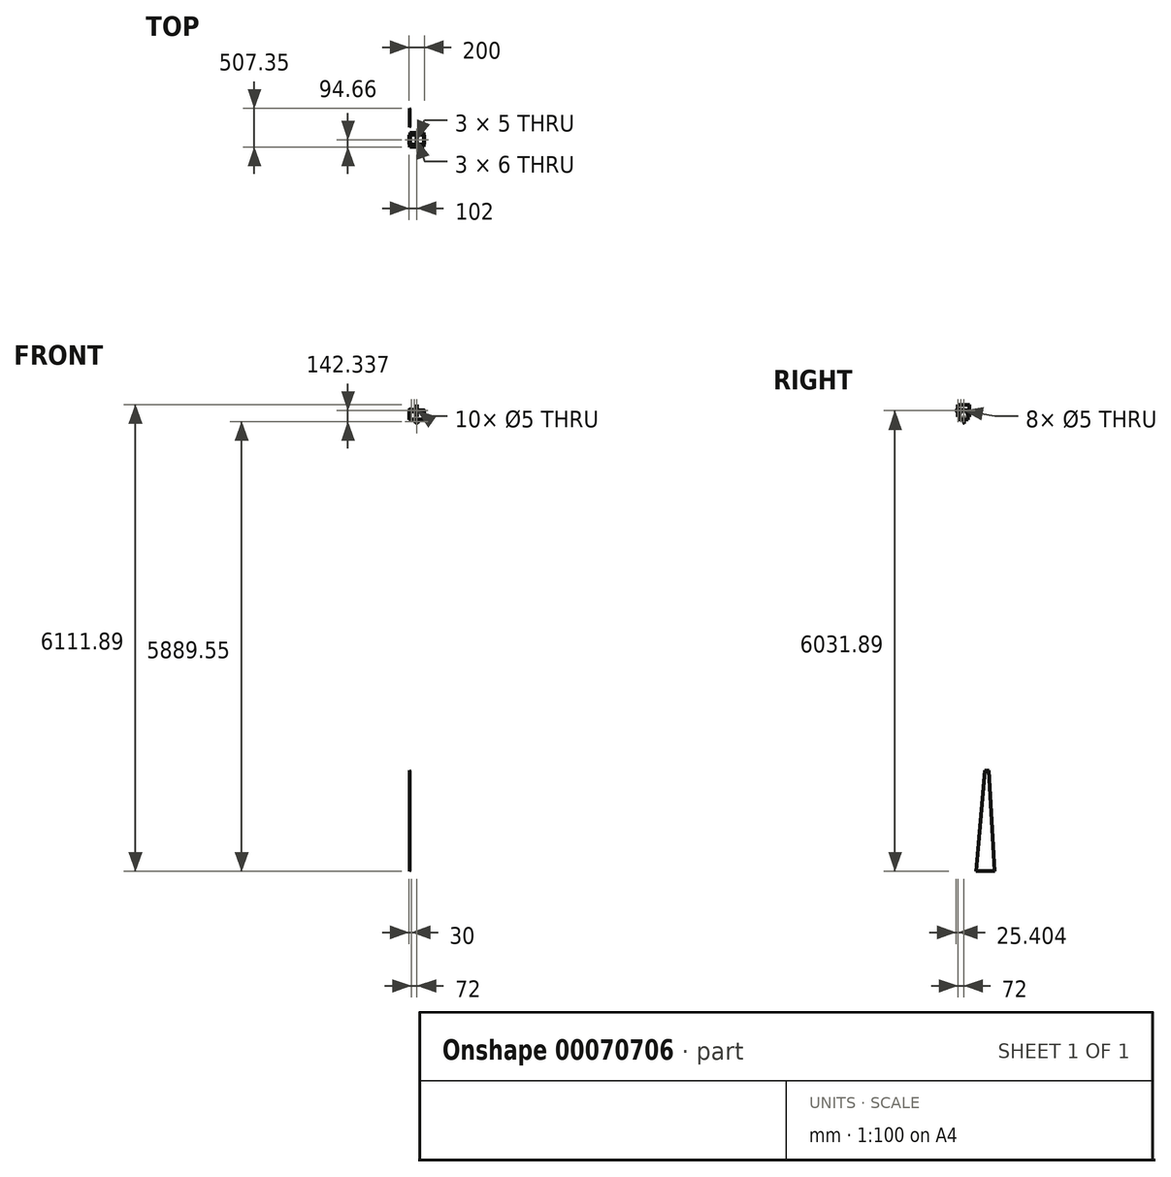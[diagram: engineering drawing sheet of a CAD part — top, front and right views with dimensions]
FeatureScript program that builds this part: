
annotation { "Feature Type Name" : "Feature", "Feature Type Description" : "" }
export const myFeature = defineFeature(function(context is Context, id is Id, definition is map)
    precondition{}
    {
        {
            var Q0;
            Q0=qCreatedBy(makeId("Top.planeOp"),FACE);
            var sketch = newSketch(context, id + "F0", { "sketchPlane" : qUnion([Q0])});
            skLineSegment(sketch, "E0.rect.bottom", {"start": v(100, 60) * mm, "end": v(-94, 60) * mm});
            skLineSegment(sketch, "E0.rect.top", {"start": v(94, -60) * mm, "end": v(-100, -60) * mm});
            skLineSegment(sketch, "E0.rect.left", {"start": v(100, 60) * mm, "end": v(100, 55) * mm});
            skLineSegment(sketch, "E0.rect.right", {"start": v(-100, 55) * mm, "end": v(-100, 50) * mm});
            skPoint(sketch, "E0.rect.middle", {"position": v(0, 0) * mm});
            skLineSegment(sketch, "E1.bottom", {"start": v(100, 55) * mm, "end": v(94, 55) * mm});
            skLineSegment(sketch, "E1.top", {"start": v(100, 50) * mm, "end": v(94, 50) * mm});
            skLineSegment(sketch, "E1.right", {"start": v(94, 55) * mm, "end": v(94, 50) * mm});
            skLineSegment(sketch, "E2.0.1.0", {"start": v(100, 45) * mm, "end": v(94, 45) * mm});
            skLineSegment(sketch, "E2.0.1.1", {"start": v(94, 45) * mm, "end": v(94, 40) * mm});
            skLineSegment(sketch, "E2.0.1.2", {"start": v(100, 40) * mm, "end": v(94, 40) * mm});
            skLineSegment(sketch, "E2.0.2.0", {"start": v(100, 35) * mm, "end": v(94, 35) * mm});
            skLineSegment(sketch, "E2.0.2.1", {"start": v(94, 35) * mm, "end": v(94, 30) * mm});
            skLineSegment(sketch, "E2.0.2.2", {"start": v(100, 30) * mm, "end": v(94, 30) * mm});
            skLineSegment(sketch, "E2.0.3.0", {"start": v(100, 25) * mm, "end": v(94, 25) * mm});
            skLineSegment(sketch, "E2.0.3.1", {"start": v(94, 25) * mm, "end": v(94, 20) * mm});
            skLineSegment(sketch, "E2.0.3.2", {"start": v(100, 20) * mm, "end": v(94, 20) * mm});
            skLineSegment(sketch, "E2.0.4.0", {"start": v(100, 15) * mm, "end": v(94, 15) * mm});
            skLineSegment(sketch, "E2.0.4.1", {"start": v(94, 15) * mm, "end": v(94, 10) * mm});
            skLineSegment(sketch, "E2.0.4.2", {"start": v(100, 10) * mm, "end": v(94, 10) * mm});
            skLineSegment(sketch, "E2.0.5.0", {"start": v(100, 5) * mm, "end": v(94, 5) * mm});
            skLineSegment(sketch, "E2.0.5.1", {"start": v(94, 5) * mm, "end": v(94, 0) * mm});
            skLineSegment(sketch, "E2.0.5.2", {"start": v(100, 0) * mm, "end": v(94, 0) * mm});
            skLineSegment(sketch, "E2.0.6.0", {"start": v(100, -5) * mm, "end": v(94, -5) * mm});
            skLineSegment(sketch, "E2.0.6.1", {"start": v(94, -5) * mm, "end": v(94, -10) * mm});
            skLineSegment(sketch, "E2.0.6.2", {"start": v(100, -10) * mm, "end": v(94, -10) * mm});
            skLineSegment(sketch, "E2.0.7.0", {"start": v(100, -15) * mm, "end": v(94, -15) * mm});
            skLineSegment(sketch, "E2.0.7.1", {"start": v(94, -15) * mm, "end": v(94, -20) * mm});
            skLineSegment(sketch, "E2.0.7.2", {"start": v(100, -20) * mm, "end": v(94, -20) * mm});
            skLineSegment(sketch, "E2.0.8.0", {"start": v(100, -25) * mm, "end": v(94, -25) * mm});
            skLineSegment(sketch, "E2.0.8.1", {"start": v(94, -25) * mm, "end": v(94, -30) * mm});
            skLineSegment(sketch, "E2.0.8.2", {"start": v(100, -30) * mm, "end": v(94, -30) * mm});
            skLineSegment(sketch, "E2.0.9.0", {"start": v(100, -35) * mm, "end": v(94, -35) * mm});
            skLineSegment(sketch, "E2.0.9.1", {"start": v(94, -35) * mm, "end": v(94, -40) * mm});
            skLineSegment(sketch, "E2.0.9.2", {"start": v(100, -40) * mm, "end": v(94, -40) * mm});
            skLineSegment(sketch, "E2.0.10.0", {"start": v(100, -45) * mm, "end": v(94, -45) * mm});
            skLineSegment(sketch, "E2.0.10.1", {"start": v(94, -45) * mm, "end": v(94, -50) * mm});
            skLineSegment(sketch, "E2.0.10.2", {"start": v(100, -50) * mm, "end": v(94, -50) * mm});
            skLineSegment(sketch, "E2.0.11.0", {"start": v(100, -55) * mm, "end": v(94, -55) * mm});
            skLineSegment(sketch, "E2.0.11.1", {"start": v(94, -55) * mm, "end": v(94, -60) * mm});
            skLineSegment(sketch, "E2.direction1", {"start": v(94, 55) * mm, "end": v(119, 55) * mm, "construction": true});
            skLineSegment(sketch, "E2.direction2", {"start": v(94, 55) * mm, "end": v(94, 45) * mm, "construction": true});
            skLineSegment(sketch, "E3", {"start": v(0, -60) * mm, "end": v(0, 60) * mm, "construction": true});
            skLineSegment(sketch, "E4.1.0", {"start": v(-100, -30) * mm, "end": v(-94.03, -29.38) * mm});
            skLineSegment(sketch, "E4.1.1", {"start": v(-100, 15) * mm, "end": v(-94, 15) * mm});
            skLineSegment(sketch, "E4.1.2", {"start": v(-94.03, -34.38) * mm, "end": v(-94.03, -29.38) * mm});
            skLineSegment(sketch, "E4.1.3", {"start": v(-100, 30) * mm, "end": v(-94, 30) * mm});
            skLineSegment(sketch, "E4.1.4", {"start": v(-100, 0) * mm, "end": v(-94, 0) * mm});
            skLineSegment(sketch, "E4.1.5", {"start": v(-100, 55) * mm, "end": v(-94, 55) * mm});
            skLineSegment(sketch, "E4.1.6", {"start": v(-94, 55) * mm, "end": v(-94, 60) * mm});
            skLineSegment(sketch, "E4.1.7", {"start": v(-100, -25) * mm, "end": v(-94, -25) * mm});
            skLineSegment(sketch, "E4.1.8", {"start": v(-100, 5) * mm, "end": v(-94, 5) * mm});
            skLineSegment(sketch, "E4.1.9", {"start": v(-94, -25) * mm, "end": v(-94, -20) * mm});
            skLineSegment(sketch, "E4.1.10", {"start": v(-100, 35) * mm, "end": v(-94, 35) * mm});
            skLineSegment(sketch, "E4.1.11", {"start": v(-100, -20) * mm, "end": v(-94, -20) * mm});
            skLineSegment(sketch, "E4.1.12", {"start": v(-100, -35) * mm, "end": v(-94.03, -34.38) * mm});
            skLineSegment(sketch, "E4.1.13", {"start": v(-100, -40) * mm, "end": v(-94, -40) * mm});
            skLineSegment(sketch, "E4.1.14", {"start": v(-94, -45) * mm, "end": v(-94, -40) * mm});
            skLineSegment(sketch, "E4.1.15", {"start": v(-94, -55) * mm, "end": v(-94, -50) * mm});
            skLineSegment(sketch, "E4.1.16", {"start": v(-94, 25) * mm, "end": v(-94, 30) * mm});
            skLineSegment(sketch, "E4.1.17", {"start": v(-100, 50) * mm, "end": v(-94, 50) * mm});
            skLineSegment(sketch, "E4.1.18", {"start": v(-94, -5) * mm, "end": v(-94, 0) * mm});
            skLineSegment(sketch, "E4.1.19", {"start": v(-100, 20) * mm, "end": v(-94, 20) * mm});
            skLineSegment(sketch, "E4.1.20", {"start": v(-94, 45) * mm, "end": v(-94, 50) * mm});
            skLineSegment(sketch, "E4.1.21", {"start": v(-100, 25) * mm, "end": v(-94, 25) * mm});
            skLineSegment(sketch, "E4.1.22", {"start": v(-100, 40) * mm, "end": v(-94, 40) * mm});
            skLineSegment(sketch, "E4.1.23", {"start": v(-100, -5) * mm, "end": v(-94, -5) * mm});
            skLineSegment(sketch, "E4.1.24", {"start": v(-94, 15) * mm, "end": v(-94, 20) * mm});
            skLineSegment(sketch, "E4.1.25", {"start": v(-94, -15) * mm, "end": v(-94, -10) * mm});
            skLineSegment(sketch, "E4.1.26", {"start": v(-100, 10) * mm, "end": v(-94, 10) * mm});
            skLineSegment(sketch, "E4.1.27", {"start": v(-94, 35) * mm, "end": v(-94, 40) * mm});
            skLineSegment(sketch, "E4.1.28", {"start": v(-100, 45) * mm, "end": v(-94, 45) * mm});
            skLineSegment(sketch, "E4.1.29", {"start": v(-100, -10) * mm, "end": v(-94, -10) * mm});
            skLineSegment(sketch, "E4.1.30", {"start": v(-100, -15) * mm, "end": v(-94, -15) * mm});
            skLineSegment(sketch, "E4.1.31", {"start": v(-94, 5) * mm, "end": v(-94, 10) * mm});
            skLineSegment(sketch, "E4.1.32", {"start": v(-100, -45) * mm, "end": v(-94, -45) * mm});
            skLineSegment(sketch, "E4.1.33", {"start": v(-100, -50) * mm, "end": v(-94, -50) * mm});
            skLineSegment(sketch, "E4.1.35", {"start": v(-100, -55) * mm, "end": v(-94, -55) * mm});
            skPoint(sketch, "E4.center", {"position": v(-1, 0) * mm});
            skLineSegment(sketch, "E4.anchor1", {"start": v(-1, 0) * mm, "end": v(94, 30) * mm, "construction": true});
            skLineSegment(sketch, "E4.anchor2", {"start": v(-1, 0) * mm, "end": v(-94.03, -29.38) * mm, "construction": true});
            skLineSegment(sketch, "E5.trimOffspring", {"start": v(100, 50) * mm, "end": v(100, 45) * mm});
            skLineSegment(sketch, "E6.trimOffspring", {"start": v(100, 40) * mm, "end": v(100, 35) * mm});
            skLineSegment(sketch, "E7.trimOffspring", {"start": v(100, 30) * mm, "end": v(100, 25) * mm});
            skLineSegment(sketch, "E8.trimOffspring", {"start": v(100, 20) * mm, "end": v(100, 15) * mm});
            skLineSegment(sketch, "E9.trimOffspring", {"start": v(100, 10) * mm, "end": v(100, 5) * mm});
            skLineSegment(sketch, "E10.trimOffspring", {"start": v(100, 0) * mm, "end": v(100, -5) * mm});
            skLineSegment(sketch, "E11.trimOffspring", {"start": v(100, -10) * mm, "end": v(100, -15) * mm});
            skLineSegment(sketch, "E12.trimOffspring", {"start": v(100, -20) * mm, "end": v(100, -25) * mm});
            skLineSegment(sketch, "E13.trimOffspring", {"start": v(100, -30) * mm, "end": v(100, -35) * mm});
            skLineSegment(sketch, "E14.trimOffspring", {"start": v(100, -40) * mm, "end": v(100, -45) * mm});
            skLineSegment(sketch, "E15.trimOffspring", {"start": v(100, -50) * mm, "end": v(100, -55) * mm});
            skPoint(sketch, "E16.orphan", {"position": v(100, -60) * mm});
            skPoint(sketch, "E17.orphan", {"position": v(-100, 60) * mm});
            skLineSegment(sketch, "E18.trimOffspring", {"start": v(-100, 45) * mm, "end": v(-100, 40) * mm});
            skLineSegment(sketch, "E19.trimOffspring", {"start": v(-100, 35) * mm, "end": v(-100, 30) * mm});
            skLineSegment(sketch, "E20.trimOffspring", {"start": v(-100, 25) * mm, "end": v(-100, 20) * mm});
            skLineSegment(sketch, "E21.trimOffspring", {"start": v(-100, 15) * mm, "end": v(-100, 10) * mm});
            skLineSegment(sketch, "E22.trimOffspring", {"start": v(-100, 5) * mm, "end": v(-100, 0) * mm});
            skLineSegment(sketch, "E23.trimOffspring", {"start": v(-100, -5) * mm, "end": v(-100, -10) * mm});
            skLineSegment(sketch, "E24.trimOffspring", {"start": v(-100, -15) * mm, "end": v(-100, -20) * mm});
            skLineSegment(sketch, "E25.trimOffspring", {"start": v(-100, -55) * mm, "end": v(-100, -60) * mm});
            skLineSegment(sketch, "E26.trimOffspring", {"start": v(-100, -45) * mm, "end": v(-100, -50) * mm});
            skLineSegment(sketch, "E27.trimOffspring", {"start": v(-100, -35) * mm, "end": v(-100, -40) * mm});
            skLineSegment(sketch, "E28.trimOffspring", {"start": v(-100, -25) * mm, "end": v(-100, -30) * mm});
            skSolve(sketch);
        }
        {
            var Q0;
            Q0=makeQuery(id+"F0.imprint","IMPRINT",FACE,{"disambiguationData":[TD([[makeQuery(id+"F0.imprint","IMPRINT",EDGE,{"derivedFrom":sQuery(id+"F0.wireOp",EDGE,"E0.rect.bottom")}),1.0]])]});
            extrude(context, id + "F1", {"entities" : qUnion([Q0]), "depth" : 6 * mm});
        }
        {
            var Q0;
            Q0=makeQuery(id+"F1.opExtrude","SWEPT_FACE",FACE,{"disambiguationData":[OSD([sQuery(id+"F0.wireOp",EDGE,"E5.trimOffspring")])]});
            var sketch = newSketch(context, id + "F2", { "sketchPlane" : qUnion([Q0])});
            skLineSegment(sketch, "E29.bottom", {"start": v(55, 0) * mm, "end": v(50, 0) * mm});
            skLineSegment(sketch, "E29.top", {"start": v(60, 130) * mm, "end": v(-60, 130) * mm, "construction": true});
            skLineSegment(sketch, "E29.left", {"start": v(60, 6) * mm, "end": v(60, 130) * mm, "construction": true});
            skLineSegment(sketch, "E29.right", {"start": v(-60, 0) * mm, "end": v(-60, 130) * mm, "construction": true});
            skLineSegment(sketch, "E30", {"start": v(-57.9, 54.8) * mm, "end": v(-31.55, 115.02) * mm});
            skLineSegment(sketch, "E31", {"start": v(-8.65, 130) * mm, "end": v(8.65, 130) * mm});
            skLineSegment(sketch, "E32", {"start": v(31.55, 115.02) * mm, "end": v(57.9, 54.8) * mm});
            skLineSegment(sketch, "E33", {"start": v(60, 44.77) * mm, "end": v(60, 6) * mm});
            skLineSegment(sketch, "E34", {"start": v(-60, 44.77) * mm, "end": v(-60, 0) * mm});
            skPoint(sketch, "E35", {"position": v(0, 130) * mm});
            skPoint(sketch, "E36.visualSharp", {"position": v(-25, 130) * mm});
            skArc(sketch, "E36.filletArc", {"start": v(-8.65, 130) * mm, "mid": v(-22.33, 125.92) * mm, "end": v(-31.55, 115.02) * mm});
            skPoint(sketch, "E37.visualSharp", {"position": v(-60, 50) * mm});
            skArc(sketch, "E37.filletArc", {"start": v(-57.9, 54.8) * mm, "mid": v(-59.47, 49.89) * mm, "end": v(-60, 44.77) * mm});
            skPoint(sketch, "E38.visualSharp", {"position": v(25, 130) * mm});
            skArc(sketch, "E38.filletArc", {"start": v(31.55, 115.02) * mm, "mid": v(22.33, 125.92) * mm, "end": v(8.65, 130) * mm});
            skPoint(sketch, "E39.visualSharp", {"position": v(60, 50) * mm});
            skArc(sketch, "E39.filletArc", {"start": v(60, 44.77) * mm, "mid": v(59.47, 49.89) * mm, "end": v(57.9, 54.8) * mm});
            skLineSegment(sketch, "E40", {"start": v(0, 130) * mm, "end": v(0, 120) * mm, "construction": true});
            skCircle(sketch, "E41", {"center": v(0, 120) * mm, "radius": 2.5 * mm});
            skLineSegment(sketch, "E42.top", {"start": v(60, 6) * mm, "end": v(55, 6) * mm});
            skLineSegment(sketch, "E42.right", {"start": v(55, 0) * mm, "end": v(55, 6) * mm});
            skLineSegment(sketch, "E43.1.0.0", {"start": v(45, 0) * mm, "end": v(45, 6) * mm});
            skLineSegment(sketch, "E43.1.0.1", {"start": v(50, 6) * mm, "end": v(45, 6) * mm});
            skLineSegment(sketch, "E43.1.0.2", {"start": v(50, 0) * mm, "end": v(50, 6) * mm});
            skLineSegment(sketch, "E43.2.0.0", {"start": v(35, 0) * mm, "end": v(35, 6) * mm});
            skLineSegment(sketch, "E43.2.0.1", {"start": v(40, 6) * mm, "end": v(35, 6) * mm});
            skLineSegment(sketch, "E43.2.0.2", {"start": v(40, 0) * mm, "end": v(40, 6) * mm});
            skLineSegment(sketch, "E43.3.0.0", {"start": v(25, 0) * mm, "end": v(25, 6) * mm});
            skLineSegment(sketch, "E43.3.0.1", {"start": v(30, 6) * mm, "end": v(25, 6) * mm});
            skLineSegment(sketch, "E43.3.0.2", {"start": v(30, 0) * mm, "end": v(30, 6) * mm});
            skLineSegment(sketch, "E43.4.0.0", {"start": v(15, 0) * mm, "end": v(15, 6) * mm});
            skLineSegment(sketch, "E43.4.0.1", {"start": v(20, 6) * mm, "end": v(15, 6) * mm});
            skLineSegment(sketch, "E43.4.0.2", {"start": v(20, 0) * mm, "end": v(20, 6) * mm});
            skLineSegment(sketch, "E43.5.0.0", {"start": v(5, 0) * mm, "end": v(5, 6) * mm});
            skLineSegment(sketch, "E43.5.0.1", {"start": v(10, 6) * mm, "end": v(5, 6) * mm});
            skLineSegment(sketch, "E43.5.0.2", {"start": v(10, 0) * mm, "end": v(10, 6) * mm});
            skLineSegment(sketch, "E43.6.0.0", {"start": v(-5, 0) * mm, "end": v(-5, 6) * mm});
            skLineSegment(sketch, "E43.6.0.1", {"start": v(0, 6) * mm, "end": v(-5, 6) * mm});
            skLineSegment(sketch, "E43.6.0.2", {"start": v(0, 0) * mm, "end": v(0, 6) * mm});
            skLineSegment(sketch, "E43.7.0.0", {"start": v(-15, 0) * mm, "end": v(-15, 6) * mm});
            skLineSegment(sketch, "E43.7.0.1", {"start": v(-10, 6) * mm, "end": v(-15, 6) * mm});
            skLineSegment(sketch, "E43.7.0.2", {"start": v(-10, 0) * mm, "end": v(-10, 6) * mm});
            skLineSegment(sketch, "E43.8.0.0", {"start": v(-25, 0) * mm, "end": v(-25, 6) * mm});
            skLineSegment(sketch, "E43.8.0.1", {"start": v(-20, 6) * mm, "end": v(-25, 6) * mm});
            skLineSegment(sketch, "E43.8.0.2", {"start": v(-20, 0) * mm, "end": v(-20, 6) * mm});
            skLineSegment(sketch, "E43.9.0.0", {"start": v(-35, 0) * mm, "end": v(-35, 6) * mm});
            skLineSegment(sketch, "E43.9.0.1", {"start": v(-30, 6) * mm, "end": v(-35, 6) * mm});
            skLineSegment(sketch, "E43.9.0.2", {"start": v(-30, 0) * mm, "end": v(-30, 6) * mm});
            skLineSegment(sketch, "E43.10.0.0", {"start": v(-45, 0) * mm, "end": v(-45, 6) * mm});
            skLineSegment(sketch, "E43.10.0.1", {"start": v(-40, 6) * mm, "end": v(-45, 6) * mm});
            skLineSegment(sketch, "E43.10.0.2", {"start": v(-40, 0) * mm, "end": v(-40, 6) * mm});
            skLineSegment(sketch, "E43.11.0.0", {"start": v(-55, 0) * mm, "end": v(-55, 6) * mm});
            skLineSegment(sketch, "E43.11.0.1", {"start": v(-50, 6) * mm, "end": v(-55, 6) * mm});
            skLineSegment(sketch, "E43.11.0.2", {"start": v(-50, 0) * mm, "end": v(-50, 6) * mm});
            skLineSegment(sketch, "E43.direction1", {"start": v(55, 0) * mm, "end": v(45, 0) * mm, "construction": true});
            skLineSegment(sketch, "E44.trimOffspring", {"start": v(45, 0) * mm, "end": v(40, 0) * mm});
            skLineSegment(sketch, "E45.trimOffspring", {"start": v(35, 0) * mm, "end": v(30, 0) * mm});
            skLineSegment(sketch, "E46.trimOffspring", {"start": v(25, 0) * mm, "end": v(20, 0) * mm});
            skLineSegment(sketch, "E47.trimOffspring", {"start": v(15, 0) * mm, "end": v(10, 0) * mm});
            skLineSegment(sketch, "E48.trimOffspring", {"start": v(5, 0) * mm, "end": v(0, 0) * mm});
            skLineSegment(sketch, "E49.trimOffspring", {"start": v(-5, 0) * mm, "end": v(-10, 0) * mm});
            skLineSegment(sketch, "E50.trimOffspring", {"start": v(-15, 0) * mm, "end": v(-20, 0) * mm});
            skLineSegment(sketch, "E51.trimOffspring", {"start": v(-25, 0) * mm, "end": v(-30, 0) * mm});
            skLineSegment(sketch, "E52.trimOffspring", {"start": v(-35, 0) * mm, "end": v(-40, 0) * mm});
            skLineSegment(sketch, "E53.trimOffspring", {"start": v(-45, 0) * mm, "end": v(-50, 0) * mm});
            skLineSegment(sketch, "E54.trimOffspring", {"start": v(-55, 0) * mm, "end": v(-60, 0) * mm});
            skSolve(sketch);
        }
        {
            var Q0;
            Q0 = qSketchRegion(id + "F2", true);
            extrude(context, id + "F3", {"entities" : qUnion([Q0]), "oppositeDirection" : true, "depth" : 6 * mm});
        }
        {
            var Q0;
            Q0=makeQuery(id+"F1.opExtrude","SWEPT_FACE",FACE,{"disambiguationData":[OSD([sQuery(id+"F0.wireOp",EDGE,"E0.rect.right")])]});
            var sketch = newSketch(context, id + "F4", { "sketchPlane" : qUnion([Q0])});
            skLineSegment(sketch, "E55.bottom", {"start": v(55, 0) * mm, "end": v(50, 0) * mm});
            skLineSegment(sketch, "E55.top", {"start": v(60, 130) * mm, "end": v(-60, 130) * mm, "construction": true});
            skLineSegment(sketch, "E55.left", {"start": v(60, 6) * mm, "end": v(60, 130) * mm, "construction": true});
            skLineSegment(sketch, "E55.right", {"start": v(-60, 0) * mm, "end": v(-60, 130) * mm, "construction": true});
            skLineSegment(sketch, "E56", {"start": v(-60, 0) * mm, "end": v(-60, 44.81) * mm});
            skLineSegment(sketch, "E57", {"start": v(-57.94, 54.76) * mm, "end": v(-31.84, 114.94) * mm});
            skLineSegment(sketch, "E58", {"start": v(-8.9, 130) * mm, "end": v(8.42, 130) * mm});
            skLineSegment(sketch, "E59", {"start": v(31.27, 115.13) * mm, "end": v(57.86, 55.16) * mm});
            skLineSegment(sketch, "E60", {"start": v(60, 45.03) * mm, "end": v(60, 6) * mm});
            skPoint(sketch, "E61.visualSharp", {"position": v(-60, 50) * mm});
            skArc(sketch, "E61.filletArc", {"start": v(-57.94, 54.76) * mm, "mid": v(-59.48, 49.9) * mm, "end": v(-60, 44.81) * mm});
            skPoint(sketch, "E62.visualSharp", {"position": v(-25.32, 130) * mm});
            skArc(sketch, "E62.filletArc", {"start": v(-8.9, 130) * mm, "mid": v(-22.63, 125.9) * mm, "end": v(-31.84, 114.94) * mm});
            skPoint(sketch, "E63.visualSharp", {"position": v(24.68, 130) * mm});
            skArc(sketch, "E63.filletArc", {"start": v(31.27, 115.13) * mm, "mid": v(22.05, 125.96) * mm, "end": v(8.42, 130) * mm});
            skPoint(sketch, "E64.visualSharp", {"position": v(60, 50.32) * mm});
            skArc(sketch, "E64.filletArc", {"start": v(60, 45.03) * mm, "mid": v(59.46, 50.2) * mm, "end": v(57.86, 55.16) * mm});
            skLineSegment(sketch, "E65", {"start": v(-0.24, 130) * mm, "end": v(-0.24, 120) * mm, "construction": true});
            skPoint(sketch, "E65.endSnap0", {"position": v(-0.24, 130) * mm});
            skCircle(sketch, "E66", {"center": v(-0.24, 120) * mm, "radius": 2.5 * mm});
            skLineSegment(sketch, "E67.top", {"start": v(60, 6) * mm, "end": v(55, 6) * mm});
            skLineSegment(sketch, "E67.right", {"start": v(55, 0) * mm, "end": v(55, 6) * mm});
            skLineSegment(sketch, "E68.1.0.0", {"start": v(45, 0) * mm, "end": v(45, 6) * mm});
            skLineSegment(sketch, "E68.1.0.1", {"start": v(50, 6) * mm, "end": v(45, 6) * mm});
            skLineSegment(sketch, "E68.1.0.2", {"start": v(50, 0) * mm, "end": v(50, 6) * mm});
            skLineSegment(sketch, "E68.2.0.0", {"start": v(35, 0) * mm, "end": v(35, 6) * mm});
            skLineSegment(sketch, "E68.2.0.1", {"start": v(40, 6) * mm, "end": v(35, 6) * mm});
            skLineSegment(sketch, "E68.2.0.2", {"start": v(40, 0) * mm, "end": v(40, 6) * mm});
            skLineSegment(sketch, "E68.3.0.0", {"start": v(25, 0) * mm, "end": v(25, 6) * mm});
            skLineSegment(sketch, "E68.3.0.1", {"start": v(30, 6) * mm, "end": v(25, 6) * mm});
            skLineSegment(sketch, "E68.3.0.2", {"start": v(30, 0) * mm, "end": v(30, 6) * mm});
            skLineSegment(sketch, "E68.4.0.0", {"start": v(15, 0) * mm, "end": v(15, 6) * mm});
            skLineSegment(sketch, "E68.4.0.1", {"start": v(20, 6) * mm, "end": v(15, 6) * mm});
            skLineSegment(sketch, "E68.4.0.2", {"start": v(20, 0) * mm, "end": v(20, 6) * mm});
            skLineSegment(sketch, "E68.5.0.0", {"start": v(5, 0) * mm, "end": v(5, 6) * mm});
            skLineSegment(sketch, "E68.5.0.1", {"start": v(10, 6) * mm, "end": v(5, 6) * mm});
            skLineSegment(sketch, "E68.5.0.2", {"start": v(10, 0) * mm, "end": v(10, 6) * mm});
            skLineSegment(sketch, "E68.6.0.0", {"start": v(-5, 0) * mm, "end": v(-5, 6) * mm});
            skLineSegment(sketch, "E68.6.0.1", {"start": v(0, 6) * mm, "end": v(-5, 6) * mm});
            skLineSegment(sketch, "E68.6.0.2", {"start": v(0, 0) * mm, "end": v(0, 6) * mm});
            skLineSegment(sketch, "E68.7.0.0", {"start": v(-15, 0) * mm, "end": v(-15, 6) * mm});
            skLineSegment(sketch, "E68.7.0.1", {"start": v(-10, 6) * mm, "end": v(-15, 6) * mm});
            skLineSegment(sketch, "E68.7.0.2", {"start": v(-10, 0) * mm, "end": v(-10, 6) * mm});
            skLineSegment(sketch, "E68.8.0.0", {"start": v(-25, 0) * mm, "end": v(-25, 6) * mm});
            skLineSegment(sketch, "E68.8.0.1", {"start": v(-20, 6) * mm, "end": v(-25, 6) * mm});
            skLineSegment(sketch, "E68.8.0.2", {"start": v(-20, 0) * mm, "end": v(-20, 6) * mm});
            skLineSegment(sketch, "E68.9.0.0", {"start": v(-35, 0) * mm, "end": v(-35, 6) * mm});
            skLineSegment(sketch, "E68.9.0.1", {"start": v(-30, 6) * mm, "end": v(-35, 6) * mm});
            skLineSegment(sketch, "E68.9.0.2", {"start": v(-30, 0) * mm, "end": v(-30, 6) * mm});
            skLineSegment(sketch, "E68.10.0.0", {"start": v(-45, 0) * mm, "end": v(-45, 6) * mm});
            skLineSegment(sketch, "E68.10.0.1", {"start": v(-40, 6) * mm, "end": v(-45, 6) * mm});
            skLineSegment(sketch, "E68.10.0.2", {"start": v(-40, 0) * mm, "end": v(-40, 6) * mm});
            skLineSegment(sketch, "E68.11.0.0", {"start": v(-55, 0) * mm, "end": v(-55, 6) * mm});
            skLineSegment(sketch, "E68.11.0.1", {"start": v(-50, 6) * mm, "end": v(-55, 6) * mm});
            skLineSegment(sketch, "E68.11.0.2", {"start": v(-50, 0) * mm, "end": v(-50, 6) * mm});
            skLineSegment(sketch, "E68.direction1", {"start": v(55, 0) * mm, "end": v(45, 0) * mm, "construction": true});
            skLineSegment(sketch, "E69.trimOffspring", {"start": v(45, 0) * mm, "end": v(40, 0) * mm});
            skLineSegment(sketch, "E70.trimOffspring", {"start": v(35, 0) * mm, "end": v(30, 0) * mm});
            skLineSegment(sketch, "E71.trimOffspring", {"start": v(25, 0) * mm, "end": v(20, 0) * mm});
            skLineSegment(sketch, "E72.trimOffspring", {"start": v(15, 0) * mm, "end": v(10, 0) * mm});
            skLineSegment(sketch, "E73.trimOffspring", {"start": v(5, 0) * mm, "end": v(0, 0) * mm});
            skLineSegment(sketch, "E74.trimOffspring", {"start": v(-5, 0) * mm, "end": v(-10, 0) * mm});
            skLineSegment(sketch, "E75.trimOffspring", {"start": v(-15, 0) * mm, "end": v(-20, 0) * mm});
            skLineSegment(sketch, "E76.trimOffspring", {"start": v(-25, 0) * mm, "end": v(-30, 0) * mm});
            skLineSegment(sketch, "E77.trimOffspring", {"start": v(-35, 0) * mm, "end": v(-40, 0) * mm});
            skLineSegment(sketch, "E78.trimOffspring", {"start": v(-45, 0) * mm, "end": v(-50, 0) * mm});
            skLineSegment(sketch, "E79.trimOffspring", {"start": v(-55, 0) * mm, "end": v(-60, 0) * mm});
            skSolve(sketch);
        }
        {
            var Q0;
            Q0 = qSketchRegion(id + "F4", true);
            extrude(context, id + "F5", {"entities" : qUnion([Q0]), "oppositeDirection" : true, "depth" : 6 * mm});
        }
        {
            var Q0;
            Q0=makeQuery(id+"F5.opExtrude","CAP_FACE",FACE,{"disambiguationData":[OSD([sQuery(id+"F4.wireOp",EDGE,"E55.bottom"),sQuery(id+"F4.wireOp",EDGE,"E56"),sQuery(id+"F4.wireOp",EDGE,"E57"),sQuery(id+"F4.wireOp",EDGE,"E58"),sQuery(id+"F4.wireOp",EDGE,"E59"),sQuery(id+"F4.wireOp",EDGE,"E60"),sQuery(id+"F4.wireOp",EDGE,"E61.filletArc"),sQuery(id+"F4.wireOp",EDGE,"E62.filletArc"),sQuery(id+"F4.wireOp",EDGE,"E63.filletArc"),sQuery(id+"F4.wireOp",EDGE,"E64.filletArc"),sQuery(id+"F4.wireOp",EDGE,"E66"),sQuery(id+"F4.wireOp",EDGE,"E67.top"),sQuery(id+"F4.wireOp",EDGE,"E67.right"),sQuery(id+"F4.wireOp",EDGE,"E68.1.0.0"),sQuery(id+"F4.wireOp",EDGE,"E68.1.0.1"),sQuery(id+"F4.wireOp",EDGE,"E68.1.0.2"),sQuery(id+"F4.wireOp",EDGE,"E68.2.0.0"),sQuery(id+"F4.wireOp",EDGE,"E68.2.0.1"),sQuery(id+"F4.wireOp",EDGE,"E68.2.0.2"),sQuery(id+"F4.wireOp",EDGE,"E68.3.0.0"),sQuery(id+"F4.wireOp",EDGE,"E68.3.0.1"),sQuery(id+"F4.wireOp",EDGE,"E68.3.0.2"),sQuery(id+"F4.wireOp",EDGE,"E68.4.0.0"),sQuery(id+"F4.wireOp",EDGE,"E68.4.0.1"),sQuery(id+"F4.wireOp",EDGE,"E68.4.0.2"),sQuery(id+"F4.wireOp",EDGE,"E68.5.0.0"),sQuery(id+"F4.wireOp",EDGE,"E68.5.0.1"),sQuery(id+"F4.wireOp",EDGE,"E68.5.0.2"),sQuery(id+"F4.wireOp",EDGE,"E68.6.0.0"),sQuery(id+"F4.wireOp",EDGE,"E68.6.0.1"),sQuery(id+"F4.wireOp",EDGE,"E68.6.0.2"),sQuery(id+"F4.wireOp",EDGE,"E68.7.0.0"),sQuery(id+"F4.wireOp",EDGE,"E68.7.0.1"),sQuery(id+"F4.wireOp",EDGE,"E68.7.0.2"),sQuery(id+"F4.wireOp",EDGE,"E68.8.0.0"),sQuery(id+"F4.wireOp",EDGE,"E68.8.0.1"),sQuery(id+"F4.wireOp",EDGE,"E68.8.0.2"),sQuery(id+"F4.wireOp",EDGE,"E68.9.0.0"),sQuery(id+"F4.wireOp",EDGE,"E68.9.0.1"),sQuery(id+"F4.wireOp",EDGE,"E68.9.0.2"),sQuery(id+"F4.wireOp",EDGE,"E68.10.0.0"),sQuery(id+"F4.wireOp",EDGE,"E68.10.0.1"),sQuery(id+"F4.wireOp",EDGE,"E68.10.0.2"),sQuery(id+"F4.wireOp",EDGE,"E68.11.0.0"),sQuery(id+"F4.wireOp",EDGE,"E68.11.0.1"),sQuery(id+"F4.wireOp",EDGE,"E68.11.0.2"),sQuery(id+"F4.wireOp",EDGE,"E69.trimOffspring"),sQuery(id+"F4.wireOp",EDGE,"E70.trimOffspring"),sQuery(id+"F4.wireOp",EDGE,"E71.trimOffspring"),sQuery(id+"F4.wireOp",EDGE,"E72.trimOffspring"),sQuery(id+"F4.wireOp",EDGE,"E73.trimOffspring"),sQuery(id+"F4.wireOp",EDGE,"E74.trimOffspring"),sQuery(id+"F4.wireOp",EDGE,"E75.trimOffspring"),sQuery(id+"F4.wireOp",EDGE,"E76.trimOffspring"),sQuery(id+"F4.wireOp",EDGE,"E77.trimOffspring"),sQuery(id+"F4.wireOp",EDGE,"E78.trimOffspring"),sQuery(id+"F4.wireOp",EDGE,"E79.trimOffspring")])],"isStart":false});
            var sketch = newSketch(context, id + "F6", { "sketchPlane" : qUnion([Q0])});
            skCircle(sketch, "E80", {"center": v(0.24, 120) * mm, "radius": 16.4 * mm, "construction": true});
            skCircle(sketch, "E81", {"center": v(0.24, 120) * mm, "radius": 19.4 * mm, "construction": true});
            skCircle(sketch, "E82", {"center": v(0.24, 120) * mm, "radius": 2.5 * mm});
            skLineSegment(sketch, "E83", {"start": v(0.24, 120) * mm, "end": v(0.24, 139.4) * mm, "construction": true});
            skLineSegment(sketch, "E84", {"start": v(0.24, 120) * mm, "end": v(-3.12, 139.1) * mm, "construction": true});
            skLineSegment(sketch, "E85", {"start": v(0.24, 120) * mm, "end": v(-1.45, 139.33) * mm, "construction": true});
            skLineSegment(sketch, "E86", {"start": v(0.24, 120) * mm, "end": v(-0.6, 139.38) * mm, "construction": true});
            skLineSegment(sketch, "E87", {"start": v(0.24, 120) * mm, "end": v(-2.29, 139.23) * mm, "construction": true});
            skLineSegment(sketch, "E88", {"start": v(-0.18, 139.4) * mm, "end": v(0.24, 120) * mm, "construction": true});
            skLineSegment(sketch, "E89", {"start": v(-2.7, 139.17) * mm, "end": v(0.24, 120) * mm, "construction": true});
            skLineSegment(sketch, "E90", {"start": v(-1.02, 139.36) * mm, "end": v(0.24, 120) * mm, "construction": true});
            skLineSegment(sketch, "E91", {"start": v(-1.87, 139.28) * mm, "end": v(0.24, 120) * mm, "construction": true});
            skArc(sketch, "E92", {"start": v(-1.43, 139.33) * mm, "mid": v(-1.45, 139.33) * mm, "end": v(-1.47, 139.32) * mm});
            skLineSegment(sketch, "E93", {"start": v(-0.9, 138.98) * mm, "end": v(-0.22, 136.76) * mm});
            skLineSegment(sketch, "E94", {"start": v(-1.92, 138.89) * mm, "end": v(-2.2, 136.58) * mm});
            skLineSegment(sketch, "E95", {"start": v(0.24, 136.4) * mm, "end": v(0.26, 136.4) * mm});
            skLineSegment(sketch, "E96", {"start": v(-2.6, 136.15) * mm, "end": v(-2.62, 136.15) * mm});
            skPoint(sketch, "E97.visualSharp", {"position": v(-0.11, 136.4) * mm});
            skArc(sketch, "E97.filletArc", {"start": v(-0.22, 136.76) * mm, "mid": v(-0.04, 136.5) * mm, "end": v(0.26, 136.4) * mm});
            skPoint(sketch, "E98.visualSharp", {"position": v(-2.25, 136.2) * mm});
            skArc(sketch, "E98.filletArc", {"start": v(-2.62, 136.15) * mm, "mid": v(-2.34, 136.3) * mm, "end": v(-2.2, 136.58) * mm});
            skPoint(sketch, "E99.visualSharp", {"position": v(-1.02, 139.36) * mm});
            skArc(sketch, "E99.filletArc", {"start": v(-0.9, 138.98) * mm, "mid": v(-1.1, 139.24) * mm, "end": v(-1.43, 139.33) * mm});
            skPoint(sketch, "E100.visualSharp", {"position": v(-1.87, 139.28) * mm});
            skArc(sketch, "E100.filletArc", {"start": v(-1.47, 139.32) * mm, "mid": v(-1.77, 139.19) * mm, "end": v(-1.92, 138.89) * mm});
            skLineSegment(sketch, "E101.1.0", {"start": v(-2.6, 136.15) * mm, "end": v(-2.58, 136.16) * mm});
            skArc(sketch, "E101.1.1", {"start": v(-3.13, 136.42) * mm, "mid": v(-2.9, 136.2) * mm, "end": v(-2.58, 136.16) * mm});
            skLineSegment(sketch, "E101.1.2", {"start": v(-4.19, 138.49) * mm, "end": v(-3.13, 136.42) * mm});
            skArc(sketch, "E101.1.3", {"start": v(-4.19, 138.49) * mm, "mid": v(-4.43, 138.72) * mm, "end": v(-4.76, 138.74) * mm});
            skArc(sketch, "E101.1.4", {"start": v(-4.76, 138.74) * mm, "mid": v(-4.78, 138.74) * mm, "end": v(-4.8, 138.73) * mm});
            skArc(sketch, "E101.1.5", {"start": v(-4.8, 138.73) * mm, "mid": v(-5.07, 138.55) * mm, "end": v(-5.16, 138.23) * mm});
            skLineSegment(sketch, "E101.1.6", {"start": v(-5.16, 138.23) * mm, "end": v(-5.05, 135.9) * mm});
            skArc(sketch, "E101.1.7", {"start": v(-5.39, 135.4) * mm, "mid": v(-5.13, 135.6) * mm, "end": v(-5.05, 135.9) * mm});
            skLineSegment(sketch, "E101.1.8", {"start": v(-5.37, 135.41) * mm, "end": v(-5.39, 135.4) * mm});
            skLineSegment(sketch, "E101.2.0", {"start": v(-5.37, 135.41) * mm, "end": v(-5.35, 135.42) * mm});
            skArc(sketch, "E101.2.1", {"start": v(-5.93, 135.59) * mm, "mid": v(-5.67, 135.4) * mm, "end": v(-5.35, 135.42) * mm});
            skLineSegment(sketch, "E101.2.2", {"start": v(-7.33, 137.44) * mm, "end": v(-5.93, 135.59) * mm});
            skArc(sketch, "E101.2.3", {"start": v(-7.33, 137.44) * mm, "mid": v(-7.6, 137.62) * mm, "end": v(-7.94, 137.6) * mm});
            skArc(sketch, "E101.2.4", {"start": v(-7.94, 137.6) * mm, "mid": v(-7.95, 137.58) * mm, "end": v(-7.97, 137.57) * mm});
            skArc(sketch, "E101.2.5", {"start": v(-7.97, 137.57) * mm, "mid": v(-8.2, 137.34) * mm, "end": v(-8.25, 137) * mm});
            skLineSegment(sketch, "E101.2.6", {"start": v(-8.25, 137) * mm, "end": v(-7.73, 134.75) * mm});
            skArc(sketch, "E101.2.7", {"start": v(-7.98, 134.2) * mm, "mid": v(-7.76, 134.43) * mm, "end": v(-7.73, 134.75) * mm});
            skLineSegment(sketch, "E101.2.8", {"start": v(-7.96, 134.2) * mm, "end": v(-7.98, 134.2) * mm});
            skLineSegment(sketch, "E101.3.0", {"start": v(-7.96, 134.2) * mm, "end": v(-7.94, 134.22) * mm});
            skArc(sketch, "E101.3.1", {"start": v(-8.54, 134.28) * mm, "mid": v(-8.25, 134.15) * mm, "end": v(-7.94, 134.22) * mm});
            skLineSegment(sketch, "E101.3.2", {"start": v(-10.24, 135.86) * mm, "end": v(-8.54, 134.28) * mm});
            skArc(sketch, "E101.3.3", {"start": v(-10.24, 135.86) * mm, "mid": v(-10.55, 136) * mm, "end": v(-10.87, 135.9) * mm});
            skArc(sketch, "E101.3.4", {"start": v(-10.87, 135.9) * mm, "mid": v(-10.88, 135.9) * mm, "end": v(-10.9, 135.88) * mm});
            skArc(sketch, "E101.3.5", {"start": v(-10.9, 135.88) * mm, "mid": v(-11.1, 135.6) * mm, "end": v(-11.07, 135.28) * mm});
            skLineSegment(sketch, "E101.3.6", {"start": v(-11.07, 135.28) * mm, "end": v(-10.17, 133.14) * mm});
            skArc(sketch, "E101.3.7", {"start": v(-10.32, 132.55) * mm, "mid": v(-10.14, 132.82) * mm, "end": v(-10.17, 133.14) * mm});
            skLineSegment(sketch, "E101.3.8", {"start": v(-10.3, 132.57) * mm, "end": v(-10.32, 132.55) * mm});
            skLineSegment(sketch, "E101.4.0", {"start": v(-10.3, 132.57) * mm, "end": v(-10.29, 132.58) * mm});
            skArc(sketch, "E101.4.1", {"start": v(-10.89, 132.54) * mm, "mid": v(-10.58, 132.46) * mm, "end": v(-10.29, 132.58) * mm});
            skLineSegment(sketch, "E101.4.2", {"start": v(-12.84, 133.8) * mm, "end": v(-10.89, 132.54) * mm});
            skArc(sketch, "E101.4.3", {"start": v(-12.84, 133.8) * mm, "mid": v(-13.16, 133.87) * mm, "end": v(-13.46, 133.73) * mm});
            skArc(sketch, "E101.4.4", {"start": v(-13.46, 133.73) * mm, "mid": v(-13.47, 133.72) * mm, "end": v(-13.49, 133.7) * mm});
            skArc(sketch, "E101.4.5", {"start": v(-13.49, 133.7) * mm, "mid": v(-13.63, 133.4) * mm, "end": v(-13.55, 133.08) * mm});
            skLineSegment(sketch, "E101.4.6", {"start": v(-13.55, 133.08) * mm, "end": v(-12.3, 131.13) * mm});
            skArc(sketch, "E101.4.7", {"start": v(-12.34, 130.53) * mm, "mid": v(-12.21, 130.82) * mm, "end": v(-12.3, 131.13) * mm});
            skLineSegment(sketch, "E101.4.8", {"start": v(-12.32, 130.54) * mm, "end": v(-12.34, 130.53) * mm});
            skLineSegment(sketch, "E101.5.0", {"start": v(-12.32, 130.54) * mm, "end": v(-12.3, 130.56) * mm});
            skArc(sketch, "E101.5.1", {"start": v(-12.9, 130.41) * mm, "mid": v(-12.58, 130.39) * mm, "end": v(-12.3, 130.56) * mm});
            skLineSegment(sketch, "E101.5.2", {"start": v(-15.03, 131.32) * mm, "end": v(-12.9, 130.41) * mm});
            skArc(sketch, "E101.5.3", {"start": v(-15.03, 131.32) * mm, "mid": v(-15.37, 131.34) * mm, "end": v(-15.64, 131.14) * mm});
            skArc(sketch, "E101.5.4", {"start": v(-15.64, 131.14) * mm, "mid": v(-15.65, 131.13) * mm, "end": v(-15.66, 131.11) * mm});
            skArc(sketch, "E101.5.5", {"start": v(-15.66, 131.11) * mm, "mid": v(-15.75, 130.8) * mm, "end": v(-15.61, 130.49) * mm});
            skLineSegment(sketch, "E101.5.6", {"start": v(-15.61, 130.49) * mm, "end": v(-14.03, 128.78) * mm});
            skArc(sketch, "E101.5.7", {"start": v(-13.97, 128.18) * mm, "mid": v(-13.9, 128.5) * mm, "end": v(-14.03, 128.78) * mm});
            skLineSegment(sketch, "E101.5.8", {"start": v(-13.96, 128.2) * mm, "end": v(-13.97, 128.18) * mm});
            skLineSegment(sketch, "E101.6.0", {"start": v(-13.96, 128.2) * mm, "end": v(-13.95, 128.22) * mm});
            skArc(sketch, "E101.6.1", {"start": v(-14.5, 127.97) * mm, "mid": v(-14.19, 128) * mm, "end": v(-13.95, 128.22) * mm});
            skLineSegment(sketch, "E101.6.2", {"start": v(-16.77, 128.5) * mm, "end": v(-14.5, 127.97) * mm});
            skArc(sketch, "E101.6.3", {"start": v(-16.77, 128.5) * mm, "mid": v(-17.1, 128.45) * mm, "end": v(-17.33, 128.22) * mm});
            skArc(sketch, "E101.6.4", {"start": v(-17.33, 128.22) * mm, "mid": v(-17.34, 128.2) * mm, "end": v(-17.35, 128.18) * mm});
            skArc(sketch, "E101.6.5", {"start": v(-17.35, 128.18) * mm, "mid": v(-17.38, 127.85) * mm, "end": v(-17.2, 127.57) * mm});
            skLineSegment(sketch, "E101.6.6", {"start": v(-17.2, 127.57) * mm, "end": v(-15.34, 126.17) * mm});
            skArc(sketch, "E101.6.7", {"start": v(-15.18, 125.6) * mm, "mid": v(-15.16, 125.9) * mm, "end": v(-15.34, 126.17) * mm});
            skLineSegment(sketch, "E101.6.8", {"start": v(-15.17, 125.61) * mm, "end": v(-15.18, 125.6) * mm});
            skLineSegment(sketch, "E101.7.0", {"start": v(-15.17, 125.61) * mm, "end": v(-15.16, 125.63) * mm});
            skArc(sketch, "E101.7.1", {"start": v(-15.66, 125.3) * mm, "mid": v(-15.36, 125.38) * mm, "end": v(-15.16, 125.63) * mm});
            skLineSegment(sketch, "E101.7.2", {"start": v(-17.98, 125.4) * mm, "end": v(-15.66, 125.3) * mm});
            skArc(sketch, "E101.7.3", {"start": v(-17.98, 125.4) * mm, "mid": v(-18.3, 125.31) * mm, "end": v(-18.5, 125.04) * mm});
            skArc(sketch, "E101.7.4", {"start": v(-18.5, 125.04) * mm, "mid": v(-18.5, 125.02) * mm, "end": v(-18.5, 125) * mm});
            skArc(sketch, "E101.7.5", {"start": v(-18.5, 125) * mm, "mid": v(-18.47, 124.67) * mm, "end": v(-18.24, 124.43) * mm});
            skLineSegment(sketch, "E101.7.6", {"start": v(-18.24, 124.43) * mm, "end": v(-16.18, 123.37) * mm});
            skArc(sketch, "E101.7.7", {"start": v(-15.91, 122.83) * mm, "mid": v(-15.95, 123.14) * mm, "end": v(-16.18, 123.37) * mm});
            skLineSegment(sketch, "E101.7.8", {"start": v(-15.91, 122.85) * mm, "end": v(-15.91, 122.83) * mm});
            skLineSegment(sketch, "E101.8.0", {"start": v(-15.91, 122.85) * mm, "end": v(-15.9, 122.87) * mm});
            skArc(sketch, "E101.8.1", {"start": v(-16.34, 122.45) * mm, "mid": v(-16.05, 122.59) * mm, "end": v(-15.9, 122.87) * mm});
            skLineSegment(sketch, "E101.8.2", {"start": v(-18.64, 122.16) * mm, "end": v(-16.34, 122.45) * mm});
            skArc(sketch, "E101.8.3", {"start": v(-18.64, 122.16) * mm, "mid": v(-18.94, 122.01) * mm, "end": v(-19.08, 121.7) * mm});
            skArc(sketch, "E101.8.4", {"start": v(-19.08, 121.7) * mm, "mid": v(-19.08, 121.7) * mm, "end": v(-19.08, 121.67) * mm});
            skArc(sketch, "E101.8.5", {"start": v(-19.08, 121.67) * mm, "mid": v(-19, 121.35) * mm, "end": v(-18.73, 121.15) * mm});
            skLineSegment(sketch, "E101.8.6", {"start": v(-18.73, 121.15) * mm, "end": v(-16.51, 120.47) * mm});
            skArc(sketch, "E101.8.7", {"start": v(-16.16, 119.98) * mm, "mid": v(-16.25, 120.28) * mm, "end": v(-16.51, 120.47) * mm});
            skLineSegment(sketch, "E101.8.8", {"start": v(-16.16, 120) * mm, "end": v(-16.16, 119.98) * mm});
            skLineSegment(sketch, "E101.9.0", {"start": v(-16.16, 120) * mm, "end": v(-16.16, 120.02) * mm});
            skArc(sketch, "E101.9.1", {"start": v(-16.51, 119.53) * mm, "mid": v(-16.25, 119.72) * mm, "end": v(-16.16, 120.02) * mm});
            skLineSegment(sketch, "E101.9.2", {"start": v(-18.73, 118.85) * mm, "end": v(-16.51, 119.53) * mm});
            skArc(sketch, "E101.9.3", {"start": v(-18.73, 118.85) * mm, "mid": v(-19, 118.65) * mm, "end": v(-19.08, 118.33) * mm});
            skArc(sketch, "E101.9.4", {"start": v(-19.08, 118.33) * mm, "mid": v(-19.08, 118.3) * mm, "end": v(-19.08, 118.3) * mm});
            skArc(sketch, "E101.9.5", {"start": v(-19.08, 118.3) * mm, "mid": v(-18.94, 117.99) * mm, "end": v(-18.64, 117.84) * mm});
            skLineSegment(sketch, "E101.9.6", {"start": v(-18.64, 117.84) * mm, "end": v(-16.34, 117.55) * mm});
            skArc(sketch, "E101.9.7", {"start": v(-15.9, 117.13) * mm, "mid": v(-16.05, 117.41) * mm, "end": v(-16.34, 117.55) * mm});
            skLineSegment(sketch, "E101.9.8", {"start": v(-15.91, 117.15) * mm, "end": v(-15.9, 117.13) * mm});
            skLineSegment(sketch, "E101.10.0", {"start": v(-15.91, 117.15) * mm, "end": v(-15.91, 117.17) * mm});
            skArc(sketch, "E101.10.1", {"start": v(-16.18, 116.63) * mm, "mid": v(-15.95, 116.86) * mm, "end": v(-15.91, 117.17) * mm});
            skLineSegment(sketch, "E101.10.2", {"start": v(-18.24, 115.57) * mm, "end": v(-16.18, 116.63) * mm});
            skArc(sketch, "E101.10.3", {"start": v(-18.24, 115.57) * mm, "mid": v(-18.47, 115.33) * mm, "end": v(-18.5, 115) * mm});
            skArc(sketch, "E101.10.4", {"start": v(-18.5, 115) * mm, "mid": v(-18.5, 114.98) * mm, "end": v(-18.5, 114.96) * mm});
            skArc(sketch, "E101.10.5", {"start": v(-18.5, 114.96) * mm, "mid": v(-18.3, 114.69) * mm, "end": v(-17.98, 114.6) * mm});
            skLineSegment(sketch, "E101.10.6", {"start": v(-17.98, 114.6) * mm, "end": v(-15.66, 114.7) * mm});
            skArc(sketch, "E101.10.7", {"start": v(-15.16, 114.37) * mm, "mid": v(-15.36, 114.62) * mm, "end": v(-15.66, 114.7) * mm});
            skLineSegment(sketch, "E101.10.8", {"start": v(-15.17, 114.39) * mm, "end": v(-15.16, 114.37) * mm});
            skLineSegment(sketch, "E101.11.0", {"start": v(-15.17, 114.39) * mm, "end": v(-15.18, 114.4) * mm});
            skArc(sketch, "E101.11.1", {"start": v(-15.34, 113.83) * mm, "mid": v(-15.16, 114.1) * mm, "end": v(-15.18, 114.4) * mm});
            skLineSegment(sketch, "E101.11.2", {"start": v(-17.2, 112.43) * mm, "end": v(-15.34, 113.83) * mm});
            skArc(sketch, "E101.11.3", {"start": v(-17.2, 112.43) * mm, "mid": v(-17.38, 112.15) * mm, "end": v(-17.35, 111.82) * mm});
            skArc(sketch, "E101.11.4", {"start": v(-17.35, 111.82) * mm, "mid": v(-17.34, 111.8) * mm, "end": v(-17.33, 111.78) * mm});
            skArc(sketch, "E101.11.5", {"start": v(-17.33, 111.78) * mm, "mid": v(-17.1, 111.55) * mm, "end": v(-16.77, 111.5) * mm});
            skLineSegment(sketch, "E101.11.6", {"start": v(-16.77, 111.5) * mm, "end": v(-14.5, 112.03) * mm});
            skArc(sketch, "E101.11.7", {"start": v(-13.95, 111.78) * mm, "mid": v(-14.19, 112) * mm, "end": v(-14.5, 112.03) * mm});
            skLineSegment(sketch, "E101.11.8", {"start": v(-13.96, 111.8) * mm, "end": v(-13.95, 111.78) * mm});
            skLineSegment(sketch, "E101.12.0", {"start": v(-13.96, 111.8) * mm, "end": v(-13.97, 111.82) * mm});
            skArc(sketch, "E101.12.1", {"start": v(-14.03, 111.22) * mm, "mid": v(-13.9, 111.5) * mm, "end": v(-13.97, 111.82) * mm});
            skLineSegment(sketch, "E101.12.2", {"start": v(-15.61, 109.51) * mm, "end": v(-14.03, 111.22) * mm});
            skArc(sketch, "E101.12.3", {"start": v(-15.61, 109.51) * mm, "mid": v(-15.75, 109.2) * mm, "end": v(-15.66, 108.89) * mm});
            skArc(sketch, "E101.12.4", {"start": v(-15.66, 108.89) * mm, "mid": v(-15.65, 108.87) * mm, "end": v(-15.64, 108.86) * mm});
            skArc(sketch, "E101.12.5", {"start": v(-15.64, 108.86) * mm, "mid": v(-15.37, 108.66) * mm, "end": v(-15.03, 108.68) * mm});
            skLineSegment(sketch, "E101.12.6", {"start": v(-15.03, 108.68) * mm, "end": v(-12.9, 109.59) * mm});
            skArc(sketch, "E101.12.7", {"start": v(-12.3, 109.44) * mm, "mid": v(-12.58, 109.61) * mm, "end": v(-12.9, 109.59) * mm});
            skLineSegment(sketch, "E101.12.8", {"start": v(-12.32, 109.46) * mm, "end": v(-12.3, 109.44) * mm});
            skLineSegment(sketch, "E101.13.0", {"start": v(-12.32, 109.46) * mm, "end": v(-12.34, 109.47) * mm});
            skArc(sketch, "E101.13.1", {"start": v(-12.3, 108.87) * mm, "mid": v(-12.21, 109.18) * mm, "end": v(-12.34, 109.47) * mm});
            skLineSegment(sketch, "E101.13.2", {"start": v(-13.55, 106.92) * mm, "end": v(-12.3, 108.87) * mm});
            skArc(sketch, "E101.13.3", {"start": v(-13.55, 106.92) * mm, "mid": v(-13.63, 106.6) * mm, "end": v(-13.49, 106.3) * mm});
            skArc(sketch, "E101.13.4", {"start": v(-13.49, 106.3) * mm, "mid": v(-13.47, 106.28) * mm, "end": v(-13.46, 106.27) * mm});
            skArc(sketch, "E101.13.5", {"start": v(-13.46, 106.27) * mm, "mid": v(-13.16, 106.13) * mm, "end": v(-12.84, 106.2) * mm});
            skLineSegment(sketch, "E101.13.6", {"start": v(-12.84, 106.2) * mm, "end": v(-10.89, 107.46) * mm});
            skArc(sketch, "E101.13.7", {"start": v(-10.29, 107.42) * mm, "mid": v(-10.58, 107.54) * mm, "end": v(-10.89, 107.46) * mm});
            skLineSegment(sketch, "E101.13.8", {"start": v(-10.3, 107.43) * mm, "end": v(-10.29, 107.42) * mm});
            skLineSegment(sketch, "E101.14.0", {"start": v(-10.3, 107.43) * mm, "end": v(-10.32, 107.45) * mm});
            skArc(sketch, "E101.14.1", {"start": v(-10.17, 106.86) * mm, "mid": v(-10.14, 107.18) * mm, "end": v(-10.32, 107.45) * mm});
            skLineSegment(sketch, "E101.14.2", {"start": v(-11.07, 104.72) * mm, "end": v(-10.17, 106.86) * mm});
            skArc(sketch, "E101.14.3", {"start": v(-11.07, 104.72) * mm, "mid": v(-11.1, 104.4) * mm, "end": v(-10.9, 104.12) * mm});
            skArc(sketch, "E101.14.4", {"start": v(-10.9, 104.12) * mm, "mid": v(-10.88, 104.1) * mm, "end": v(-10.87, 104.1) * mm});
            skArc(sketch, "E101.14.5", {"start": v(-10.87, 104.1) * mm, "mid": v(-10.55, 104) * mm, "end": v(-10.24, 104.14) * mm});
            skLineSegment(sketch, "E101.14.6", {"start": v(-10.24, 104.14) * mm, "end": v(-8.54, 105.72) * mm});
            skArc(sketch, "E101.14.7", {"start": v(-7.94, 105.78) * mm, "mid": v(-8.25, 105.85) * mm, "end": v(-8.54, 105.72) * mm});
            skLineSegment(sketch, "E101.14.8", {"start": v(-7.96, 105.8) * mm, "end": v(-7.94, 105.78) * mm});
            skLineSegment(sketch, "E101.15.0", {"start": v(-7.96, 105.8) * mm, "end": v(-7.98, 105.8) * mm});
            skArc(sketch, "E101.15.1", {"start": v(-7.73, 105.25) * mm, "mid": v(-7.76, 105.57) * mm, "end": v(-7.98, 105.8) * mm});
            skLineSegment(sketch, "E101.15.2", {"start": v(-8.25, 103) * mm, "end": v(-7.73, 105.25) * mm});
            skArc(sketch, "E101.15.3", {"start": v(-8.25, 103) * mm, "mid": v(-8.2, 102.66) * mm, "end": v(-7.97, 102.43) * mm});
            skArc(sketch, "E101.15.4", {"start": v(-7.97, 102.43) * mm, "mid": v(-7.95, 102.42) * mm, "end": v(-7.94, 102.4) * mm});
            skArc(sketch, "E101.15.5", {"start": v(-7.94, 102.4) * mm, "mid": v(-7.6, 102.38) * mm, "end": v(-7.33, 102.56) * mm});
            skLineSegment(sketch, "E101.15.6", {"start": v(-7.33, 102.56) * mm, "end": v(-5.93, 104.41) * mm});
            skArc(sketch, "E101.15.7", {"start": v(-5.35, 104.58) * mm, "mid": v(-5.67, 104.6) * mm, "end": v(-5.93, 104.41) * mm});
            skLineSegment(sketch, "E101.15.8", {"start": v(-5.37, 104.59) * mm, "end": v(-5.35, 104.58) * mm});
            skLineSegment(sketch, "E101.16.0", {"start": v(-5.37, 104.59) * mm, "end": v(-5.39, 104.6) * mm});
            skArc(sketch, "E101.16.1", {"start": v(-5.05, 104.1) * mm, "mid": v(-5.13, 104.4) * mm, "end": v(-5.39, 104.6) * mm});
            skLineSegment(sketch, "E101.16.2", {"start": v(-5.16, 101.77) * mm, "end": v(-5.05, 104.1) * mm});
            skArc(sketch, "E101.16.3", {"start": v(-5.16, 101.77) * mm, "mid": v(-5.07, 101.45) * mm, "end": v(-4.8, 101.27) * mm});
            skArc(sketch, "E101.16.4", {"start": v(-4.8, 101.27) * mm, "mid": v(-4.78, 101.26) * mm, "end": v(-4.76, 101.26) * mm});
            skArc(sketch, "E101.16.5", {"start": v(-4.76, 101.26) * mm, "mid": v(-4.43, 101.28) * mm, "end": v(-4.19, 101.51) * mm});
            skLineSegment(sketch, "E101.16.6", {"start": v(-4.19, 101.51) * mm, "end": v(-3.13, 103.58) * mm});
            skArc(sketch, "E101.16.7", {"start": v(-2.58, 103.84) * mm, "mid": v(-2.9, 103.8) * mm, "end": v(-3.13, 103.58) * mm});
            skLineSegment(sketch, "E101.16.8", {"start": v(-2.6, 103.85) * mm, "end": v(-2.58, 103.84) * mm});
            skLineSegment(sketch, "E101.17.0", {"start": v(-2.6, 103.85) * mm, "end": v(-2.62, 103.85) * mm});
            skArc(sketch, "E101.17.1", {"start": v(-2.2, 103.42) * mm, "mid": v(-2.34, 103.7) * mm, "end": v(-2.62, 103.85) * mm});
            skLineSegment(sketch, "E101.17.2", {"start": v(-1.92, 101.11) * mm, "end": v(-2.2, 103.42) * mm});
            skArc(sketch, "E101.17.3", {"start": v(-1.92, 101.11) * mm, "mid": v(-1.77, 100.81) * mm, "end": v(-1.47, 100.68) * mm});
            skArc(sketch, "E101.17.4", {"start": v(-1.47, 100.68) * mm, "mid": v(-1.45, 100.67) * mm, "end": v(-1.43, 100.67) * mm});
            skArc(sketch, "E101.17.5", {"start": v(-1.43, 100.67) * mm, "mid": v(-1.1, 100.76) * mm, "end": v(-0.9, 101.02) * mm});
            skLineSegment(sketch, "E101.17.6", {"start": v(-0.9, 101.02) * mm, "end": v(-0.22, 103.24) * mm});
            skArc(sketch, "E101.17.7", {"start": v(0.26, 103.6) * mm, "mid": v(-0.04, 103.5) * mm, "end": v(-0.22, 103.24) * mm});
            skLineSegment(sketch, "E101.17.8", {"start": v(0.24, 103.6) * mm, "end": v(0.26, 103.6) * mm});
            skLineSegment(sketch, "E101.18.0", {"start": v(0.24, 103.6) * mm, "end": v(0.22, 103.6) * mm});
            skArc(sketch, "E101.18.1", {"start": v(0.71, 103.24) * mm, "mid": v(0.53, 103.5) * mm, "end": v(0.22, 103.6) * mm});
            skLineSegment(sketch, "E101.18.2", {"start": v(1.4, 101.02) * mm, "end": v(0.71, 103.24) * mm});
            skArc(sketch, "E101.18.3", {"start": v(1.4, 101.02) * mm, "mid": v(1.6, 100.76) * mm, "end": v(1.92, 100.67) * mm});
            skArc(sketch, "E101.18.4", {"start": v(1.92, 100.67) * mm, "mid": v(1.93, 100.67) * mm, "end": v(1.95, 100.68) * mm});
            skArc(sketch, "E101.18.5", {"start": v(1.95, 100.68) * mm, "mid": v(2.26, 100.81) * mm, "end": v(2.4, 101.11) * mm});
            skLineSegment(sketch, "E101.18.6", {"start": v(2.4, 101.11) * mm, "end": v(2.7, 103.42) * mm});
            skArc(sketch, "E101.18.7", {"start": v(3.11, 103.85) * mm, "mid": v(2.83, 103.7) * mm, "end": v(2.7, 103.42) * mm});
            skLineSegment(sketch, "E101.18.8", {"start": v(3.1, 103.85) * mm, "end": v(3.11, 103.85) * mm});
            skLineSegment(sketch, "E101.19.0", {"start": v(3.1, 103.85) * mm, "end": v(3.07, 103.84) * mm});
            skArc(sketch, "E101.19.1", {"start": v(3.62, 103.58) * mm, "mid": v(3.39, 103.8) * mm, "end": v(3.07, 103.84) * mm});
            skLineSegment(sketch, "E101.19.2", {"start": v(4.67, 101.51) * mm, "end": v(3.62, 103.58) * mm});
            skArc(sketch, "E101.19.3", {"start": v(4.67, 101.51) * mm, "mid": v(4.92, 101.28) * mm, "end": v(5.25, 101.26) * mm});
            skArc(sketch, "E101.19.4", {"start": v(5.25, 101.26) * mm, "mid": v(5.27, 101.26) * mm, "end": v(5.28, 101.27) * mm});
            skArc(sketch, "E101.19.5", {"start": v(5.28, 101.27) * mm, "mid": v(5.56, 101.45) * mm, "end": v(5.65, 101.77) * mm});
            skLineSegment(sketch, "E101.19.6", {"start": v(5.65, 101.77) * mm, "end": v(5.53, 104.1) * mm});
            skArc(sketch, "E101.19.7", {"start": v(5.87, 104.6) * mm, "mid": v(5.62, 104.4) * mm, "end": v(5.53, 104.1) * mm});
            skLineSegment(sketch, "E101.19.8", {"start": v(5.85, 104.59) * mm, "end": v(5.87, 104.6) * mm});
            skLineSegment(sketch, "E101.20.0", {"start": v(5.85, 104.59) * mm, "end": v(5.84, 104.58) * mm});
            skArc(sketch, "E101.20.1", {"start": v(6.42, 104.41) * mm, "mid": v(6.15, 104.6) * mm, "end": v(5.84, 104.58) * mm});
            skLineSegment(sketch, "E101.20.2", {"start": v(7.82, 102.56) * mm, "end": v(6.42, 104.41) * mm});
            skArc(sketch, "E101.20.3", {"start": v(7.82, 102.56) * mm, "mid": v(8.1, 102.38) * mm, "end": v(8.43, 102.4) * mm});
            skArc(sketch, "E101.20.4", {"start": v(8.43, 102.4) * mm, "mid": v(8.44, 102.42) * mm, "end": v(8.46, 102.43) * mm});
            skArc(sketch, "E101.20.5", {"start": v(8.46, 102.43) * mm, "mid": v(8.7, 102.66) * mm, "end": v(8.74, 103) * mm});
            skLineSegment(sketch, "E101.20.6", {"start": v(8.74, 103) * mm, "end": v(8.22, 105.25) * mm});
            skArc(sketch, "E101.20.7", {"start": v(8.46, 105.8) * mm, "mid": v(8.25, 105.57) * mm, "end": v(8.22, 105.25) * mm});
            skLineSegment(sketch, "E101.20.8", {"start": v(8.45, 105.8) * mm, "end": v(8.46, 105.8) * mm});
            skLineSegment(sketch, "E101.21.0", {"start": v(8.45, 105.8) * mm, "end": v(8.43, 105.78) * mm});
            skArc(sketch, "E101.21.1", {"start": v(9.03, 105.72) * mm, "mid": v(8.74, 105.85) * mm, "end": v(8.43, 105.78) * mm});
            skLineSegment(sketch, "E101.21.2", {"start": v(10.73, 104.14) * mm, "end": v(9.03, 105.72) * mm});
            skArc(sketch, "E101.21.3", {"start": v(10.73, 104.14) * mm, "mid": v(11.04, 104) * mm, "end": v(11.36, 104.1) * mm});
            skArc(sketch, "E101.21.4", {"start": v(11.36, 104.1) * mm, "mid": v(11.37, 104.1) * mm, "end": v(11.39, 104.12) * mm});
            skArc(sketch, "E101.21.5", {"start": v(11.39, 104.12) * mm, "mid": v(11.58, 104.4) * mm, "end": v(11.56, 104.72) * mm});
            skLineSegment(sketch, "E101.21.6", {"start": v(11.56, 104.72) * mm, "end": v(10.66, 106.86) * mm});
            skArc(sketch, "E101.21.7", {"start": v(10.8, 107.45) * mm, "mid": v(10.63, 107.18) * mm, "end": v(10.66, 106.86) * mm});
            skLineSegment(sketch, "E101.21.8", {"start": v(10.79, 107.43) * mm, "end": v(10.8, 107.45) * mm});
            skLineSegment(sketch, "E101.22.0", {"start": v(10.79, 107.43) * mm, "end": v(10.77, 107.42) * mm});
            skArc(sketch, "E101.22.1", {"start": v(11.37, 107.46) * mm, "mid": v(11.07, 107.54) * mm, "end": v(10.77, 107.42) * mm});
            skLineSegment(sketch, "E101.22.2", {"start": v(13.32, 106.2) * mm, "end": v(11.37, 107.46) * mm});
            skArc(sketch, "E101.22.3", {"start": v(13.32, 106.2) * mm, "mid": v(13.65, 106.13) * mm, "end": v(13.95, 106.27) * mm});
            skArc(sketch, "E101.22.4", {"start": v(13.95, 106.27) * mm, "mid": v(13.96, 106.28) * mm, "end": v(13.97, 106.3) * mm});
            skArc(sketch, "E101.22.5", {"start": v(13.97, 106.3) * mm, "mid": v(14.12, 106.6) * mm, "end": v(14.04, 106.92) * mm});
            skLineSegment(sketch, "E101.22.6", {"start": v(14.04, 106.92) * mm, "end": v(12.78, 108.87) * mm});
            skArc(sketch, "E101.22.7", {"start": v(12.82, 109.47) * mm, "mid": v(12.7, 109.18) * mm, "end": v(12.78, 108.87) * mm});
            skLineSegment(sketch, "E101.22.8", {"start": v(12.81, 109.46) * mm, "end": v(12.82, 109.47) * mm});
            skLineSegment(sketch, "E101.23.0", {"start": v(12.81, 109.46) * mm, "end": v(12.8, 109.44) * mm});
            skArc(sketch, "E101.23.1", {"start": v(13.38, 109.59) * mm, "mid": v(13.07, 109.61) * mm, "end": v(12.8, 109.44) * mm});
            skLineSegment(sketch, "E101.23.2", {"start": v(15.52, 108.68) * mm, "end": v(13.38, 109.59) * mm});
            skArc(sketch, "E101.23.3", {"start": v(15.52, 108.68) * mm, "mid": v(15.85, 108.66) * mm, "end": v(16.12, 108.86) * mm});
            skArc(sketch, "E101.23.4", {"start": v(16.12, 108.86) * mm, "mid": v(16.14, 108.87) * mm, "end": v(16.15, 108.89) * mm});
            skArc(sketch, "E101.23.5", {"start": v(16.15, 108.89) * mm, "mid": v(16.24, 109.2) * mm, "end": v(16.1, 109.51) * mm});
            skLineSegment(sketch, "E101.23.6", {"start": v(16.1, 109.51) * mm, "end": v(14.52, 111.22) * mm});
            skArc(sketch, "E101.23.7", {"start": v(14.46, 111.82) * mm, "mid": v(14.4, 111.5) * mm, "end": v(14.52, 111.22) * mm});
            skLineSegment(sketch, "E101.23.8", {"start": v(14.45, 111.8) * mm, "end": v(14.46, 111.82) * mm});
            skLineSegment(sketch, "E101.24.0", {"start": v(14.45, 111.8) * mm, "end": v(14.44, 111.78) * mm});
            skArc(sketch, "E101.24.1", {"start": v(15, 112.03) * mm, "mid": v(14.67, 112) * mm, "end": v(14.44, 111.78) * mm});
            skLineSegment(sketch, "E101.24.2", {"start": v(17.25, 111.5) * mm, "end": v(15, 112.03) * mm});
            skArc(sketch, "E101.24.3", {"start": v(17.25, 111.5) * mm, "mid": v(17.58, 111.55) * mm, "end": v(17.82, 111.78) * mm});
            skArc(sketch, "E101.24.4", {"start": v(17.82, 111.78) * mm, "mid": v(17.83, 111.8) * mm, "end": v(17.83, 111.82) * mm});
            skArc(sketch, "E101.24.5", {"start": v(17.83, 111.82) * mm, "mid": v(17.87, 112.15) * mm, "end": v(17.68, 112.43) * mm});
            skLineSegment(sketch, "E101.24.6", {"start": v(17.68, 112.43) * mm, "end": v(15.83, 113.83) * mm});
            skArc(sketch, "E101.24.7", {"start": v(15.67, 114.4) * mm, "mid": v(15.65, 114.1) * mm, "end": v(15.83, 113.83) * mm});
            skLineSegment(sketch, "E101.24.8", {"start": v(15.66, 114.39) * mm, "end": v(15.67, 114.4) * mm});
            skLineSegment(sketch, "E101.25.0", {"start": v(15.66, 114.39) * mm, "end": v(15.65, 114.37) * mm});
            skArc(sketch, "E101.25.1", {"start": v(16.15, 114.7) * mm, "mid": v(15.84, 114.62) * mm, "end": v(15.65, 114.37) * mm});
            skLineSegment(sketch, "E101.25.2", {"start": v(18.47, 114.6) * mm, "end": v(16.15, 114.7) * mm});
            skArc(sketch, "E101.25.3", {"start": v(18.47, 114.6) * mm, "mid": v(18.79, 114.69) * mm, "end": v(18.98, 114.96) * mm});
            skArc(sketch, "E101.25.4", {"start": v(18.98, 114.96) * mm, "mid": v(18.98, 114.98) * mm, "end": v(18.99, 115) * mm});
            skArc(sketch, "E101.25.5", {"start": v(18.99, 115) * mm, "mid": v(18.96, 115.33) * mm, "end": v(18.73, 115.57) * mm});
            skLineSegment(sketch, "E101.25.6", {"start": v(18.73, 115.57) * mm, "end": v(16.67, 116.63) * mm});
            skArc(sketch, "E101.25.7", {"start": v(16.4, 117.17) * mm, "mid": v(16.44, 116.86) * mm, "end": v(16.67, 116.63) * mm});
            skLineSegment(sketch, "E101.25.8", {"start": v(16.4, 117.15) * mm, "end": v(16.4, 117.17) * mm});
            skLineSegment(sketch, "E101.26.0", {"start": v(16.4, 117.15) * mm, "end": v(16.4, 117.13) * mm});
            skArc(sketch, "E101.26.1", {"start": v(16.83, 117.55) * mm, "mid": v(16.54, 117.41) * mm, "end": v(16.4, 117.13) * mm});
            skLineSegment(sketch, "E101.26.2", {"start": v(19.13, 117.84) * mm, "end": v(16.83, 117.55) * mm});
            skArc(sketch, "E101.26.3", {"start": v(19.13, 117.84) * mm, "mid": v(19.43, 117.99) * mm, "end": v(19.57, 118.3) * mm});
            skArc(sketch, "E101.26.4", {"start": v(19.57, 118.3) * mm, "mid": v(19.57, 118.3) * mm, "end": v(19.57, 118.33) * mm});
            skArc(sketch, "E101.26.5", {"start": v(19.57, 118.33) * mm, "mid": v(19.49, 118.65) * mm, "end": v(19.22, 118.85) * mm});
            skLineSegment(sketch, "E101.26.6", {"start": v(19.22, 118.85) * mm, "end": v(17, 119.53) * mm});
            skArc(sketch, "E101.26.7", {"start": v(16.65, 120.02) * mm, "mid": v(16.74, 119.72) * mm, "end": v(17, 119.53) * mm});
            skLineSegment(sketch, "E101.26.8", {"start": v(16.65, 120) * mm, "end": v(16.65, 120.02) * mm});
            skLineSegment(sketch, "E101.27.0", {"start": v(16.65, 120) * mm, "end": v(16.65, 119.98) * mm});
            skArc(sketch, "E101.27.1", {"start": v(17, 120.47) * mm, "mid": v(16.74, 120.28) * mm, "end": v(16.65, 119.98) * mm});
            skLineSegment(sketch, "E101.27.2", {"start": v(19.22, 121.15) * mm, "end": v(17, 120.47) * mm});
            skArc(sketch, "E101.27.3", {"start": v(19.22, 121.15) * mm, "mid": v(19.49, 121.35) * mm, "end": v(19.57, 121.67) * mm});
            skArc(sketch, "E101.27.4", {"start": v(19.57, 121.67) * mm, "mid": v(19.57, 121.7) * mm, "end": v(19.57, 121.7) * mm});
            skArc(sketch, "E101.27.5", {"start": v(19.57, 121.7) * mm, "mid": v(19.43, 122.01) * mm, "end": v(19.13, 122.16) * mm});
            skLineSegment(sketch, "E101.27.6", {"start": v(19.13, 122.16) * mm, "end": v(16.83, 122.45) * mm});
            skArc(sketch, "E101.27.7", {"start": v(16.4, 122.87) * mm, "mid": v(16.54, 122.59) * mm, "end": v(16.83, 122.45) * mm});
            skLineSegment(sketch, "E101.27.8", {"start": v(16.4, 122.85) * mm, "end": v(16.4, 122.87) * mm});
            skLineSegment(sketch, "E101.28.0", {"start": v(16.4, 122.85) * mm, "end": v(16.4, 122.83) * mm});
            skArc(sketch, "E101.28.1", {"start": v(16.67, 123.37) * mm, "mid": v(16.44, 123.14) * mm, "end": v(16.4, 122.83) * mm});
            skLineSegment(sketch, "E101.28.2", {"start": v(18.73, 124.43) * mm, "end": v(16.67, 123.37) * mm});
            skArc(sketch, "E101.28.3", {"start": v(18.73, 124.43) * mm, "mid": v(18.96, 124.67) * mm, "end": v(18.99, 125) * mm});
            skArc(sketch, "E101.28.4", {"start": v(18.99, 125) * mm, "mid": v(18.98, 125.02) * mm, "end": v(18.98, 125.04) * mm});
            skArc(sketch, "E101.28.5", {"start": v(18.98, 125.04) * mm, "mid": v(18.79, 125.31) * mm, "end": v(18.47, 125.4) * mm});
            skLineSegment(sketch, "E101.28.6", {"start": v(18.47, 125.4) * mm, "end": v(16.15, 125.3) * mm});
            skArc(sketch, "E101.28.7", {"start": v(15.65, 125.63) * mm, "mid": v(15.84, 125.38) * mm, "end": v(16.15, 125.3) * mm});
            skLineSegment(sketch, "E101.28.8", {"start": v(15.66, 125.61) * mm, "end": v(15.65, 125.63) * mm});
            skLineSegment(sketch, "E101.29.0", {"start": v(15.66, 125.61) * mm, "end": v(15.67, 125.6) * mm});
            skArc(sketch, "E101.29.1", {"start": v(15.83, 126.17) * mm, "mid": v(15.65, 125.9) * mm, "end": v(15.67, 125.6) * mm});
            skLineSegment(sketch, "E101.29.2", {"start": v(17.68, 127.57) * mm, "end": v(15.83, 126.17) * mm});
            skArc(sketch, "E101.29.3", {"start": v(17.68, 127.57) * mm, "mid": v(17.87, 127.85) * mm, "end": v(17.83, 128.18) * mm});
            skArc(sketch, "E101.29.4", {"start": v(17.83, 128.18) * mm, "mid": v(17.83, 128.2) * mm, "end": v(17.82, 128.22) * mm});
            skArc(sketch, "E101.29.5", {"start": v(17.82, 128.22) * mm, "mid": v(17.58, 128.45) * mm, "end": v(17.25, 128.5) * mm});
            skLineSegment(sketch, "E101.29.6", {"start": v(17.25, 128.5) * mm, "end": v(15, 127.97) * mm});
            skArc(sketch, "E101.29.7", {"start": v(14.44, 128.22) * mm, "mid": v(14.67, 128) * mm, "end": v(15, 127.97) * mm});
            skLineSegment(sketch, "E101.29.8", {"start": v(14.45, 128.2) * mm, "end": v(14.44, 128.22) * mm});
            skLineSegment(sketch, "E101.30.0", {"start": v(14.45, 128.2) * mm, "end": v(14.46, 128.18) * mm});
            skArc(sketch, "E101.30.1", {"start": v(14.52, 128.78) * mm, "mid": v(14.4, 128.5) * mm, "end": v(14.46, 128.18) * mm});
            skLineSegment(sketch, "E101.30.2", {"start": v(16.1, 130.49) * mm, "end": v(14.52, 128.78) * mm});
            skArc(sketch, "E101.30.3", {"start": v(16.1, 130.49) * mm, "mid": v(16.24, 130.8) * mm, "end": v(16.15, 131.11) * mm});
            skArc(sketch, "E101.30.4", {"start": v(16.15, 131.11) * mm, "mid": v(16.14, 131.13) * mm, "end": v(16.12, 131.14) * mm});
            skArc(sketch, "E101.30.5", {"start": v(16.12, 131.14) * mm, "mid": v(15.85, 131.34) * mm, "end": v(15.52, 131.32) * mm});
            skLineSegment(sketch, "E101.30.6", {"start": v(15.52, 131.32) * mm, "end": v(13.38, 130.41) * mm});
            skArc(sketch, "E101.30.7", {"start": v(12.8, 130.56) * mm, "mid": v(13.07, 130.39) * mm, "end": v(13.38, 130.41) * mm});
            skLineSegment(sketch, "E101.30.8", {"start": v(12.81, 130.54) * mm, "end": v(12.8, 130.56) * mm});
            skLineSegment(sketch, "E101.31.0", {"start": v(12.81, 130.54) * mm, "end": v(12.82, 130.53) * mm});
            skArc(sketch, "E101.31.1", {"start": v(12.78, 131.13) * mm, "mid": v(12.7, 130.82) * mm, "end": v(12.82, 130.53) * mm});
            skLineSegment(sketch, "E101.31.2", {"start": v(14.04, 133.08) * mm, "end": v(12.78, 131.13) * mm});
            skArc(sketch, "E101.31.3", {"start": v(14.04, 133.08) * mm, "mid": v(14.12, 133.4) * mm, "end": v(13.97, 133.7) * mm});
            skArc(sketch, "E101.31.4", {"start": v(13.97, 133.7) * mm, "mid": v(13.96, 133.72) * mm, "end": v(13.95, 133.73) * mm});
            skArc(sketch, "E101.31.5", {"start": v(13.95, 133.73) * mm, "mid": v(13.65, 133.87) * mm, "end": v(13.32, 133.8) * mm});
            skLineSegment(sketch, "E101.31.6", {"start": v(13.32, 133.8) * mm, "end": v(11.37, 132.54) * mm});
            skArc(sketch, "E101.31.7", {"start": v(10.77, 132.58) * mm, "mid": v(11.07, 132.46) * mm, "end": v(11.37, 132.54) * mm});
            skLineSegment(sketch, "E101.31.8", {"start": v(10.79, 132.57) * mm, "end": v(10.77, 132.58) * mm});
            skLineSegment(sketch, "E101.32.0", {"start": v(10.79, 132.57) * mm, "end": v(10.8, 132.55) * mm});
            skArc(sketch, "E101.32.1", {"start": v(10.66, 133.14) * mm, "mid": v(10.63, 132.82) * mm, "end": v(10.8, 132.55) * mm});
            skLineSegment(sketch, "E101.32.2", {"start": v(11.56, 135.28) * mm, "end": v(10.66, 133.14) * mm});
            skArc(sketch, "E101.32.3", {"start": v(11.56, 135.28) * mm, "mid": v(11.58, 135.6) * mm, "end": v(11.39, 135.88) * mm});
            skArc(sketch, "E101.32.4", {"start": v(11.39, 135.88) * mm, "mid": v(11.37, 135.9) * mm, "end": v(11.36, 135.9) * mm});
            skArc(sketch, "E101.32.5", {"start": v(11.36, 135.9) * mm, "mid": v(11.04, 136) * mm, "end": v(10.73, 135.86) * mm});
            skLineSegment(sketch, "E101.32.6", {"start": v(10.73, 135.86) * mm, "end": v(9.03, 134.28) * mm});
            skArc(sketch, "E101.32.7", {"start": v(8.43, 134.22) * mm, "mid": v(8.74, 134.15) * mm, "end": v(9.03, 134.28) * mm});
            skLineSegment(sketch, "E101.32.8", {"start": v(8.45, 134.2) * mm, "end": v(8.43, 134.22) * mm});
            skLineSegment(sketch, "E101.33.0", {"start": v(8.45, 134.2) * mm, "end": v(8.46, 134.2) * mm});
            skArc(sketch, "E101.33.1", {"start": v(8.22, 134.75) * mm, "mid": v(8.25, 134.43) * mm, "end": v(8.46, 134.2) * mm});
            skLineSegment(sketch, "E101.33.2", {"start": v(8.74, 137) * mm, "end": v(8.22, 134.75) * mm});
            skArc(sketch, "E101.33.3", {"start": v(8.74, 137) * mm, "mid": v(8.7, 137.34) * mm, "end": v(8.46, 137.57) * mm});
            skArc(sketch, "E101.33.4", {"start": v(8.46, 137.57) * mm, "mid": v(8.44, 137.58) * mm, "end": v(8.43, 137.6) * mm});
            skArc(sketch, "E101.33.5", {"start": v(8.43, 137.6) * mm, "mid": v(8.1, 137.62) * mm, "end": v(7.82, 137.44) * mm});
            skLineSegment(sketch, "E101.33.6", {"start": v(7.82, 137.44) * mm, "end": v(6.42, 135.59) * mm});
            skArc(sketch, "E101.33.7", {"start": v(5.84, 135.42) * mm, "mid": v(6.15, 135.4) * mm, "end": v(6.42, 135.59) * mm});
            skLineSegment(sketch, "E101.33.8", {"start": v(5.85, 135.41) * mm, "end": v(5.84, 135.42) * mm});
            skLineSegment(sketch, "E101.34.0", {"start": v(5.85, 135.41) * mm, "end": v(5.87, 135.4) * mm});
            skArc(sketch, "E101.34.1", {"start": v(5.53, 135.9) * mm, "mid": v(5.62, 135.6) * mm, "end": v(5.87, 135.4) * mm});
            skLineSegment(sketch, "E101.34.2", {"start": v(5.65, 138.23) * mm, "end": v(5.53, 135.9) * mm});
            skArc(sketch, "E101.34.3", {"start": v(5.65, 138.23) * mm, "mid": v(5.56, 138.55) * mm, "end": v(5.28, 138.73) * mm});
            skArc(sketch, "E101.34.4", {"start": v(5.28, 138.73) * mm, "mid": v(5.27, 138.74) * mm, "end": v(5.25, 138.74) * mm});
            skArc(sketch, "E101.34.5", {"start": v(5.25, 138.74) * mm, "mid": v(4.92, 138.72) * mm, "end": v(4.67, 138.49) * mm});
            skLineSegment(sketch, "E101.34.6", {"start": v(4.67, 138.49) * mm, "end": v(3.62, 136.42) * mm});
            skArc(sketch, "E101.34.7", {"start": v(3.07, 136.16) * mm, "mid": v(3.39, 136.2) * mm, "end": v(3.62, 136.42) * mm});
            skLineSegment(sketch, "E101.34.8", {"start": v(3.1, 136.15) * mm, "end": v(3.07, 136.16) * mm});
            skLineSegment(sketch, "E101.35.0", {"start": v(3.1, 136.15) * mm, "end": v(3.11, 136.15) * mm});
            skArc(sketch, "E101.35.1", {"start": v(2.7, 136.58) * mm, "mid": v(2.83, 136.3) * mm, "end": v(3.11, 136.15) * mm});
            skLineSegment(sketch, "E101.35.2", {"start": v(2.4, 138.89) * mm, "end": v(2.7, 136.58) * mm});
            skArc(sketch, "E101.35.3", {"start": v(2.4, 138.89) * mm, "mid": v(2.26, 139.19) * mm, "end": v(1.95, 139.32) * mm});
            skArc(sketch, "E101.35.4", {"start": v(1.95, 139.32) * mm, "mid": v(1.93, 139.33) * mm, "end": v(1.92, 139.33) * mm});
            skArc(sketch, "E101.35.5", {"start": v(1.92, 139.33) * mm, "mid": v(1.6, 139.24) * mm, "end": v(1.4, 138.98) * mm});
            skLineSegment(sketch, "E101.35.6", {"start": v(1.4, 138.98) * mm, "end": v(0.71, 136.76) * mm});
            skArc(sketch, "E101.35.7", {"start": v(0.22, 136.4) * mm, "mid": v(0.53, 136.5) * mm, "end": v(0.71, 136.76) * mm});
            skLineSegment(sketch, "E101.35.8", {"start": v(0.24, 136.4) * mm, "end": v(0.22, 136.4) * mm});
            skSolve(sketch);
        }
        {
            var Q0;
            Q0 = qSketchRegion(id + "F6", true);
            extrude(context, id + "F7", {"entities" : qUnion([Q0]), "depth" : 6 * mm});
        }
        {
            var Q0;
            Q0=makeQuery(id+"F7.opExtrude","CAP_FACE",FACE,{"disambiguationData":[OSD([sQuery(id+"F6.wireOp",EDGE,"E80"),sQuery(id+"F6.wireOp",EDGE,"E82")])],"isStart":false});
            var sketch = newSketch(context, id + "F8", { "sketchPlane" : qUnion([Q0])});
            skLineSegment(sketch, "E102.rect.bottom", {"start": v(84.24, 114) * mm, "end": v(-89.76, 114) * mm});
            skLineSegment(sketch, "E102.rect.top", {"start": v(90.24, 126) * mm, "end": v(-83.76, 126) * mm});
            skLineSegment(sketch, "E102.rect.left", {"start": v(90.24, 120) * mm, "end": v(90.24, 126) * mm});
            skLineSegment(sketch, "E102.rect.right", {"start": v(-89.76, 114) * mm, "end": v(-89.76, 120) * mm});
            skPoint(sketch, "E102.rect.middle", {"position": v(0.24, 120) * mm});
            skCircle(sketch, "E103", {"center": v(0.24, 120) * mm, "radius": 2.5 * mm});
            skLineSegment(sketch, "E104", {"start": v(-89.76, 120) * mm, "end": v(-83.76, 120) * mm});
            skLineSegment(sketch, "E105", {"start": v(-83.76, 120) * mm, "end": v(-83.76, 126) * mm});
            skLineSegment(sketch, "E106", {"start": v(90.24, 120) * mm, "end": v(84.24, 120) * mm});
            skPoint(sketch, "E106.endSnap0", {"position": v(90.24, 120) * mm});
            skLineSegment(sketch, "E107", {"start": v(84.24, 120) * mm, "end": v(84.24, 114) * mm});
            skPoint(sketch, "E108.orphan", {"position": v(-89.76, 126) * mm});
            skPoint(sketch, "E109.orphan", {"position": v(90.24, 114) * mm});
            skLineSegment(sketch, "E110", {"start": v(-89.76, 126) * mm, "end": v(90.24, 114) * mm, "construction": true});
            skLineSegment(sketch, "E111", {"start": v(0.24, 120) * mm, "end": v(-89.76, 120) * mm, "construction": true});
            skCircle(sketch, "E112", {"center": v(-71.76, 120) * mm, "radius": 2.5 * mm});
            skCircle(sketch, "E113", {"center": v(-35.76, 120) * mm, "radius": 2.5 * mm});
            skSolve(sketch);
        }
        {
            var Q0;
            Q0 = qSketchRegion(id + "F8", true);
            extrude(context, id + "F9", {"entities" : qUnion([Q0]), "depth" : 6 * mm});
        }
        {
            var Q0;
            Q0=makeQuery(id+"F9.opExtrude","SWEPT_FACE",FACE,{"disambiguationData":[OSD([sQuery(id+"F8.wireOp",EDGE,"E102.rect.right")])]});
            var sketch = newSketch(context, id + "F10", { "sketchPlane" : qUnion([Q0])});
            skLineSegment(sketch, "E114.bottom", {"start": v(-82, 114) * mm, "end": v(92, 114) * mm});
            skLineSegment(sketch, "E114.top", {"start": v(-88, 126) * mm, "end": v(86, 126) * mm});
            skLineSegment(sketch, "E114.left", {"start": v(-88, 120) * mm, "end": v(-88, 126) * mm});
            skLineSegment(sketch, "E114.right", {"start": v(92, 114) * mm, "end": v(92, 120) * mm});
            skLineSegment(sketch, "E115.top", {"start": v(-88, 120) * mm, "end": v(-82, 120) * mm});
            skLineSegment(sketch, "E115.right", {"start": v(-82, 114) * mm, "end": v(-82, 120) * mm});
            skLineSegment(sketch, "E116.top", {"start": v(92, 120) * mm, "end": v(86, 120) * mm});
            skLineSegment(sketch, "E116.right", {"start": v(86, 126) * mm, "end": v(86, 120) * mm});
            skLineSegment(sketch, "E117", {"start": v(-88, 126) * mm, "end": v(92, 114) * mm, "construction": true});
            skCircle(sketch, "E118", {"center": v(2, 120) * mm, "radius": 2.5 * mm});
            skLineSegment(sketch, "E119", {"start": v(-88, 120) * mm, "end": v(2, 120) * mm, "construction": true});
            skCircle(sketch, "E120", {"center": v(-70, 120) * mm, "radius": 2.5 * mm});
            skCircle(sketch, "E121", {"center": v(-34, 120) * mm, "radius": 2.5 * mm});
            skSolve(sketch);
        }
        {
            var Q0;
            Q0=makeQuery(id+"F10.imprint","IMPRINT",FACE,{"disambiguationData":[TD([[makeQuery(id+"F10.imprint","IMPRINT",EDGE,{"derivedFrom":sQuery(id+"F10.wireOp",EDGE,"E114.bottom")}),1.0]])]});
            extrude(context, id + "F11", {"entities" : qUnion([Q0]), "oppositeDirection" : true, "depth" : 6 * mm});
        }
        {
            var Q0;
            Q0=makeQuery(id+"F11.opExtrude","SWEPT_FACE",FACE,{"disambiguationData":[OSD([sQuery(id+"F10.wireOp",EDGE,"E114.right")])]});
            var sketch = newSketch(context, id + "F12", { "sketchPlane" : qUnion([Q0])});
            skLineSegment(sketch, "E122.bottom", {"start": v(-83.76, 114) * mm, "end": v(80.24, 114) * mm});
            skLineSegment(sketch, "E122.top", {"start": v(-82, 126) * mm, "end": v(84.24, 126) * mm});
            skLineSegment(sketch, "E123.bottom", {"start": v(-89.76, 120) * mm, "end": v(-83.76, 120) * mm});
            skLineSegment(sketch, "E124.top", {"start": v(90.24, 120) * mm, "end": v(84.24, 120) * mm});
            skLineSegment(sketch, "E125", {"start": v(-82, 126) * mm, "end": v(-89.76, 126) * mm});
            skLineSegment(sketch, "E126", {"start": v(-89.76, 126) * mm, "end": v(-89.76, 120) * mm});
            skLineSegment(sketch, "E127", {"start": v(-83.76, 120) * mm, "end": v(-83.76, 114) * mm, "construction": true});
            skLineSegment(sketch, "E128", {"start": v(80.24, 114) * mm, "end": v(90.24, 114) * mm});
            skLineSegment(sketch, "E129", {"start": v(90.24, 114) * mm, "end": v(90.24, 120) * mm});
            skLineSegment(sketch, "E130", {"start": v(84.24, 120) * mm, "end": v(84.24, 126) * mm});
            skLineSegment(sketch, "E131", {"start": v(-89.76, 126) * mm, "end": v(90.24, 114) * mm, "construction": true});
            skCircle(sketch, "E132", {"center": v(0.24, 120) * mm, "radius": 2.5 * mm});
            skSolve(sketch);
        }
        {
            var Q0;
            Q0=makeQuery(id+"F12.imprint","IMPRINT",FACE,{"disambiguationData":[TD([[makeQuery(id+"F12.imprint","IMPRINT",EDGE,{"derivedFrom":sQuery(id+"F12.wireOp",EDGE,"E122.bottom")}),1.0]])]});
            extrude(context, id + "F13", {"entities" : qUnion([Q0]), "oppositeDirection" : true, "depth" : 6 * mm});
        }
        {
            var Q0;
            Q0=makeQuery(id+"F13.opExtrude","SWEPT_FACE",FACE,{"disambiguationData":[OSD([sQuery(id+"F12.wireOp",EDGE,"E129")])]});
            var sketch = newSketch(context, id + "F14", { "sketchPlane" : qUnion([Q0])});
            skLineSegment(sketch, "E133.bottom", {"start": v(-86, 114) * mm, "end": v(88, 114) * mm});
            skLineSegment(sketch, "E133.top", {"start": v(-92, 126) * mm, "end": v(82, 126) * mm});
            skLineSegment(sketch, "E133.left", {"start": v(-92, 120) * mm, "end": v(-92, 126) * mm});
            skLineSegment(sketch, "E133.right", {"start": v(88, 114) * mm, "end": v(88, 120) * mm});
            skLineSegment(sketch, "E134.bottom", {"start": v(-92, 120) * mm, "end": v(-86, 120) * mm});
            skLineSegment(sketch, "E134.right", {"start": v(-86, 120) * mm, "end": v(-86, 114) * mm});
            skLineSegment(sketch, "E135.top", {"start": v(88, 120) * mm, "end": v(82, 120) * mm});
            skLineSegment(sketch, "E135.right", {"start": v(82, 126) * mm, "end": v(82, 120) * mm});
            skLineSegment(sketch, "E136", {"start": v(-92, 126) * mm, "end": v(88, 114) * mm, "construction": true});
            skCircle(sketch, "E137", {"center": v(-2, 120) * mm, "radius": 2.5 * mm});
            skSolve(sketch);
        }
        {
            var Q0;
            Q0=makeQuery(id+"F14.imprint","IMPRINT",FACE,{"disambiguationData":[TD([[makeQuery(id+"F14.imprint","IMPRINT",EDGE,{"derivedFrom":sQuery(id+"F14.wireOp",EDGE,"E133.bottom")}),1.0]])]});
            extrude(context, id + "F15", {"entities" : qUnion([Q0]), "oppositeDirection" : true, "depth" : 6 * mm});
        }
        {
            var Q0;
            Q0=makeQuery(id+"F11.opExtrude","CAP_FACE",FACE,{"disambiguationData":[OSD([sQuery(id+"F10.wireOp",EDGE,"E114.bottom"),sQuery(id+"F10.wireOp",EDGE,"E114.top"),sQuery(id+"F10.wireOp",EDGE,"E114.left"),sQuery(id+"F10.wireOp",EDGE,"E114.right"),sQuery(id+"F10.wireOp",EDGE,"E115.top"),sQuery(id+"F10.wireOp",EDGE,"E115.right"),sQuery(id+"F10.wireOp",EDGE,"E116.top"),sQuery(id+"F10.wireOp",EDGE,"E116.right"),sQuery(id+"F10.wireOp",EDGE,"E118")])],"isStart":false});
            var sketch = newSketch(context, id + "F16", { "sketchPlane" : qUnion([Q0])});
            skLineSegment(sketch, "E138.rect.bottom", {"start": v(-8, 200) * mm, "end": v(-2, 200) * mm});
            skLineSegment(sketch, "E138.rect.top", {"start": v(-2, 40) * mm, "end": v(4, 40) * mm});
            skLineSegment(sketch, "E138.rect.left", {"start": v(-8, 200) * mm, "end": v(-8, 46) * mm});
            skLineSegment(sketch, "E138.rect.right", {"start": v(4, 194) * mm, "end": v(4, 40) * mm});
            skPoint(sketch, "E138.rect.middle", {"position": v(-2, 120) * mm});
            skPoint(sketch, "E139.oppositeSnap0", {"position": v(-2, 200) * mm});
            skLineSegment(sketch, "E139.top", {"start": v(4, 194) * mm, "end": v(-2, 194) * mm});
            skLineSegment(sketch, "E139.right", {"start": v(-2, 200) * mm, "end": v(-2, 194) * mm});
            skPoint(sketch, "E140.oppositeSnap0", {"position": v(-2, 40) * mm});
            skLineSegment(sketch, "E140.top", {"start": v(-8, 46) * mm, "end": v(-2, 46) * mm});
            skLineSegment(sketch, "E140.right", {"start": v(-2, 40) * mm, "end": v(-2, 46) * mm});
            skPoint(sketch, "E141.orphan", {"position": v(4, 200) * mm});
            skPoint(sketch, "E142.orphan", {"position": v(-8, 40) * mm});
            skCircle(sketch, "E143", {"center": v(-2, 120) * mm, "radius": 2.5 * mm});
            skSolve(sketch);
        }
        {
            var Q0;
            Q0 = qSketchRegion(id + "F16", true);
            extrude(context, id + "F17", {"entities" : qUnion([Q0]), "depth" : 6 * mm});
        }
        {
            var Q0;
            Q0=makeQuery(id+"F17.opExtrude","SWEPT_FACE",FACE,{"disambiguationData":[OSD([sQuery(id+"F16.wireOp",EDGE,"E138.rect.bottom")])]});
            var sketch = newSketch(context, id + "F18", { "sketchPlane" : qUnion([Q0])});
            skLineSegment(sketch, "E144.bottom", {"start": v(2, -83.76) * mm, "end": v(-4, -83.76) * mm});
            skLineSegment(sketch, "E144.top", {"start": v(8, 78.76) * mm, "end": v(2, 78.76) * mm});
            skLineSegment(sketch, "E144.left", {"start": v(8, -77.76) * mm, "end": v(8, 78.76) * mm});
            skLineSegment(sketch, "E144.right", {"start": v(-4, -83.76) * mm, "end": v(-4, 73.76) * mm});
            skLineSegment(sketch, "E145.top", {"start": v(8, -77.76) * mm, "end": v(2, -77.76) * mm});
            skLineSegment(sketch, "E145.right", {"start": v(2, -83.76) * mm, "end": v(2, -77.76) * mm});
            skPoint(sketch, "E146.oppositeSnap0", {"position": v(2, 78.76) * mm});
            skLineSegment(sketch, "E146.top", {"start": v(-4, 73.76) * mm, "end": v(2, 73.76) * mm});
            skLineSegment(sketch, "E146.right", {"start": v(2, 78.76) * mm, "end": v(2, 73.76) * mm});
            skPoint(sketch, "E147.orphan", {"position": v(-4, 78.76) * mm});
            skLineSegment(sketch, "E148", {"start": v(-4, -83.76) * mm, "end": v(8, 78.76) * mm, "construction": true});
            skCircle(sketch, "E149", {"center": v(2, -2.5) * mm, "radius": 2.5 * mm, "construction": true});
            skLineSegment(sketch, "E150.rect.bottom", {"start": v(0.5, 0) * mm, "end": v(3.5, 0) * mm});
            skLineSegment(sketch, "E150.rect.top", {"start": v(0.5, -5) * mm, "end": v(3.5, -5) * mm});
            skLineSegment(sketch, "E150.rect.left", {"start": v(0.5, 0) * mm, "end": v(0.5, -5) * mm});
            skLineSegment(sketch, "E150.rect.right", {"start": v(3.5, 0) * mm, "end": v(3.5, -5) * mm});
            skSolve(sketch);
        }
        {
            var Q0;
            Q0=makeQuery(id+"F18.imprint","IMPRINT",FACE,{"disambiguationData":[TD([[makeQuery(id+"F18.imprint","IMPRINT",EDGE,{"derivedFrom":sQuery(id+"F18.wireOp",EDGE,"E144.bottom")}),-1.0]])]});
            extrude(context, id + "F19", {"entities" : qUnion([Q0]), "oppositeDirection" : true, "depth" : 6 * mm});
        }
        {
            var Q0;
            Q0=makeQuery(id+"F19.opExtrude","SWEPT_FACE",FACE,{"disambiguationData":[OSD([sQuery(id+"F18.wireOp",EDGE,"E144.top")])]});
            var sketch = newSketch(context, id + "F20", { "sketchPlane" : qUnion([Q0])});
            skLineSegment(sketch, "E151.bottom", {"start": v(-2, 200) * mm, "end": v(4, 200) * mm});
            skLineSegment(sketch, "E151.top", {"start": v(-8, 40) * mm, "end": v(-2, 40) * mm});
            skLineSegment(sketch, "E151.left", {"start": v(-8, 194) * mm, "end": v(-8, 40) * mm});
            skLineSegment(sketch, "E151.right", {"start": v(4, 200) * mm, "end": v(4, 46) * mm});
            skLineSegment(sketch, "E152.top", {"start": v(-8, 194) * mm, "end": v(-2, 194) * mm});
            skLineSegment(sketch, "E152.right", {"start": v(-2, 200) * mm, "end": v(-2, 194) * mm});
            skPoint(sketch, "E153.oppositeSnap0", {"position": v(-2, 40) * mm});
            skLineSegment(sketch, "E153.top", {"start": v(4, 46) * mm, "end": v(-2, 46) * mm});
            skLineSegment(sketch, "E153.right", {"start": v(-2, 40) * mm, "end": v(-2, 46) * mm});
            skPoint(sketch, "E154.orphan", {"position": v(4, 40) * mm});
            skLineSegment(sketch, "E155", {"start": v(4, 200) * mm, "end": v(-8, 40) * mm, "construction": true});
            skCircle(sketch, "E156", {"center": v(-2, 120) * mm, "radius": 2.5 * mm});
            skSolve(sketch);
        }
        {
            var Q0;
            Q0=makeQuery(id+"F20.imprint","IMPRINT",FACE,{"disambiguationData":[TD([[makeQuery(id+"F20.imprint","IMPRINT",EDGE,{"derivedFrom":sQuery(id+"F20.wireOp",EDGE,"E151.bottom")}),-1.0]])]});
            extrude(context, id + "F21", {"entities" : qUnion([Q0]), "oppositeDirection" : true, "depth" : 6 * mm});
        }
        {
            var Q0;
            Q0=makeQuery(id+"F17.opExtrude","SWEPT_FACE",FACE,{"disambiguationData":[OSD([sQuery(id+"F16.wireOp",EDGE,"E138.rect.top")])]});
            var sketch = newSketch(context, id + "F22", { "sketchPlane" : qUnion([Q0])});
            skLineSegment(sketch, "E157.bottom", {"start": v(2, 84) * mm, "end": v(8, 84) * mm});
            skLineSegment(sketch, "E157.top", {"start": v(-4, -78.76) * mm, "end": v(2, -78.76) * mm});
            skLineSegment(sketch, "E157.left", {"start": v(-4, 77.76) * mm, "end": v(-4, -78.76) * mm});
            skLineSegment(sketch, "E157.right", {"start": v(8, 84) * mm, "end": v(8, -72.76) * mm});
            skLineSegment(sketch, "E158.top", {"start": v(-4, 77.76) * mm, "end": v(2, 77.76) * mm});
            skLineSegment(sketch, "E158.right", {"start": v(2, 84) * mm, "end": v(2, 77.76) * mm});
            skPoint(sketch, "E159.oppositeSnap0", {"position": v(2, -78.76) * mm});
            skLineSegment(sketch, "E159.top", {"start": v(8, -72.76) * mm, "end": v(2, -72.76) * mm});
            skLineSegment(sketch, "E159.right", {"start": v(2, -78.76) * mm, "end": v(2, -72.76) * mm});
            skPoint(sketch, "E160.orphan", {"position": v(8, -78.76) * mm});
            skLineSegment(sketch, "E161", {"start": v(-4, 83.76) * mm, "end": v(8, -78.76) * mm, "construction": true});
            skLineSegment(sketch, "E162.rect.bottom", {"start": v(0.5, 5.5) * mm, "end": v(3.5, 5.5) * mm});
            skLineSegment(sketch, "E162.rect.top", {"start": v(0.5, -0.5) * mm, "end": v(3.5, -0.5) * mm});
            skLineSegment(sketch, "E162.rect.left", {"start": v(0.5, 5.5) * mm, "end": v(0.5, -0.5) * mm});
            skLineSegment(sketch, "E162.rect.right", {"start": v(3.5, 5.5) * mm, "end": v(3.5, -0.5) * mm});
            skPoint(sketch, "E162.rect.middle", {"position": v(2, 2.5) * mm});
            skSolve(sketch);
        }
        {
            var Q0;
            Q0 = qSketchRegion(id + "F22", true);
            extrude(context, id + "F23", {"entities" : qUnion([Q0]), "operationType" : NewBodyOperationType.ADD, "oppositeDirection" : true, "depth" : 6 * mm});
        }
        {
            var Q0;
            Q0=makeQuery(id+"F9.opExtrude","CAP_FACE",FACE,{"disambiguationData":[OSD([sQuery(id+"F8.wireOp",EDGE,"E102.rect.bottom"),sQuery(id+"F8.wireOp",EDGE,"E102.rect.top"),sQuery(id+"F8.wireOp",EDGE,"E102.rect.left"),sQuery(id+"F8.wireOp",EDGE,"E102.rect.right"),sQuery(id+"F8.wireOp",EDGE,"E103"),sQuery(id+"F8.wireOp",EDGE,"E104"),sQuery(id+"F8.wireOp",EDGE,"E105"),sQuery(id+"F8.wireOp",EDGE,"E106"),sQuery(id+"F8.wireOp",EDGE,"E107"),sQuery(id+"F8.wireOp",EDGE,"E112")])],"isStart":true});
            var sketch = newSketch(context, id + "F24", { "sketchPlane" : qUnion([Q0])});
            skCircle(sketch, "E163", {"center": v(71.76, 120) * mm, "radius": 16.4 * mm, "construction": true});
            skCircle(sketch, "E164", {"center": v(71.76, 120) * mm, "radius": 19.4 * mm, "construction": true});
            skCircle(sketch, "E165", {"center": v(71.76, 120) * mm, "radius": 2.5 * mm});
            skLineSegment(sketch, "E166", {"start": v(71.76, 120) * mm, "end": v(71.76, 139.4) * mm, "construction": true});
            skLineSegment(sketch, "E167", {"start": v(71.76, 120) * mm, "end": v(70.07, 139.33) * mm, "construction": true});
            skLineSegment(sketch, "E168", {"start": v(71.76, 120) * mm, "end": v(70.49, 139.36) * mm, "construction": true});
            skLineSegment(sketch, "E169", {"start": v(71.76, 120) * mm, "end": v(70.9, 139.38) * mm, "construction": true});
            skLineSegment(sketch, "E170", {"start": v(71.76, 120) * mm, "end": v(71.33, 139.4) * mm, "construction": true});
            skLineSegment(sketch, "E171.MirrorCS", {"start": v(71.76, 120) * mm, "end": v(72.6, 139.38) * mm, "construction": true});
            skLineSegment(sketch, "E172.MirrorCS", {"start": v(71.76, 120) * mm, "end": v(73.02, 139.36) * mm, "construction": true});
            skLineSegment(sketch, "E173.MirrorCS", {"start": v(71.76, 120) * mm, "end": v(73.45, 139.33) * mm, "construction": true});
            skLineSegment(sketch, "E174.MirrorCS", {"start": v(71.76, 120) * mm, "end": v(72.18, 139.4) * mm, "construction": true});
            skArc(sketch, "E175", {"start": v(72.18, 139.4) * mm, "mid": v(71.76, 139.4) * mm, "end": v(71.33, 139.4) * mm});
            skLineSegment(sketch, "E176", {"start": v(72.18, 139.4) * mm, "end": v(72.83, 136.36) * mm});
            skLineSegment(sketch, "E177", {"start": v(71.33, 139.4) * mm, "end": v(70.68, 136.36) * mm});
            skLineSegment(sketch, "E178", {"start": v(72.83, 136.36) * mm, "end": v(73.19, 136.34) * mm});
            skPoint(sketch, "E179", {"position": v(70.33, 136.34) * mm});
            skLineSegment(sketch, "E180", {"start": v(70.68, 136.36) * mm, "end": v(70.33, 136.34) * mm});
            skLineSegment(sketch, "E181.1.0", {"start": v(67.97, 139.03) * mm, "end": v(67.86, 135.93) * mm});
            skLineSegment(sketch, "E181.1.1", {"start": v(67.86, 135.93) * mm, "end": v(67.51, 135.84) * mm});
            skLineSegment(sketch, "E181.1.2", {"start": v(68.8, 139.17) * mm, "end": v(69.97, 136.3) * mm});
            skLineSegment(sketch, "E181.1.3", {"start": v(69.97, 136.3) * mm, "end": v(70.33, 136.34) * mm});
            skArc(sketch, "E181.1.4", {"start": v(68.8, 139.17) * mm, "mid": v(68.39, 139.1) * mm, "end": v(67.97, 139.03) * mm});
            skLineSegment(sketch, "E181.2.0", {"start": v(64.72, 138.08) * mm, "end": v(65.15, 135.01) * mm});
            skLineSegment(sketch, "E181.2.1", {"start": v(65.15, 135.01) * mm, "end": v(64.83, 134.86) * mm});
            skLineSegment(sketch, "E181.2.2", {"start": v(65.52, 138.37) * mm, "end": v(67.17, 135.74) * mm});
            skLineSegment(sketch, "E181.2.3", {"start": v(67.17, 135.74) * mm, "end": v(67.51, 135.84) * mm});
            skArc(sketch, "E181.2.4", {"start": v(65.52, 138.37) * mm, "mid": v(65.12, 138.23) * mm, "end": v(64.72, 138.08) * mm});
            skLineSegment(sketch, "E181.3.0", {"start": v(61.7, 136.59) * mm, "end": v(62.64, 133.64) * mm});
            skLineSegment(sketch, "E181.3.1", {"start": v(62.64, 133.64) * mm, "end": v(62.35, 133.43) * mm});
            skLineSegment(sketch, "E181.3.2", {"start": v(62.42, 137) * mm, "end": v(64.5, 134.7) * mm});
            skLineSegment(sketch, "E181.3.3", {"start": v(64.5, 134.7) * mm, "end": v(64.83, 134.86) * mm});
            skArc(sketch, "E181.3.4", {"start": v(62.42, 137) * mm, "mid": v(62.06, 136.8) * mm, "end": v(61.7, 136.59) * mm});
            skLineSegment(sketch, "E181.4.0", {"start": v(58.96, 134.59) * mm, "end": v(60.42, 131.85) * mm});
            skLineSegment(sketch, "E181.4.1", {"start": v(60.42, 131.85) * mm, "end": v(60.16, 131.6) * mm});
            skLineSegment(sketch, "E181.4.2", {"start": v(59.61, 135.13) * mm, "end": v(62.06, 133.23) * mm});
            skLineSegment(sketch, "E181.4.3", {"start": v(62.06, 133.23) * mm, "end": v(62.35, 133.43) * mm});
            skArc(sketch, "E181.4.4", {"start": v(59.61, 135.13) * mm, "mid": v(59.29, 134.86) * mm, "end": v(58.96, 134.59) * mm});
            skLineSegment(sketch, "E181.5.0", {"start": v(56.63, 132.14) * mm, "end": v(58.53, 129.7) * mm});
            skLineSegment(sketch, "E181.5.1", {"start": v(58.53, 129.7) * mm, "end": v(58.32, 129.4) * mm});
            skLineSegment(sketch, "E181.5.2", {"start": v(57.17, 132.8) * mm, "end": v(59.9, 131.34) * mm});
            skLineSegment(sketch, "E181.5.3", {"start": v(59.9, 131.34) * mm, "end": v(60.16, 131.6) * mm});
            skArc(sketch, "E181.5.4", {"start": v(57.17, 132.8) * mm, "mid": v(56.9, 132.47) * mm, "end": v(56.63, 132.14) * mm});
            skLineSegment(sketch, "E181.6.0", {"start": v(54.75, 129.33) * mm, "end": v(57.05, 127.25) * mm});
            skLineSegment(sketch, "E181.6.1", {"start": v(57.05, 127.25) * mm, "end": v(56.9, 126.93) * mm});
            skLineSegment(sketch, "E181.6.2", {"start": v(55.17, 130.06) * mm, "end": v(58.12, 129.11) * mm});
            skLineSegment(sketch, "E181.6.3", {"start": v(58.12, 129.11) * mm, "end": v(58.32, 129.4) * mm});
            skArc(sketch, "E181.6.4", {"start": v(55.17, 130.06) * mm, "mid": v(54.96, 129.7) * mm, "end": v(54.75, 129.33) * mm});
            skLineSegment(sketch, "E181.7.0", {"start": v(53.39, 126.24) * mm, "end": v(56.01, 124.59) * mm});
            skLineSegment(sketch, "E181.7.1", {"start": v(56.01, 124.59) * mm, "end": v(55.91, 124.24) * mm});
            skLineSegment(sketch, "E181.7.2", {"start": v(53.68, 127.03) * mm, "end": v(56.74, 126.6) * mm});
            skLineSegment(sketch, "E181.7.3", {"start": v(56.74, 126.6) * mm, "end": v(56.9, 126.93) * mm});
            skArc(sketch, "E181.7.4", {"start": v(53.68, 127.03) * mm, "mid": v(53.53, 126.64) * mm, "end": v(53.39, 126.24) * mm});
            skLineSegment(sketch, "E181.8.0", {"start": v(52.58, 122.95) * mm, "end": v(55.45, 121.79) * mm});
            skLineSegment(sketch, "E181.8.1", {"start": v(55.45, 121.79) * mm, "end": v(55.42, 121.43) * mm});
            skLineSegment(sketch, "E181.8.2", {"start": v(52.73, 123.78) * mm, "end": v(55.83, 123.9) * mm});
            skLineSegment(sketch, "E181.8.3", {"start": v(55.83, 123.9) * mm, "end": v(55.91, 124.24) * mm});
            skArc(sketch, "E181.8.4", {"start": v(52.73, 123.78) * mm, "mid": v(52.65, 123.37) * mm, "end": v(52.58, 122.95) * mm});
            skLineSegment(sketch, "E181.9.0", {"start": v(52.36, 119.58) * mm, "end": v(55.4, 118.93) * mm});
            skLineSegment(sketch, "E181.9.1", {"start": v(55.4, 118.93) * mm, "end": v(55.42, 118.57) * mm});
            skLineSegment(sketch, "E181.9.2", {"start": v(52.36, 120.42) * mm, "end": v(55.4, 121.07) * mm});
            skLineSegment(sketch, "E181.9.3", {"start": v(55.4, 121.07) * mm, "end": v(55.42, 121.43) * mm});
            skArc(sketch, "E181.9.4", {"start": v(52.36, 120.42) * mm, "mid": v(52.36, 120) * mm, "end": v(52.36, 119.58) * mm});
            skLineSegment(sketch, "E181.10.0", {"start": v(52.73, 116.22) * mm, "end": v(55.83, 116.1) * mm});
            skLineSegment(sketch, "E181.10.1", {"start": v(55.83, 116.1) * mm, "end": v(55.91, 115.76) * mm});
            skLineSegment(sketch, "E181.10.2", {"start": v(52.58, 117.05) * mm, "end": v(55.45, 118.21) * mm});
            skLineSegment(sketch, "E181.10.3", {"start": v(55.45, 118.21) * mm, "end": v(55.42, 118.57) * mm});
            skArc(sketch, "E181.10.4", {"start": v(52.58, 117.05) * mm, "mid": v(52.65, 116.63) * mm, "end": v(52.73, 116.22) * mm});
            skLineSegment(sketch, "E181.11.0", {"start": v(53.68, 112.97) * mm, "end": v(56.74, 113.4) * mm});
            skLineSegment(sketch, "E181.11.1", {"start": v(56.74, 113.4) * mm, "end": v(56.9, 113.07) * mm});
            skLineSegment(sketch, "E181.11.2", {"start": v(53.39, 113.76) * mm, "end": v(56.01, 115.41) * mm});
            skLineSegment(sketch, "E181.11.3", {"start": v(56.01, 115.41) * mm, "end": v(55.91, 115.76) * mm});
            skArc(sketch, "E181.11.4", {"start": v(53.39, 113.76) * mm, "mid": v(53.53, 113.36) * mm, "end": v(53.68, 112.97) * mm});
            skLineSegment(sketch, "E181.12.0", {"start": v(55.17, 109.94) * mm, "end": v(58.12, 110.89) * mm});
            skLineSegment(sketch, "E181.12.1", {"start": v(58.12, 110.89) * mm, "end": v(58.32, 110.6) * mm});
            skLineSegment(sketch, "E181.12.2", {"start": v(54.75, 110.67) * mm, "end": v(57.05, 112.75) * mm});
            skLineSegment(sketch, "E181.12.3", {"start": v(57.05, 112.75) * mm, "end": v(56.9, 113.07) * mm});
            skArc(sketch, "E181.12.4", {"start": v(54.75, 110.67) * mm, "mid": v(54.96, 110.3) * mm, "end": v(55.17, 109.94) * mm});
            skLineSegment(sketch, "E181.13.0", {"start": v(57.17, 107.2) * mm, "end": v(59.9, 108.66) * mm});
            skLineSegment(sketch, "E181.13.1", {"start": v(59.9, 108.66) * mm, "end": v(60.16, 108.4) * mm});
            skLineSegment(sketch, "E181.13.2", {"start": v(56.63, 107.86) * mm, "end": v(58.53, 110.3) * mm});
            skLineSegment(sketch, "E181.13.3", {"start": v(58.53, 110.3) * mm, "end": v(58.32, 110.6) * mm});
            skArc(sketch, "E181.13.4", {"start": v(56.63, 107.86) * mm, "mid": v(56.9, 107.53) * mm, "end": v(57.17, 107.2) * mm});
            skLineSegment(sketch, "E181.14.0", {"start": v(59.61, 104.87) * mm, "end": v(62.06, 106.77) * mm});
            skLineSegment(sketch, "E181.14.1", {"start": v(62.06, 106.77) * mm, "end": v(62.35, 106.57) * mm});
            skLineSegment(sketch, "E181.14.2", {"start": v(58.96, 105.41) * mm, "end": v(60.42, 108.15) * mm});
            skLineSegment(sketch, "E181.14.3", {"start": v(60.42, 108.15) * mm, "end": v(60.16, 108.4) * mm});
            skArc(sketch, "E181.14.4", {"start": v(58.96, 105.41) * mm, "mid": v(59.29, 105.14) * mm, "end": v(59.61, 104.87) * mm});
            skLineSegment(sketch, "E181.15.0", {"start": v(62.42, 103) * mm, "end": v(64.5, 105.3) * mm});
            skLineSegment(sketch, "E181.15.1", {"start": v(64.5, 105.3) * mm, "end": v(64.83, 105.14) * mm});
            skLineSegment(sketch, "E181.15.2", {"start": v(61.7, 103.41) * mm, "end": v(62.64, 106.36) * mm});
            skLineSegment(sketch, "E181.15.3", {"start": v(62.64, 106.36) * mm, "end": v(62.35, 106.57) * mm});
            skArc(sketch, "E181.15.4", {"start": v(61.7, 103.41) * mm, "mid": v(62.06, 103.2) * mm, "end": v(62.42, 103) * mm});
            skLineSegment(sketch, "E181.16.0", {"start": v(65.52, 101.63) * mm, "end": v(67.17, 104.26) * mm});
            skLineSegment(sketch, "E181.16.1", {"start": v(67.17, 104.26) * mm, "end": v(67.51, 104.16) * mm});
            skLineSegment(sketch, "E181.16.2", {"start": v(64.72, 101.92) * mm, "end": v(65.15, 104.99) * mm});
            skLineSegment(sketch, "E181.16.3", {"start": v(65.15, 104.99) * mm, "end": v(64.83, 105.14) * mm});
            skArc(sketch, "E181.16.4", {"start": v(64.72, 101.92) * mm, "mid": v(65.12, 101.77) * mm, "end": v(65.52, 101.63) * mm});
            skLineSegment(sketch, "E181.17.0", {"start": v(68.8, 100.83) * mm, "end": v(69.97, 103.7) * mm});
            skLineSegment(sketch, "E181.17.1", {"start": v(69.97, 103.7) * mm, "end": v(70.33, 103.66) * mm});
            skLineSegment(sketch, "E181.17.2", {"start": v(67.97, 100.97) * mm, "end": v(67.86, 104.07) * mm});
            skLineSegment(sketch, "E181.17.3", {"start": v(67.86, 104.07) * mm, "end": v(67.51, 104.16) * mm});
            skArc(sketch, "E181.17.4", {"start": v(67.97, 100.97) * mm, "mid": v(68.39, 100.9) * mm, "end": v(68.8, 100.83) * mm});
            skLineSegment(sketch, "E181.18.0", {"start": v(72.18, 100.6) * mm, "end": v(72.83, 103.64) * mm});
            skLineSegment(sketch, "E181.18.1", {"start": v(72.83, 103.64) * mm, "end": v(73.19, 103.66) * mm});
            skLineSegment(sketch, "E181.18.2", {"start": v(71.33, 100.6) * mm, "end": v(70.68, 103.64) * mm});
            skLineSegment(sketch, "E181.18.3", {"start": v(70.68, 103.64) * mm, "end": v(70.33, 103.66) * mm});
            skArc(sketch, "E181.18.4", {"start": v(71.33, 100.6) * mm, "mid": v(71.76, 100.6) * mm, "end": v(72.18, 100.6) * mm});
            skLineSegment(sketch, "E181.19.0", {"start": v(75.54, 100.97) * mm, "end": v(75.65, 104.07) * mm});
            skLineSegment(sketch, "E181.19.1", {"start": v(75.65, 104.07) * mm, "end": v(76, 104.16) * mm});
            skLineSegment(sketch, "E181.19.2", {"start": v(74.7, 100.83) * mm, "end": v(73.54, 103.7) * mm});
            skLineSegment(sketch, "E181.19.3", {"start": v(73.54, 103.7) * mm, "end": v(73.19, 103.66) * mm});
            skArc(sketch, "E181.19.4", {"start": v(74.7, 100.83) * mm, "mid": v(75.12, 100.9) * mm, "end": v(75.54, 100.97) * mm});
            skLineSegment(sketch, "E181.20.0", {"start": v(78.79, 101.92) * mm, "end": v(78.36, 104.99) * mm});
            skLineSegment(sketch, "E181.20.1", {"start": v(78.36, 104.99) * mm, "end": v(78.69, 105.14) * mm});
            skLineSegment(sketch, "E181.20.2", {"start": v(78, 101.63) * mm, "end": v(76.35, 104.26) * mm});
            skLineSegment(sketch, "E181.20.3", {"start": v(76.35, 104.26) * mm, "end": v(76, 104.16) * mm});
            skArc(sketch, "E181.20.4", {"start": v(78, 101.63) * mm, "mid": v(78.4, 101.77) * mm, "end": v(78.79, 101.92) * mm});
            skLineSegment(sketch, "E181.21.0", {"start": v(81.82, 103.41) * mm, "end": v(80.87, 106.36) * mm});
            skLineSegment(sketch, "E181.21.1", {"start": v(80.87, 106.36) * mm, "end": v(81.16, 106.57) * mm});
            skLineSegment(sketch, "E181.21.2", {"start": v(81.09, 103) * mm, "end": v(79, 105.3) * mm});
            skLineSegment(sketch, "E181.21.3", {"start": v(79, 105.3) * mm, "end": v(78.69, 105.14) * mm});
            skArc(sketch, "E181.21.4", {"start": v(81.09, 103) * mm, "mid": v(81.46, 103.2) * mm, "end": v(81.82, 103.41) * mm});
            skLineSegment(sketch, "E181.22.0", {"start": v(84.55, 105.41) * mm, "end": v(83.1, 108.15) * mm});
            skLineSegment(sketch, "E181.22.1", {"start": v(83.1, 108.15) * mm, "end": v(83.35, 108.4) * mm});
            skLineSegment(sketch, "E181.22.2", {"start": v(83.9, 104.87) * mm, "end": v(81.45, 106.77) * mm});
            skLineSegment(sketch, "E181.22.3", {"start": v(81.45, 106.77) * mm, "end": v(81.16, 106.57) * mm});
            skArc(sketch, "E181.22.4", {"start": v(83.9, 104.87) * mm, "mid": v(84.23, 105.14) * mm, "end": v(84.55, 105.41) * mm});
            skLineSegment(sketch, "E181.23.0", {"start": v(86.89, 107.86) * mm, "end": v(84.98, 110.3) * mm});
            skLineSegment(sketch, "E181.23.1", {"start": v(84.98, 110.3) * mm, "end": v(85.2, 110.6) * mm});
            skLineSegment(sketch, "E181.23.2", {"start": v(86.34, 107.2) * mm, "end": v(83.6, 108.66) * mm});
            skLineSegment(sketch, "E181.23.3", {"start": v(83.6, 108.66) * mm, "end": v(83.35, 108.4) * mm});
            skArc(sketch, "E181.23.4", {"start": v(86.34, 107.2) * mm, "mid": v(86.62, 107.53) * mm, "end": v(86.89, 107.86) * mm});
            skLineSegment(sketch, "E181.24.0", {"start": v(88.76, 110.67) * mm, "end": v(86.46, 112.75) * mm});
            skLineSegment(sketch, "E181.24.1", {"start": v(86.46, 112.75) * mm, "end": v(86.62, 113.07) * mm});
            skLineSegment(sketch, "E181.24.2", {"start": v(88.34, 109.94) * mm, "end": v(85.4, 110.89) * mm});
            skLineSegment(sketch, "E181.24.3", {"start": v(85.4, 110.89) * mm, "end": v(85.2, 110.6) * mm});
            skArc(sketch, "E181.24.4", {"start": v(88.34, 109.94) * mm, "mid": v(88.56, 110.3) * mm, "end": v(88.76, 110.67) * mm});
            skLineSegment(sketch, "E181.25.0", {"start": v(90.13, 113.76) * mm, "end": v(87.5, 115.41) * mm});
            skLineSegment(sketch, "E181.25.1", {"start": v(87.5, 115.41) * mm, "end": v(87.6, 115.76) * mm});
            skLineSegment(sketch, "E181.25.2", {"start": v(89.84, 112.97) * mm, "end": v(86.77, 113.4) * mm});
            skLineSegment(sketch, "E181.25.3", {"start": v(86.77, 113.4) * mm, "end": v(86.62, 113.07) * mm});
            skArc(sketch, "E181.25.4", {"start": v(89.84, 112.97) * mm, "mid": v(89.99, 113.36) * mm, "end": v(90.13, 113.76) * mm});
            skLineSegment(sketch, "E181.26.0", {"start": v(90.93, 117.05) * mm, "end": v(88.06, 118.21) * mm});
            skLineSegment(sketch, "E181.26.1", {"start": v(88.06, 118.21) * mm, "end": v(88.1, 118.57) * mm});
            skLineSegment(sketch, "E181.26.2", {"start": v(90.78, 116.22) * mm, "end": v(87.69, 116.1) * mm});
            skLineSegment(sketch, "E181.26.3", {"start": v(87.69, 116.1) * mm, "end": v(87.6, 115.76) * mm});
            skArc(sketch, "E181.26.4", {"start": v(90.78, 116.22) * mm, "mid": v(90.86, 116.63) * mm, "end": v(90.93, 117.05) * mm});
            skLineSegment(sketch, "E181.27.0", {"start": v(91.15, 120.42) * mm, "end": v(88.12, 121.07) * mm});
            skLineSegment(sketch, "E181.27.1", {"start": v(88.12, 121.07) * mm, "end": v(88.1, 121.43) * mm});
            skLineSegment(sketch, "E181.27.2", {"start": v(91.15, 119.58) * mm, "end": v(88.12, 118.93) * mm});
            skLineSegment(sketch, "E181.27.3", {"start": v(88.12, 118.93) * mm, "end": v(88.1, 118.57) * mm});
            skArc(sketch, "E181.27.4", {"start": v(91.15, 119.58) * mm, "mid": v(91.16, 120) * mm, "end": v(91.15, 120.42) * mm});
            skLineSegment(sketch, "E181.28.0", {"start": v(90.78, 123.78) * mm, "end": v(87.69, 123.9) * mm});
            skLineSegment(sketch, "E181.28.1", {"start": v(87.69, 123.9) * mm, "end": v(87.6, 124.24) * mm});
            skLineSegment(sketch, "E181.28.2", {"start": v(90.93, 122.95) * mm, "end": v(88.06, 121.79) * mm});
            skLineSegment(sketch, "E181.28.3", {"start": v(88.06, 121.79) * mm, "end": v(88.1, 121.43) * mm});
            skArc(sketch, "E181.28.4", {"start": v(90.93, 122.95) * mm, "mid": v(90.86, 123.37) * mm, "end": v(90.78, 123.78) * mm});
            skLineSegment(sketch, "E181.29.0", {"start": v(89.84, 127.03) * mm, "end": v(86.77, 126.6) * mm});
            skLineSegment(sketch, "E181.29.1", {"start": v(86.77, 126.6) * mm, "end": v(86.62, 126.93) * mm});
            skLineSegment(sketch, "E181.29.2", {"start": v(90.13, 126.24) * mm, "end": v(87.5, 124.59) * mm});
            skLineSegment(sketch, "E181.29.3", {"start": v(87.5, 124.59) * mm, "end": v(87.6, 124.24) * mm});
            skArc(sketch, "E181.29.4", {"start": v(90.13, 126.24) * mm, "mid": v(89.99, 126.64) * mm, "end": v(89.84, 127.03) * mm});
            skLineSegment(sketch, "E181.30.0", {"start": v(88.34, 130.06) * mm, "end": v(85.4, 129.11) * mm});
            skLineSegment(sketch, "E181.30.1", {"start": v(85.4, 129.11) * mm, "end": v(85.2, 129.4) * mm});
            skLineSegment(sketch, "E181.30.2", {"start": v(88.76, 129.33) * mm, "end": v(86.46, 127.25) * mm});
            skLineSegment(sketch, "E181.30.3", {"start": v(86.46, 127.25) * mm, "end": v(86.62, 126.93) * mm});
            skArc(sketch, "E181.30.4", {"start": v(88.76, 129.33) * mm, "mid": v(88.56, 129.7) * mm, "end": v(88.34, 130.06) * mm});
            skLineSegment(sketch, "E181.31.0", {"start": v(86.34, 132.8) * mm, "end": v(83.6, 131.34) * mm});
            skLineSegment(sketch, "E181.31.1", {"start": v(83.6, 131.34) * mm, "end": v(83.35, 131.6) * mm});
            skLineSegment(sketch, "E181.31.2", {"start": v(86.89, 132.14) * mm, "end": v(84.98, 129.7) * mm});
            skLineSegment(sketch, "E181.31.3", {"start": v(84.98, 129.7) * mm, "end": v(85.2, 129.4) * mm});
            skArc(sketch, "E181.31.4", {"start": v(86.89, 132.14) * mm, "mid": v(86.62, 132.47) * mm, "end": v(86.34, 132.8) * mm});
            skLineSegment(sketch, "E181.32.0", {"start": v(83.9, 135.13) * mm, "end": v(81.45, 133.23) * mm});
            skLineSegment(sketch, "E181.32.1", {"start": v(81.45, 133.23) * mm, "end": v(81.16, 133.43) * mm});
            skLineSegment(sketch, "E181.32.2", {"start": v(84.55, 134.59) * mm, "end": v(83.1, 131.85) * mm});
            skLineSegment(sketch, "E181.32.3", {"start": v(83.1, 131.85) * mm, "end": v(83.35, 131.6) * mm});
            skArc(sketch, "E181.32.4", {"start": v(84.55, 134.59) * mm, "mid": v(84.23, 134.86) * mm, "end": v(83.9, 135.13) * mm});
            skLineSegment(sketch, "E181.33.0", {"start": v(81.09, 137) * mm, "end": v(79, 134.7) * mm});
            skLineSegment(sketch, "E181.33.1", {"start": v(79, 134.7) * mm, "end": v(78.69, 134.86) * mm});
            skLineSegment(sketch, "E181.33.2", {"start": v(81.82, 136.59) * mm, "end": v(80.87, 133.64) * mm});
            skLineSegment(sketch, "E181.33.3", {"start": v(80.87, 133.64) * mm, "end": v(81.16, 133.43) * mm});
            skArc(sketch, "E181.33.4", {"start": v(81.82, 136.59) * mm, "mid": v(81.46, 136.8) * mm, "end": v(81.09, 137) * mm});
            skLineSegment(sketch, "E181.34.0", {"start": v(78, 138.37) * mm, "end": v(76.35, 135.74) * mm});
            skLineSegment(sketch, "E181.34.1", {"start": v(76.35, 135.74) * mm, "end": v(76, 135.84) * mm});
            skLineSegment(sketch, "E181.34.2", {"start": v(78.79, 138.08) * mm, "end": v(78.36, 135.01) * mm});
            skLineSegment(sketch, "E181.34.3", {"start": v(78.36, 135.01) * mm, "end": v(78.69, 134.86) * mm});
            skArc(sketch, "E181.34.4", {"start": v(78.79, 138.08) * mm, "mid": v(78.4, 138.23) * mm, "end": v(78, 138.37) * mm});
            skLineSegment(sketch, "E181.35.0", {"start": v(74.7, 139.17) * mm, "end": v(73.54, 136.3) * mm});
            skLineSegment(sketch, "E181.35.1", {"start": v(73.54, 136.3) * mm, "end": v(73.19, 136.34) * mm});
            skLineSegment(sketch, "E181.35.2", {"start": v(75.54, 139.03) * mm, "end": v(75.65, 135.93) * mm});
            skLineSegment(sketch, "E181.35.3", {"start": v(75.65, 135.93) * mm, "end": v(76, 135.84) * mm});
            skArc(sketch, "E181.35.4", {"start": v(75.54, 139.03) * mm, "mid": v(75.12, 139.1) * mm, "end": v(74.7, 139.17) * mm});
            skLineSegment(sketch, "E182", {"start": v(-327.67, -4594.38) * mm, "end": v(-280.95, -4594.38) * mm});
            skLineSegment(sketch, "E183", {"start": v(-280.95, -4594.38) * mm, "end": v(-168.42, -5905.89) * mm});
            skLineSegment(sketch, "E184", {"start": v(-168.42, -5905.89) * mm, "end": v(-403.83, -5905.89) * mm});
            skLineSegment(sketch, "E185", {"start": v(-403.83, -5905.89) * mm, "end": v(-327.67, -4594.38) * mm});
            skSolve(sketch);
        }
        {
            var Q0;
            Q0 = qSketchRegion(id + "F24", true);
            extrude(context, id + "F25", {"entities" : qUnion([Q0]), "depth" : 6 * mm, "hasDraft" : true, "draftAngle" : 45 * degree});
        }
        {
            var Q0;
            Q0=makeQuery(id+"F11.opExtrude","CAP_FACE",FACE,{"disambiguationData":[OSD([sQuery(id+"F10.wireOp",EDGE,"E114.bottom"),sQuery(id+"F10.wireOp",EDGE,"E114.top"),sQuery(id+"F10.wireOp",EDGE,"E114.left"),sQuery(id+"F10.wireOp",EDGE,"E114.right"),sQuery(id+"F10.wireOp",EDGE,"E115.top"),sQuery(id+"F10.wireOp",EDGE,"E115.right"),sQuery(id+"F10.wireOp",EDGE,"E116.top"),sQuery(id+"F10.wireOp",EDGE,"E116.right"),sQuery(id+"F10.wireOp",EDGE,"E118"),sQuery(id+"F10.wireOp",EDGE,"E120"),sQuery(id+"F10.wireOp",EDGE,"E121")])],"isStart":true});
            var sketch = newSketch(context, id + "F26", { "sketchPlane" : qUnion([Q0])});
            skCircle(sketch, "E186", {"center": v(-70, 120) * mm, "radius": 18 * mm});
            skCircle(sketch, "E187", {"center": v(-70, 120) * mm, "radius": 2.5 * mm});
            skSolve(sketch);
        }
        {
            var Q0;
            Q0 = qSketchRegion(id + "F26", true);
            extrude(context, id + "F27", {"entities" : qUnion([Q0]), "depth" : 6 * mm});
        }
        {
            var Q0;
            Q0=makeQuery(id+"F11.opExtrude","CAP_FACE",FACE,{"disambiguationData":[OSD([sQuery(id+"F10.wireOp",EDGE,"E114.bottom"),sQuery(id+"F10.wireOp",EDGE,"E114.top"),sQuery(id+"F10.wireOp",EDGE,"E114.left"),sQuery(id+"F10.wireOp",EDGE,"E114.right"),sQuery(id+"F10.wireOp",EDGE,"E115.top"),sQuery(id+"F10.wireOp",EDGE,"E115.right"),sQuery(id+"F10.wireOp",EDGE,"E116.top"),sQuery(id+"F10.wireOp",EDGE,"E116.right"),sQuery(id+"F10.wireOp",EDGE,"E118"),sQuery(id+"F10.wireOp",EDGE,"E120"),sQuery(id+"F10.wireOp",EDGE,"E121")])],"isStart":true});
            var sketch = newSketch(context, id + "F28", { "sketchPlane" : qUnion([Q0])});
            skCircle(sketch, "E188", {"center": v(-34, 120) * mm, "radius": 18 * mm});
            skCircle(sketch, "E189", {"center": v(-34, 120) * mm, "radius": 2.5 * mm});
            skSolve(sketch);
        }
        {
            var Q0;
            Q0 = qSketchRegion(id + "F28", true);
            extrude(context, id + "F29", {"entities" : qUnion([Q0]), "depth" : 6 * mm});
        }
        {
            var Q0;
            Q0=makeQuery(id+"F11.opExtrude","CAP_FACE",FACE,{"disambiguationData":[OSD([sQuery(id+"F10.wireOp",EDGE,"E114.bottom"),sQuery(id+"F10.wireOp",EDGE,"E114.top"),sQuery(id+"F10.wireOp",EDGE,"E114.left"),sQuery(id+"F10.wireOp",EDGE,"E114.right"),sQuery(id+"F10.wireOp",EDGE,"E115.top"),sQuery(id+"F10.wireOp",EDGE,"E115.right"),sQuery(id+"F10.wireOp",EDGE,"E116.top"),sQuery(id+"F10.wireOp",EDGE,"E116.right"),sQuery(id+"F10.wireOp",EDGE,"E118"),sQuery(id+"F10.wireOp",EDGE,"E120"),sQuery(id+"F10.wireOp",EDGE,"E121")])],"isStart":true});
            var sketch = newSketch(context, id + "F30", { "sketchPlane" : qUnion([Q0])});
            skCircle(sketch, "E190", {"center": v(2, 120) * mm, "radius": 18 * mm});
            skCircle(sketch, "E191", {"center": v(2, 120) * mm, "radius": 2.5 * mm});
            skSolve(sketch);
        }
        {
            var Q0;
            Q0 = qSketchRegion(id + "F30", true);
            extrude(context, id + "F31", {"entities" : qUnion([Q0]), "depth" : 6 * mm});
        }
        {
            var Q0;
            Q0=makeQuery(id+"F9.opExtrude","CAP_FACE",FACE,{"disambiguationData":[OSD([sQuery(id+"F8.wireOp",EDGE,"E102.rect.bottom"),sQuery(id+"F8.wireOp",EDGE,"E102.rect.top"),sQuery(id+"F8.wireOp",EDGE,"E102.rect.left"),sQuery(id+"F8.wireOp",EDGE,"E102.rect.right"),sQuery(id+"F8.wireOp",EDGE,"E103"),sQuery(id+"F8.wireOp",EDGE,"E104"),sQuery(id+"F8.wireOp",EDGE,"E105"),sQuery(id+"F8.wireOp",EDGE,"E106"),sQuery(id+"F8.wireOp",EDGE,"E107"),sQuery(id+"F8.wireOp",EDGE,"E112"),sQuery(id+"F8.wireOp",EDGE,"E113")])],"isStart":true});
            var sketch = newSketch(context, id + "F32", { "sketchPlane" : qUnion([Q0])});
            skCircle(sketch, "E192", {"center": v(35.76, 120) * mm, "radius": 18 * mm});
            skCircle(sketch, "E193", {"center": v(35.76, 120) * mm, "radius": 2.5 * mm});
            skSolve(sketch);
        }
        {
            var Q0;
            Q0 = qSketchRegion(id + "F32", true);
            extrude(context, id + "F33", {"entities" : qUnion([Q0]), "depth" : 6 * mm});
        }
        {
            var Q0;
            Q0=qCreatedBy(makeId("Front.planeOp"),FACE);
            var sketch = newSketch(context, id + "F34", { "sketchPlane" : qUnion([Q0])});
            skCircle(sketch, "E194", {"center": v(0, -22.34) * mm, "radius": 16.4 * mm, "construction": true});
            skCircle(sketch, "E195", {"center": v(0, -22.34) * mm, "radius": 19.4 * mm, "construction": true});
            skLineSegment(sketch, "E196", {"start": v(0, -22.34) * mm, "end": v(0, -2.94) * mm, "construction": true});
            skLineSegment(sketch, "E197", {"start": v(0, -22.34) * mm, "end": v(-0.42, -2.94) * mm, "construction": true});
            skLineSegment(sketch, "E198", {"start": v(0, -22.34) * mm, "end": v(-0.85, -2.96) * mm, "construction": true});
            skLineSegment(sketch, "E199", {"start": v(0, -22.34) * mm, "end": v(-1.27, -2.98) * mm, "construction": true});
            skLineSegment(sketch, "E200", {"start": v(0, -22.34) * mm, "end": v(-1.7, -3.01) * mm, "construction": true});
            skLineSegment(sketch, "E201", {"start": v(0, -22.34) * mm, "end": v(-2.11, -3.05) * mm, "construction": true});
            skLineSegment(sketch, "E202", {"start": v(0, -22.34) * mm, "end": v(-2.53, -3.1) * mm, "construction": true});
            skLineSegment(sketch, "E203", {"start": v(0, -22.34) * mm, "end": v(-2.95, -3.16) * mm, "construction": true});
            skLineSegment(sketch, "E204", {"start": v(0, -22.34) * mm, "end": v(-3.37, -3.23) * mm, "construction": true});
            skArc(sketch, "E205", {"start": v(-1.27, -2.98) * mm, "mid": v(-1.7, -3.01) * mm, "end": v(-2.11, -3.05) * mm});
            skLineSegment(sketch, "E206", {"start": v(-1.27, -2.98) * mm, "end": v(-0.36, -5.94) * mm});
            skLineSegment(sketch, "E207", {"start": v(-0.36, -5.94) * mm, "end": v(0, -5.93) * mm});
            skLineSegment(sketch, "E208", {"start": v(-2.11, -3.05) * mm, "end": v(-2.5, -6.13) * mm});
            skLineSegment(sketch, "E209", {"start": v(-2.5, -6.13) * mm, "end": v(-2.85, -6.18) * mm});
            skLineSegment(sketch, "E210.1.0", {"start": v(-3.2, -6.25) * mm, "end": v(-2.85, -6.18) * mm});
            skLineSegment(sketch, "E210.1.1", {"start": v(-4.61, -3.5) * mm, "end": v(-3.2, -6.25) * mm});
            skArc(sketch, "E210.1.2", {"start": v(-4.61, -3.5) * mm, "mid": v(-5.02, -3.6) * mm, "end": v(-5.43, -3.71) * mm});
            skLineSegment(sketch, "E210.1.3", {"start": v(-5.43, -3.71) * mm, "end": v(-5.27, -6.8) * mm});
            skLineSegment(sketch, "E210.1.4", {"start": v(-5.27, -6.8) * mm, "end": v(-5.61, -6.92) * mm});
            skLineSegment(sketch, "E210.2.0", {"start": v(-5.94, -7.05) * mm, "end": v(-5.61, -6.92) * mm});
            skLineSegment(sketch, "E210.2.1", {"start": v(-7.81, -4.58) * mm, "end": v(-5.94, -7.05) * mm});
            skArc(sketch, "E210.2.2", {"start": v(-7.81, -4.58) * mm, "mid": v(-8.2, -4.75) * mm, "end": v(-8.58, -4.94) * mm});
            skLineSegment(sketch, "E210.2.3", {"start": v(-8.58, -4.94) * mm, "end": v(-7.89, -7.96) * mm});
            skLineSegment(sketch, "E210.2.4", {"start": v(-7.89, -7.96) * mm, "end": v(-8.2, -8.13) * mm});
            skLineSegment(sketch, "E210.3.0", {"start": v(-8.5, -8.32) * mm, "end": v(-8.2, -8.13) * mm});
            skLineSegment(sketch, "E210.3.1", {"start": v(-10.78, -6.2) * mm, "end": v(-8.5, -8.32) * mm});
            skArc(sketch, "E210.3.2", {"start": v(-10.78, -6.2) * mm, "mid": v(-11.13, -6.45) * mm, "end": v(-11.47, -6.7) * mm});
            skLineSegment(sketch, "E210.3.3", {"start": v(-11.47, -6.7) * mm, "end": v(-10.27, -9.55) * mm});
            skLineSegment(sketch, "E210.3.4", {"start": v(-10.27, -9.55) * mm, "end": v(-10.54, -9.77) * mm});
            skLineSegment(sketch, "E210.4.0", {"start": v(-10.81, -10) * mm, "end": v(-10.54, -9.77) * mm});
            skLineSegment(sketch, "E210.4.1", {"start": v(-13.42, -8.32) * mm, "end": v(-10.81, -10) * mm});
            skArc(sketch, "E210.4.2", {"start": v(-13.42, -8.32) * mm, "mid": v(-13.72, -8.62) * mm, "end": v(-14.01, -8.92) * mm});
            skLineSegment(sketch, "E210.4.3", {"start": v(-14.01, -8.92) * mm, "end": v(-12.33, -11.52) * mm});
            skLineSegment(sketch, "E210.4.4", {"start": v(-12.33, -11.52) * mm, "end": v(-12.57, -11.8) * mm});
            skLineSegment(sketch, "E210.5.0", {"start": v(-12.8, -12.07) * mm, "end": v(-12.57, -11.8) * mm});
            skLineSegment(sketch, "E210.5.1", {"start": v(-15.65, -10.87) * mm, "end": v(-12.8, -12.07) * mm});
            skArc(sketch, "E210.5.2", {"start": v(-15.65, -10.87) * mm, "mid": v(-15.9, -11.2) * mm, "end": v(-16.13, -11.56) * mm});
            skLineSegment(sketch, "E210.5.3", {"start": v(-16.13, -11.56) * mm, "end": v(-14.02, -13.83) * mm});
            skLineSegment(sketch, "E210.5.4", {"start": v(-14.02, -13.83) * mm, "end": v(-14.2, -14.13) * mm});
            skLineSegment(sketch, "E210.6.0", {"start": v(-14.38, -14.45) * mm, "end": v(-14.2, -14.13) * mm});
            skLineSegment(sketch, "E210.6.1", {"start": v(-17.4, -13.76) * mm, "end": v(-14.38, -14.45) * mm});
            skArc(sketch, "E210.6.2", {"start": v(-17.4, -13.76) * mm, "mid": v(-17.58, -14.14) * mm, "end": v(-17.76, -14.52) * mm});
            skLineSegment(sketch, "E210.6.3", {"start": v(-17.76, -14.52) * mm, "end": v(-15.28, -16.4) * mm});
            skLineSegment(sketch, "E210.6.4", {"start": v(-15.28, -16.4) * mm, "end": v(-15.41, -16.73) * mm});
            skLineSegment(sketch, "E210.7.0", {"start": v(-15.53, -17.07) * mm, "end": v(-15.41, -16.73) * mm});
            skLineSegment(sketch, "E210.7.1", {"start": v(-18.62, -16.9) * mm, "end": v(-15.53, -17.07) * mm});
            skArc(sketch, "E210.7.2", {"start": v(-18.62, -16.9) * mm, "mid": v(-18.74, -17.32) * mm, "end": v(-18.84, -17.73) * mm});
            skLineSegment(sketch, "E210.7.3", {"start": v(-18.84, -17.73) * mm, "end": v(-16.08, -19.14) * mm});
            skLineSegment(sketch, "E210.7.4", {"start": v(-16.08, -19.14) * mm, "end": v(-16.15, -19.49) * mm});
            skLineSegment(sketch, "E210.8.0", {"start": v(-16.2, -19.84) * mm, "end": v(-16.15, -19.49) * mm});
            skLineSegment(sketch, "E210.8.1", {"start": v(-19.28, -20.22) * mm, "end": v(-16.2, -19.84) * mm});
            skArc(sketch, "E210.8.2", {"start": v(-19.28, -20.22) * mm, "mid": v(-19.33, -20.65) * mm, "end": v(-19.36, -21.07) * mm});
            skLineSegment(sketch, "E210.8.3", {"start": v(-19.36, -21.07) * mm, "end": v(-16.4, -21.98) * mm});
            skLineSegment(sketch, "E210.8.4", {"start": v(-16.4, -21.98) * mm, "end": v(-16.4, -22.34) * mm});
            skLineSegment(sketch, "E210.9.0", {"start": v(-16.4, -22.7) * mm, "end": v(-16.4, -22.34) * mm});
            skLineSegment(sketch, "E210.9.1", {"start": v(-19.36, -23.6) * mm, "end": v(-16.4, -22.7) * mm});
            skArc(sketch, "E210.9.2", {"start": v(-19.36, -23.6) * mm, "mid": v(-19.33, -24.03) * mm, "end": v(-19.28, -24.45) * mm});
            skLineSegment(sketch, "E210.9.3", {"start": v(-19.28, -24.45) * mm, "end": v(-16.2, -24.83) * mm});
            skLineSegment(sketch, "E210.9.4", {"start": v(-16.2, -24.83) * mm, "end": v(-16.15, -25.19) * mm});
            skLineSegment(sketch, "E210.10.0", {"start": v(-16.08, -25.54) * mm, "end": v(-16.15, -25.19) * mm});
            skLineSegment(sketch, "E210.10.1", {"start": v(-18.84, -26.95) * mm, "end": v(-16.08, -25.54) * mm});
            skArc(sketch, "E210.10.2", {"start": v(-18.84, -26.95) * mm, "mid": v(-18.74, -27.36) * mm, "end": v(-18.62, -27.77) * mm});
            skLineSegment(sketch, "E210.10.3", {"start": v(-18.62, -27.77) * mm, "end": v(-15.53, -27.6) * mm});
            skLineSegment(sketch, "E210.10.4", {"start": v(-15.53, -27.6) * mm, "end": v(-15.41, -27.95) * mm});
            skLineSegment(sketch, "E210.11.0", {"start": v(-15.28, -28.28) * mm, "end": v(-15.41, -27.95) * mm});
            skLineSegment(sketch, "E210.11.1", {"start": v(-17.76, -30.15) * mm, "end": v(-15.28, -28.28) * mm});
            skArc(sketch, "E210.11.2", {"start": v(-17.76, -30.15) * mm, "mid": v(-17.58, -30.54) * mm, "end": v(-17.4, -30.92) * mm});
            skLineSegment(sketch, "E210.11.3", {"start": v(-17.4, -30.92) * mm, "end": v(-14.38, -30.23) * mm});
            skLineSegment(sketch, "E210.11.4", {"start": v(-14.38, -30.23) * mm, "end": v(-14.2, -30.54) * mm});
            skLineSegment(sketch, "E210.12.0", {"start": v(-14.02, -30.84) * mm, "end": v(-14.2, -30.54) * mm});
            skLineSegment(sketch, "E210.12.1", {"start": v(-16.13, -33.11) * mm, "end": v(-14.02, -30.84) * mm});
            skArc(sketch, "E210.12.2", {"start": v(-16.13, -33.11) * mm, "mid": v(-15.9, -33.46) * mm, "end": v(-15.65, -33.8) * mm});
            skLineSegment(sketch, "E210.12.3", {"start": v(-15.65, -33.8) * mm, "end": v(-12.8, -32.6) * mm});
            skLineSegment(sketch, "E210.12.4", {"start": v(-12.8, -32.6) * mm, "end": v(-12.57, -32.88) * mm});
            skLineSegment(sketch, "E210.13.0", {"start": v(-12.33, -33.15) * mm, "end": v(-12.57, -32.88) * mm});
            skLineSegment(sketch, "E210.13.1", {"start": v(-14.01, -35.75) * mm, "end": v(-12.33, -33.15) * mm});
            skArc(sketch, "E210.13.2", {"start": v(-14.01, -35.75) * mm, "mid": v(-13.72, -36.05) * mm, "end": v(-13.42, -36.35) * mm});
            skLineSegment(sketch, "E210.13.3", {"start": v(-13.42, -36.35) * mm, "end": v(-10.81, -34.67) * mm});
            skLineSegment(sketch, "E210.13.4", {"start": v(-10.81, -34.67) * mm, "end": v(-10.54, -34.9) * mm});
            skLineSegment(sketch, "E210.14.0", {"start": v(-10.27, -35.13) * mm, "end": v(-10.54, -34.9) * mm});
            skLineSegment(sketch, "E210.14.1", {"start": v(-11.47, -37.98) * mm, "end": v(-10.27, -35.13) * mm});
            skArc(sketch, "E210.14.2", {"start": v(-11.47, -37.98) * mm, "mid": v(-11.13, -38.23) * mm, "end": v(-10.78, -38.47) * mm});
            skLineSegment(sketch, "E210.14.3", {"start": v(-10.78, -38.47) * mm, "end": v(-8.5, -36.36) * mm});
            skLineSegment(sketch, "E210.14.4", {"start": v(-8.5, -36.36) * mm, "end": v(-8.2, -36.54) * mm});
            skLineSegment(sketch, "E210.15.0", {"start": v(-7.89, -36.72) * mm, "end": v(-8.2, -36.54) * mm});
            skLineSegment(sketch, "E210.15.1", {"start": v(-8.58, -39.74) * mm, "end": v(-7.89, -36.72) * mm});
            skArc(sketch, "E210.15.2", {"start": v(-8.58, -39.74) * mm, "mid": v(-8.2, -39.92) * mm, "end": v(-7.81, -40.1) * mm});
            skLineSegment(sketch, "E210.15.3", {"start": v(-7.81, -40.1) * mm, "end": v(-5.94, -37.62) * mm});
            skLineSegment(sketch, "E210.15.4", {"start": v(-5.94, -37.62) * mm, "end": v(-5.61, -37.75) * mm});
            skLineSegment(sketch, "E210.16.0", {"start": v(-5.27, -37.87) * mm, "end": v(-5.61, -37.75) * mm});
            skLineSegment(sketch, "E210.16.1", {"start": v(-5.43, -40.96) * mm, "end": v(-5.27, -37.87) * mm});
            skArc(sketch, "E210.16.2", {"start": v(-5.43, -40.96) * mm, "mid": v(-5.02, -41.08) * mm, "end": v(-4.61, -41.18) * mm});
            skLineSegment(sketch, "E210.16.3", {"start": v(-4.61, -41.18) * mm, "end": v(-3.2, -38.42) * mm});
            skLineSegment(sketch, "E210.16.4", {"start": v(-3.2, -38.42) * mm, "end": v(-2.85, -38.5) * mm});
            skLineSegment(sketch, "E210.17.0", {"start": v(-2.5, -38.55) * mm, "end": v(-2.85, -38.5) * mm});
            skLineSegment(sketch, "E210.17.1", {"start": v(-2.11, -41.62) * mm, "end": v(-2.5, -38.55) * mm});
            skArc(sketch, "E210.17.2", {"start": v(-2.11, -41.62) * mm, "mid": v(-1.7, -41.66) * mm, "end": v(-1.27, -41.7) * mm});
            skLineSegment(sketch, "E210.17.3", {"start": v(-1.27, -41.7) * mm, "end": v(-0.36, -38.73) * mm});
            skLineSegment(sketch, "E210.17.4", {"start": v(-0.36, -38.73) * mm, "end": v(0, -38.74) * mm});
            skLineSegment(sketch, "E210.18.0", {"start": v(0.36, -38.73) * mm, "end": v(0, -38.74) * mm});
            skLineSegment(sketch, "E210.18.1", {"start": v(1.27, -41.7) * mm, "end": v(0.36, -38.73) * mm});
            skArc(sketch, "E210.18.2", {"start": v(1.27, -41.7) * mm, "mid": v(1.7, -41.66) * mm, "end": v(2.11, -41.62) * mm});
            skLineSegment(sketch, "E210.18.3", {"start": v(2.11, -41.62) * mm, "end": v(2.5, -38.55) * mm});
            skLineSegment(sketch, "E210.18.4", {"start": v(2.5, -38.55) * mm, "end": v(2.85, -38.5) * mm});
            skLineSegment(sketch, "E210.19.0", {"start": v(3.2, -38.42) * mm, "end": v(2.85, -38.5) * mm});
            skLineSegment(sketch, "E210.19.1", {"start": v(4.61, -41.18) * mm, "end": v(3.2, -38.42) * mm});
            skArc(sketch, "E210.19.2", {"start": v(4.61, -41.18) * mm, "mid": v(5.02, -41.08) * mm, "end": v(5.43, -40.96) * mm});
            skLineSegment(sketch, "E210.19.3", {"start": v(5.43, -40.96) * mm, "end": v(5.27, -37.87) * mm});
            skLineSegment(sketch, "E210.19.4", {"start": v(5.27, -37.87) * mm, "end": v(5.61, -37.75) * mm});
            skLineSegment(sketch, "E210.20.0", {"start": v(5.94, -37.62) * mm, "end": v(5.61, -37.75) * mm});
            skLineSegment(sketch, "E210.20.1", {"start": v(7.81, -40.1) * mm, "end": v(5.94, -37.62) * mm});
            skArc(sketch, "E210.20.2", {"start": v(7.81, -40.1) * mm, "mid": v(8.2, -39.92) * mm, "end": v(8.58, -39.74) * mm});
            skLineSegment(sketch, "E210.20.3", {"start": v(8.58, -39.74) * mm, "end": v(7.89, -36.72) * mm});
            skLineSegment(sketch, "E210.20.4", {"start": v(7.89, -36.72) * mm, "end": v(8.2, -36.54) * mm});
            skLineSegment(sketch, "E210.21.0", {"start": v(8.5, -36.36) * mm, "end": v(8.2, -36.54) * mm});
            skLineSegment(sketch, "E210.21.1", {"start": v(10.78, -38.47) * mm, "end": v(8.5, -36.36) * mm});
            skArc(sketch, "E210.21.2", {"start": v(10.78, -38.47) * mm, "mid": v(11.13, -38.23) * mm, "end": v(11.47, -37.98) * mm});
            skLineSegment(sketch, "E210.21.3", {"start": v(11.47, -37.98) * mm, "end": v(10.27, -35.13) * mm});
            skLineSegment(sketch, "E210.21.4", {"start": v(10.27, -35.13) * mm, "end": v(10.54, -34.9) * mm});
            skLineSegment(sketch, "E210.22.0", {"start": v(10.81, -34.67) * mm, "end": v(10.54, -34.9) * mm});
            skLineSegment(sketch, "E210.22.1", {"start": v(13.42, -36.35) * mm, "end": v(10.81, -34.67) * mm});
            skArc(sketch, "E210.22.2", {"start": v(13.42, -36.35) * mm, "mid": v(13.72, -36.05) * mm, "end": v(14.01, -35.75) * mm});
            skLineSegment(sketch, "E210.22.3", {"start": v(14.01, -35.75) * mm, "end": v(12.33, -33.15) * mm});
            skLineSegment(sketch, "E210.22.4", {"start": v(12.33, -33.15) * mm, "end": v(12.57, -32.88) * mm});
            skLineSegment(sketch, "E210.23.0", {"start": v(12.8, -32.6) * mm, "end": v(12.57, -32.88) * mm});
            skLineSegment(sketch, "E210.23.1", {"start": v(15.65, -33.8) * mm, "end": v(12.8, -32.6) * mm});
            skArc(sketch, "E210.23.2", {"start": v(15.65, -33.8) * mm, "mid": v(15.9, -33.46) * mm, "end": v(16.13, -33.11) * mm});
            skLineSegment(sketch, "E210.23.3", {"start": v(16.13, -33.11) * mm, "end": v(14.02, -30.84) * mm});
            skLineSegment(sketch, "E210.23.4", {"start": v(14.02, -30.84) * mm, "end": v(14.2, -30.54) * mm});
            skLineSegment(sketch, "E210.24.0", {"start": v(14.38, -30.23) * mm, "end": v(14.2, -30.54) * mm});
            skLineSegment(sketch, "E210.24.1", {"start": v(17.4, -30.92) * mm, "end": v(14.38, -30.23) * mm});
            skArc(sketch, "E210.24.2", {"start": v(17.4, -30.92) * mm, "mid": v(17.58, -30.54) * mm, "end": v(17.76, -30.15) * mm});
            skLineSegment(sketch, "E210.24.3", {"start": v(17.76, -30.15) * mm, "end": v(15.28, -28.28) * mm});
            skLineSegment(sketch, "E210.24.4", {"start": v(15.28, -28.28) * mm, "end": v(15.41, -27.95) * mm});
            skLineSegment(sketch, "E210.25.0", {"start": v(15.53, -27.6) * mm, "end": v(15.41, -27.95) * mm});
            skLineSegment(sketch, "E210.25.1", {"start": v(18.62, -27.77) * mm, "end": v(15.53, -27.6) * mm});
            skArc(sketch, "E210.25.2", {"start": v(18.62, -27.77) * mm, "mid": v(18.74, -27.36) * mm, "end": v(18.84, -26.95) * mm});
            skLineSegment(sketch, "E210.25.3", {"start": v(18.84, -26.95) * mm, "end": v(16.08, -25.54) * mm});
            skLineSegment(sketch, "E210.25.4", {"start": v(16.08, -25.54) * mm, "end": v(16.15, -25.19) * mm});
            skLineSegment(sketch, "E210.26.0", {"start": v(16.2, -24.83) * mm, "end": v(16.15, -25.19) * mm});
            skLineSegment(sketch, "E210.26.1", {"start": v(19.28, -24.45) * mm, "end": v(16.2, -24.83) * mm});
            skArc(sketch, "E210.26.2", {"start": v(19.28, -24.45) * mm, "mid": v(19.33, -24.03) * mm, "end": v(19.36, -23.6) * mm});
            skLineSegment(sketch, "E210.26.3", {"start": v(19.36, -23.6) * mm, "end": v(16.4, -22.7) * mm});
            skLineSegment(sketch, "E210.26.4", {"start": v(16.4, -22.7) * mm, "end": v(16.4, -22.34) * mm});
            skLineSegment(sketch, "E210.27.0", {"start": v(16.4, -21.98) * mm, "end": v(16.4, -22.34) * mm});
            skLineSegment(sketch, "E210.27.1", {"start": v(19.36, -21.07) * mm, "end": v(16.4, -21.98) * mm});
            skArc(sketch, "E210.27.2", {"start": v(19.36, -21.07) * mm, "mid": v(19.33, -20.65) * mm, "end": v(19.28, -20.22) * mm});
            skLineSegment(sketch, "E210.27.3", {"start": v(19.28, -20.22) * mm, "end": v(16.2, -19.84) * mm});
            skLineSegment(sketch, "E210.27.4", {"start": v(16.2, -19.84) * mm, "end": v(16.15, -19.49) * mm});
            skLineSegment(sketch, "E210.28.0", {"start": v(16.08, -19.14) * mm, "end": v(16.15, -19.49) * mm});
            skLineSegment(sketch, "E210.28.1", {"start": v(18.84, -17.73) * mm, "end": v(16.08, -19.14) * mm});
            skArc(sketch, "E210.28.2", {"start": v(18.84, -17.73) * mm, "mid": v(18.74, -17.32) * mm, "end": v(18.62, -16.9) * mm});
            skLineSegment(sketch, "E210.28.3", {"start": v(18.62, -16.9) * mm, "end": v(15.53, -17.07) * mm});
            skLineSegment(sketch, "E210.28.4", {"start": v(15.53, -17.07) * mm, "end": v(15.41, -16.73) * mm});
            skLineSegment(sketch, "E210.29.0", {"start": v(15.28, -16.4) * mm, "end": v(15.41, -16.73) * mm});
            skLineSegment(sketch, "E210.29.1", {"start": v(17.76, -14.52) * mm, "end": v(15.28, -16.4) * mm});
            skArc(sketch, "E210.29.2", {"start": v(17.76, -14.52) * mm, "mid": v(17.58, -14.14) * mm, "end": v(17.4, -13.76) * mm});
            skLineSegment(sketch, "E210.29.3", {"start": v(17.4, -13.76) * mm, "end": v(14.38, -14.45) * mm});
            skLineSegment(sketch, "E210.29.4", {"start": v(14.38, -14.45) * mm, "end": v(14.2, -14.13) * mm});
            skLineSegment(sketch, "E210.30.0", {"start": v(14.02, -13.83) * mm, "end": v(14.2, -14.13) * mm});
            skLineSegment(sketch, "E210.30.1", {"start": v(16.13, -11.56) * mm, "end": v(14.02, -13.83) * mm});
            skArc(sketch, "E210.30.2", {"start": v(16.13, -11.56) * mm, "mid": v(15.9, -11.2) * mm, "end": v(15.65, -10.87) * mm});
            skLineSegment(sketch, "E210.30.3", {"start": v(15.65, -10.87) * mm, "end": v(12.8, -12.07) * mm});
            skLineSegment(sketch, "E210.30.4", {"start": v(12.8, -12.07) * mm, "end": v(12.57, -11.8) * mm});
            skLineSegment(sketch, "E210.31.0", {"start": v(12.33, -11.52) * mm, "end": v(12.57, -11.8) * mm});
            skLineSegment(sketch, "E210.31.1", {"start": v(14.01, -8.92) * mm, "end": v(12.33, -11.52) * mm});
            skArc(sketch, "E210.31.2", {"start": v(14.01, -8.92) * mm, "mid": v(13.72, -8.62) * mm, "end": v(13.42, -8.32) * mm});
            skLineSegment(sketch, "E210.31.3", {"start": v(13.42, -8.32) * mm, "end": v(10.81, -10) * mm});
            skLineSegment(sketch, "E210.31.4", {"start": v(10.81, -10) * mm, "end": v(10.54, -9.77) * mm});
            skLineSegment(sketch, "E210.32.0", {"start": v(10.27, -9.55) * mm, "end": v(10.54, -9.77) * mm});
            skLineSegment(sketch, "E210.32.1", {"start": v(11.47, -6.7) * mm, "end": v(10.27, -9.55) * mm});
            skArc(sketch, "E210.32.2", {"start": v(11.47, -6.7) * mm, "mid": v(11.13, -6.45) * mm, "end": v(10.78, -6.2) * mm});
            skLineSegment(sketch, "E210.32.3", {"start": v(10.78, -6.2) * mm, "end": v(8.5, -8.32) * mm});
            skLineSegment(sketch, "E210.32.4", {"start": v(8.5, -8.32) * mm, "end": v(8.2, -8.13) * mm});
            skLineSegment(sketch, "E210.33.0", {"start": v(7.89, -7.96) * mm, "end": v(8.2, -8.13) * mm});
            skLineSegment(sketch, "E210.33.1", {"start": v(8.58, -4.94) * mm, "end": v(7.89, -7.96) * mm});
            skArc(sketch, "E210.33.2", {"start": v(8.58, -4.94) * mm, "mid": v(8.2, -4.75) * mm, "end": v(7.81, -4.58) * mm});
            skLineSegment(sketch, "E210.33.3", {"start": v(7.81, -4.58) * mm, "end": v(5.94, -7.05) * mm});
            skLineSegment(sketch, "E210.33.4", {"start": v(5.94, -7.05) * mm, "end": v(5.61, -6.92) * mm});
            skLineSegment(sketch, "E210.34.0", {"start": v(5.27, -6.8) * mm, "end": v(5.61, -6.92) * mm});
            skLineSegment(sketch, "E210.34.1", {"start": v(5.43, -3.71) * mm, "end": v(5.27, -6.8) * mm});
            skArc(sketch, "E210.34.2", {"start": v(5.43, -3.71) * mm, "mid": v(5.02, -3.6) * mm, "end": v(4.61, -3.5) * mm});
            skLineSegment(sketch, "E210.34.3", {"start": v(4.61, -3.5) * mm, "end": v(3.2, -6.25) * mm});
            skLineSegment(sketch, "E210.34.4", {"start": v(3.2, -6.25) * mm, "end": v(2.85, -6.18) * mm});
            skLineSegment(sketch, "E210.35.0", {"start": v(2.5, -6.13) * mm, "end": v(2.85, -6.18) * mm});
            skLineSegment(sketch, "E210.35.1", {"start": v(2.11, -3.05) * mm, "end": v(2.5, -6.13) * mm});
            skArc(sketch, "E210.35.2", {"start": v(2.11, -3.05) * mm, "mid": v(1.7, -3.01) * mm, "end": v(1.27, -2.98) * mm});
            skLineSegment(sketch, "E210.35.3", {"start": v(1.27, -2.98) * mm, "end": v(0.36, -5.94) * mm});
            skLineSegment(sketch, "E210.35.4", {"start": v(0.36, -5.94) * mm, "end": v(0, -5.93) * mm});
            skLineSegment(sketch, "E211", {"start": v(25.71, -45.04) * mm, "end": v(70.51, -45.04) * mm, "construction": true});
            skLineSegment(sketch, "E212", {"start": v(70.51, -45.04) * mm, "end": v(64.51, -39.04) * mm, "construction": true});
            skLineSegment(sketch, "E213", {"start": v(64.51, -39.04) * mm, "end": v(31.71, -39.04) * mm, "construction": true});
            skLineSegment(sketch, "E214", {"start": v(31.71, -39.04) * mm, "end": v(25.71, -45.04) * mm, "construction": true});
            skLineSegment(sketch, "E215", {"start": v(70.51, -45.04) * mm, "end": v(70.51, -0.24) * mm, "construction": true});
            skLineSegment(sketch, "E216", {"start": v(70.51, -0.24) * mm, "end": v(64.51, -6.24) * mm, "construction": true});
            skLineSegment(sketch, "E217", {"start": v(64.51, -6.24) * mm, "end": v(64.51, -39.04) * mm, "construction": true});
            skSolve(sketch);
        }
        {
            var Q0;
            Q0=qCreatedBy(makeId("Front.planeOp"),FACE);
            cPlane(context, id + "F35", {"entities" : qUnion([Q0]), "cplaneType" : CPlaneType.OFFSET, "offset" : 6 * mm, "oppositeDirection" : true, "width" : 150 * mm, "height" : 150 * mm});
        }
        {
            var Q0;
            Q0=qCreatedBy(id+"F35.planeOp",FACE);
            var sketch = newSketch(context, id + "F36", { "sketchPlane" : qUnion([Q0])});
            skCircle(sketch, "E218", {"center": v(0, -22.34) * mm, "radius": 22.4 * mm, "construction": true});
            skCircle(sketch, "E219", {"center": v(0, -22.34) * mm, "radius": 25.4 * mm, "construction": true});
            skLineSegment(sketch, "E220", {"start": v(0, -22.34) * mm, "end": v(0, 3.06) * mm, "construction": true});
            skLineSegment(sketch, "E221", {"start": v(0, -22.34) * mm, "end": v(-0.55, 3.06) * mm, "construction": true});
            skLineSegment(sketch, "E222", {"start": v(0, -22.34) * mm, "end": v(-1.1, 3.04) * mm, "construction": true});
            skLineSegment(sketch, "E223", {"start": v(0, -22.34) * mm, "end": v(-1.66, 3) * mm, "construction": true});
            skLineSegment(sketch, "E224", {"start": v(0, -22.34) * mm, "end": v(-2.21, 2.97) * mm, "construction": true});
            skLineSegment(sketch, "E225", {"start": v(0, -22.34) * mm, "end": v(-2.77, 2.91) * mm, "construction": true});
            skLineSegment(sketch, "E226", {"start": v(0, -22.34) * mm, "end": v(-3.32, 2.85) * mm, "construction": true});
            skLineSegment(sketch, "E227", {"start": v(0, -22.34) * mm, "end": v(-3.86, 2.77) * mm, "construction": true});
            skLineSegment(sketch, "E228", {"start": v(0, -22.34) * mm, "end": v(-4.41, 2.68) * mm, "construction": true});
            skArc(sketch, "E229", {"start": v(-1.66, 3) * mm, "mid": v(-2.21, 2.97) * mm, "end": v(-2.77, 2.91) * mm});
            skLineSegment(sketch, "E230", {"start": v(-1.66, 3) * mm, "end": v(-0.49, 0.06) * mm});
            skLineSegment(sketch, "E231", {"start": v(-0.49, 0.06) * mm, "end": v(0, 0.07) * mm});
            skLineSegment(sketch, "E232", {"start": v(-2.77, 2.91) * mm, "end": v(-3.4, -0.2) * mm});
            skLineSegment(sketch, "E233", {"start": v(-3.4, -0.2) * mm, "end": v(-3.9, -0.27) * mm});
            skArc(sketch, "E234.1.0", {"start": v(-6.04, 2.34) * mm, "mid": v(-6.57, 2.2) * mm, "end": v(-7.1, 2.05) * mm});
            skLineSegment(sketch, "E234.1.1", {"start": v(-7.1, 2.05) * mm, "end": v(-7.2, -1.13) * mm});
            skLineSegment(sketch, "E234.1.2", {"start": v(-6.04, 2.34) * mm, "end": v(-4.37, -0.37) * mm});
            skLineSegment(sketch, "E234.1.3", {"start": v(-7.2, -1.13) * mm, "end": v(-7.66, -1.28) * mm});
            skLineSegment(sketch, "E234.1.4", {"start": v(-4.37, -0.37) * mm, "end": v(-3.9, -0.27) * mm});
            skArc(sketch, "E234.2.0", {"start": v(-10.23, 0.91) * mm, "mid": v(-10.73, 0.68) * mm, "end": v(-11.23, 0.44) * mm});
            skLineSegment(sketch, "E234.2.1", {"start": v(-11.23, 0.44) * mm, "end": v(-10.77, -2.7) * mm});
            skLineSegment(sketch, "E234.2.2", {"start": v(-10.23, 0.91) * mm, "end": v(-8.12, -1.46) * mm});
            skLineSegment(sketch, "E234.2.3", {"start": v(-10.77, -2.7) * mm, "end": v(-11.2, -2.93) * mm});
            skLineSegment(sketch, "E234.2.4", {"start": v(-8.12, -1.46) * mm, "end": v(-7.66, -1.28) * mm});
            skLineSegment(sketch, "E235.4.3.0", {"start": v(-15.02, -1.85) * mm, "end": v(-14.02, -4.87) * mm});
            skLineSegment(sketch, "E235.7.3.0", {"start": v(-14.11, -1.22) * mm, "end": v(-11.62, -3.19) * mm});
            skLineSegment(sketch, "E235.10.3.0", {"start": v(-14.02, -4.87) * mm, "end": v(-14.4, -5.17) * mm});
            skLineSegment(sketch, "E235.13.3.0", {"start": v(-11.62, -3.19) * mm, "end": v(-11.2, -2.93) * mm});
            skArc(sketch, "E235.15.3.0", {"start": v(-14.11, -1.22) * mm, "mid": v(-14.57, -1.53) * mm, "end": v(-15.02, -1.85) * mm});
            skLineSegment(sketch, "E235.4.4.0", {"start": v(-18.35, -4.77) * mm, "end": v(-16.84, -7.57) * mm});
            skLineSegment(sketch, "E235.7.4.0", {"start": v(-17.56, -3.99) * mm, "end": v(-14.77, -5.5) * mm});
            skLineSegment(sketch, "E235.10.4.0", {"start": v(-16.84, -7.57) * mm, "end": v(-17.16, -7.94) * mm});
            skLineSegment(sketch, "E235.13.4.0", {"start": v(-14.77, -5.5) * mm, "end": v(-14.4, -5.17) * mm});
            skArc(sketch, "E235.15.4.0", {"start": v(-17.56, -3.99) * mm, "mid": v(-17.96, -4.38) * mm, "end": v(-18.35, -4.77) * mm});
            skLineSegment(sketch, "E235.4.5.0", {"start": v(-21.12, -8.23) * mm, "end": v(-19.15, -10.72) * mm});
            skLineSegment(sketch, "E235.7.5.0", {"start": v(-20.48, -7.32) * mm, "end": v(-17.47, -8.32) * mm});
            skLineSegment(sketch, "E235.10.5.0", {"start": v(-19.15, -10.72) * mm, "end": v(-19.4, -11.13) * mm});
            skLineSegment(sketch, "E235.13.5.0", {"start": v(-17.47, -8.32) * mm, "end": v(-17.16, -7.94) * mm});
            skArc(sketch, "E235.15.5.0", {"start": v(-20.48, -7.32) * mm, "mid": v(-20.8, -7.77) * mm, "end": v(-21.12, -8.23) * mm});
            skLineSegment(sketch, "E235.4.6.0", {"start": v(-23.25, -12.1) * mm, "end": v(-20.88, -14.22) * mm});
            skLineSegment(sketch, "E235.7.6.0", {"start": v(-22.78, -11.1) * mm, "end": v(-19.64, -11.56) * mm});
            skLineSegment(sketch, "E235.10.6.0", {"start": v(-20.88, -14.22) * mm, "end": v(-21.05, -14.67) * mm});
            skLineSegment(sketch, "E235.13.6.0", {"start": v(-19.64, -11.56) * mm, "end": v(-19.4, -11.13) * mm});
            skArc(sketch, "E235.15.6.0", {"start": v(-22.78, -11.1) * mm, "mid": v(-23.02, -11.6) * mm, "end": v(-23.25, -12.1) * mm});
            skLineSegment(sketch, "E235.4.7.0", {"start": v(-24.67, -16.3) * mm, "end": v(-21.97, -17.97) * mm});
            skLineSegment(sketch, "E235.7.7.0", {"start": v(-24.39, -15.23) * mm, "end": v(-21.21, -15.14) * mm});
            skLineSegment(sketch, "E235.10.7.0", {"start": v(-21.97, -17.97) * mm, "end": v(-22.06, -18.45) * mm});
            skLineSegment(sketch, "E235.13.7.0", {"start": v(-21.21, -15.14) * mm, "end": v(-21.05, -14.67) * mm});
            skArc(sketch, "E235.15.7.0", {"start": v(-24.39, -15.23) * mm, "mid": v(-24.53, -15.76) * mm, "end": v(-24.67, -16.3) * mm});
            skLineSegment(sketch, "E235.4.8.0", {"start": v(-25.35, -20.68) * mm, "end": v(-22.4, -21.85) * mm});
            skLineSegment(sketch, "E235.7.8.0", {"start": v(-25.25, -19.57) * mm, "end": v(-22.14, -18.93) * mm});
            skLineSegment(sketch, "E235.10.8.0", {"start": v(-22.4, -21.85) * mm, "end": v(-22.4, -22.34) * mm});
            skLineSegment(sketch, "E235.13.8.0", {"start": v(-22.14, -18.93) * mm, "end": v(-22.06, -18.45) * mm});
            skArc(sketch, "E235.15.8.0", {"start": v(-25.25, -19.57) * mm, "mid": v(-25.3, -20.12) * mm, "end": v(-25.35, -20.68) * mm});
            skLineSegment(sketch, "E235.4.9.0", {"start": v(-25.25, -25.1) * mm, "end": v(-22.14, -25.74) * mm});
            skLineSegment(sketch, "E235.7.9.0", {"start": v(-25.35, -24) * mm, "end": v(-22.4, -22.83) * mm});
            skLineSegment(sketch, "E235.10.9.0", {"start": v(-22.14, -25.74) * mm, "end": v(-22.06, -26.23) * mm});
            skLineSegment(sketch, "E235.13.9.0", {"start": v(-22.4, -22.83) * mm, "end": v(-22.4, -22.34) * mm});
            skArc(sketch, "E235.15.9.0", {"start": v(-25.35, -24) * mm, "mid": v(-25.3, -24.55) * mm, "end": v(-25.25, -25.1) * mm});
            skLineSegment(sketch, "E235.4.10.0", {"start": v(-24.39, -29.44) * mm, "end": v(-21.21, -29.54) * mm});
            skLineSegment(sketch, "E235.7.10.0", {"start": v(-24.67, -28.37) * mm, "end": v(-21.97, -26.7) * mm});
            skLineSegment(sketch, "E235.10.10.0", {"start": v(-21.21, -29.54) * mm, "end": v(-21.05, -30) * mm});
            skLineSegment(sketch, "E235.13.10.0", {"start": v(-21.97, -26.7) * mm, "end": v(-22.06, -26.23) * mm});
            skArc(sketch, "E235.15.10.0", {"start": v(-24.67, -28.37) * mm, "mid": v(-24.53, -28.91) * mm, "end": v(-24.39, -29.44) * mm});
            skLineSegment(sketch, "E235.4.11.0", {"start": v(-22.78, -33.57) * mm, "end": v(-19.64, -33.11) * mm});
            skLineSegment(sketch, "E235.7.11.0", {"start": v(-23.25, -32.57) * mm, "end": v(-20.88, -30.46) * mm});
            skLineSegment(sketch, "E235.10.11.0", {"start": v(-19.64, -33.11) * mm, "end": v(-19.4, -33.54) * mm});
            skLineSegment(sketch, "E235.13.11.0", {"start": v(-20.88, -30.46) * mm, "end": v(-21.05, -30) * mm});
            skArc(sketch, "E235.15.11.0", {"start": v(-23.25, -32.57) * mm, "mid": v(-23.02, -33.07) * mm, "end": v(-22.78, -33.57) * mm});
            skLineSegment(sketch, "E235.4.12.0", {"start": v(-20.48, -37.36) * mm, "end": v(-17.47, -36.36) * mm});
            skLineSegment(sketch, "E235.7.12.0", {"start": v(-21.12, -36.45) * mm, "end": v(-19.15, -33.96) * mm});
            skLineSegment(sketch, "E235.10.12.0", {"start": v(-17.47, -36.36) * mm, "end": v(-17.16, -36.74) * mm});
            skLineSegment(sketch, "E235.13.12.0", {"start": v(-19.15, -33.96) * mm, "end": v(-19.4, -33.54) * mm});
            skArc(sketch, "E235.15.12.0", {"start": v(-21.12, -36.45) * mm, "mid": v(-20.8, -36.9) * mm, "end": v(-20.48, -37.36) * mm});
            skLineSegment(sketch, "E235.4.13.0", {"start": v(-17.56, -40.68) * mm, "end": v(-14.77, -39.18) * mm});
            skLineSegment(sketch, "E235.7.13.0", {"start": v(-18.35, -39.9) * mm, "end": v(-16.84, -37.1) * mm});
            skLineSegment(sketch, "E235.10.13.0", {"start": v(-14.77, -39.18) * mm, "end": v(-14.4, -39.5) * mm});
            skLineSegment(sketch, "E235.13.13.0", {"start": v(-16.84, -37.1) * mm, "end": v(-17.16, -36.74) * mm});
            skArc(sketch, "E235.15.13.0", {"start": v(-18.35, -39.9) * mm, "mid": v(-17.96, -40.3) * mm, "end": v(-17.56, -40.68) * mm});
            skLineSegment(sketch, "E235.4.14.0", {"start": v(-14.11, -43.46) * mm, "end": v(-11.62, -41.49) * mm});
            skLineSegment(sketch, "E235.7.14.0", {"start": v(-15.02, -42.82) * mm, "end": v(-14.02, -39.8) * mm});
            skLineSegment(sketch, "E235.10.14.0", {"start": v(-11.62, -41.49) * mm, "end": v(-11.2, -41.74) * mm});
            skLineSegment(sketch, "E235.13.14.0", {"start": v(-14.02, -39.8) * mm, "end": v(-14.4, -39.5) * mm});
            skArc(sketch, "E235.15.14.0", {"start": v(-15.02, -42.82) * mm, "mid": v(-14.57, -43.14) * mm, "end": v(-14.11, -43.46) * mm});
            skLineSegment(sketch, "E235.4.15.0", {"start": v(-10.23, -45.59) * mm, "end": v(-8.12, -43.21) * mm});
            skLineSegment(sketch, "E235.7.15.0", {"start": v(-11.23, -45.12) * mm, "end": v(-10.77, -41.98) * mm});
            skLineSegment(sketch, "E235.10.15.0", {"start": v(-8.12, -43.21) * mm, "end": v(-7.66, -43.4) * mm});
            skLineSegment(sketch, "E235.13.15.0", {"start": v(-10.77, -41.98) * mm, "end": v(-11.2, -41.74) * mm});
            skArc(sketch, "E235.15.15.0", {"start": v(-11.23, -45.12) * mm, "mid": v(-10.73, -45.36) * mm, "end": v(-10.23, -45.59) * mm});
            skLineSegment(sketch, "E235.4.16.0", {"start": v(-6.04, -47) * mm, "end": v(-4.37, -44.3) * mm});
            skLineSegment(sketch, "E235.7.16.0", {"start": v(-7.1, -46.72) * mm, "end": v(-7.2, -43.55) * mm});
            skLineSegment(sketch, "E235.10.16.0", {"start": v(-4.37, -44.3) * mm, "end": v(-3.9, -44.4) * mm});
            skLineSegment(sketch, "E235.13.16.0", {"start": v(-7.2, -43.55) * mm, "end": v(-7.66, -43.4) * mm});
            skArc(sketch, "E235.15.16.0", {"start": v(-7.1, -46.72) * mm, "mid": v(-6.57, -46.87) * mm, "end": v(-6.04, -47) * mm});
            skLineSegment(sketch, "E235.4.17.0", {"start": v(-1.66, -47.68) * mm, "end": v(-0.49, -44.73) * mm});
            skLineSegment(sketch, "E235.7.17.0", {"start": v(-2.77, -47.59) * mm, "end": v(-3.4, -44.48) * mm});
            skLineSegment(sketch, "E235.10.17.0", {"start": v(-0.49, -44.73) * mm, "end": v(0, -44.74) * mm});
            skLineSegment(sketch, "E235.13.17.0", {"start": v(-3.4, -44.48) * mm, "end": v(-3.9, -44.4) * mm});
            skArc(sketch, "E235.15.17.0", {"start": v(-2.77, -47.59) * mm, "mid": v(-2.21, -47.64) * mm, "end": v(-1.66, -47.68) * mm});
            skLineSegment(sketch, "E235.4.18.0", {"start": v(2.77, -47.59) * mm, "end": v(3.4, -44.48) * mm});
            skLineSegment(sketch, "E235.7.18.0", {"start": v(1.66, -47.68) * mm, "end": v(0.49, -44.73) * mm});
            skLineSegment(sketch, "E235.10.18.0", {"start": v(3.4, -44.48) * mm, "end": v(3.9, -44.4) * mm});
            skLineSegment(sketch, "E235.13.18.0", {"start": v(0.49, -44.73) * mm, "end": v(0, -44.74) * mm});
            skArc(sketch, "E235.15.18.0", {"start": v(1.66, -47.68) * mm, "mid": v(2.21, -47.64) * mm, "end": v(2.77, -47.59) * mm});
            skLineSegment(sketch, "E235.4.19.0", {"start": v(7.1, -46.72) * mm, "end": v(7.2, -43.55) * mm});
            skLineSegment(sketch, "E235.7.19.0", {"start": v(6.04, -47) * mm, "end": v(4.37, -44.3) * mm});
            skLineSegment(sketch, "E235.10.19.0", {"start": v(7.2, -43.55) * mm, "end": v(7.66, -43.4) * mm});
            skLineSegment(sketch, "E235.13.19.0", {"start": v(4.37, -44.3) * mm, "end": v(3.9, -44.4) * mm});
            skArc(sketch, "E235.15.19.0", {"start": v(6.04, -47) * mm, "mid": v(6.57, -46.87) * mm, "end": v(7.1, -46.72) * mm});
            skLineSegment(sketch, "E235.4.20.0", {"start": v(11.23, -45.12) * mm, "end": v(10.77, -41.98) * mm});
            skLineSegment(sketch, "E235.7.20.0", {"start": v(10.23, -45.59) * mm, "end": v(8.12, -43.21) * mm});
            skLineSegment(sketch, "E235.10.20.0", {"start": v(10.77, -41.98) * mm, "end": v(11.2, -41.74) * mm});
            skLineSegment(sketch, "E235.13.20.0", {"start": v(8.12, -43.21) * mm, "end": v(7.66, -43.4) * mm});
            skArc(sketch, "E235.15.20.0", {"start": v(10.23, -45.59) * mm, "mid": v(10.73, -45.36) * mm, "end": v(11.23, -45.12) * mm});
            skLineSegment(sketch, "E235.4.21.0", {"start": v(15.02, -42.82) * mm, "end": v(14.02, -39.8) * mm});
            skLineSegment(sketch, "E235.7.21.0", {"start": v(14.11, -43.46) * mm, "end": v(11.62, -41.49) * mm});
            skLineSegment(sketch, "E235.10.21.0", {"start": v(14.02, -39.8) * mm, "end": v(14.4, -39.5) * mm});
            skLineSegment(sketch, "E235.13.21.0", {"start": v(11.62, -41.49) * mm, "end": v(11.2, -41.74) * mm});
            skArc(sketch, "E235.15.21.0", {"start": v(14.11, -43.46) * mm, "mid": v(14.57, -43.14) * mm, "end": v(15.02, -42.82) * mm});
            skLineSegment(sketch, "E235.4.22.0", {"start": v(18.35, -39.9) * mm, "end": v(16.84, -37.1) * mm});
            skLineSegment(sketch, "E235.7.22.0", {"start": v(17.56, -40.68) * mm, "end": v(14.77, -39.18) * mm});
            skLineSegment(sketch, "E235.10.22.0", {"start": v(16.84, -37.1) * mm, "end": v(17.16, -36.74) * mm});
            skLineSegment(sketch, "E235.13.22.0", {"start": v(14.77, -39.18) * mm, "end": v(14.4, -39.5) * mm});
            skArc(sketch, "E235.15.22.0", {"start": v(17.56, -40.68) * mm, "mid": v(17.96, -40.3) * mm, "end": v(18.35, -39.9) * mm});
            skLineSegment(sketch, "E235.4.23.0", {"start": v(21.12, -36.45) * mm, "end": v(19.15, -33.96) * mm});
            skLineSegment(sketch, "E235.7.23.0", {"start": v(20.48, -37.36) * mm, "end": v(17.47, -36.36) * mm});
            skLineSegment(sketch, "E235.10.23.0", {"start": v(19.15, -33.96) * mm, "end": v(19.4, -33.54) * mm});
            skLineSegment(sketch, "E235.13.23.0", {"start": v(17.47, -36.36) * mm, "end": v(17.16, -36.74) * mm});
            skArc(sketch, "E235.15.23.0", {"start": v(20.48, -37.36) * mm, "mid": v(20.8, -36.9) * mm, "end": v(21.12, -36.45) * mm});
            skLineSegment(sketch, "E235.4.24.0", {"start": v(23.25, -32.57) * mm, "end": v(20.88, -30.46) * mm});
            skLineSegment(sketch, "E235.7.24.0", {"start": v(22.78, -33.57) * mm, "end": v(19.64, -33.11) * mm});
            skLineSegment(sketch, "E235.10.24.0", {"start": v(20.88, -30.46) * mm, "end": v(21.05, -30) * mm});
            skLineSegment(sketch, "E235.13.24.0", {"start": v(19.64, -33.11) * mm, "end": v(19.4, -33.54) * mm});
            skArc(sketch, "E235.15.24.0", {"start": v(22.78, -33.57) * mm, "mid": v(23.02, -33.07) * mm, "end": v(23.25, -32.57) * mm});
            skLineSegment(sketch, "E235.4.25.0", {"start": v(24.67, -28.37) * mm, "end": v(21.97, -26.7) * mm});
            skLineSegment(sketch, "E235.7.25.0", {"start": v(24.39, -29.44) * mm, "end": v(21.21, -29.54) * mm});
            skLineSegment(sketch, "E235.10.25.0", {"start": v(21.97, -26.7) * mm, "end": v(22.06, -26.23) * mm});
            skLineSegment(sketch, "E235.13.25.0", {"start": v(21.21, -29.54) * mm, "end": v(21.05, -30) * mm});
            skArc(sketch, "E235.15.25.0", {"start": v(24.39, -29.44) * mm, "mid": v(24.53, -28.91) * mm, "end": v(24.67, -28.37) * mm});
            skLineSegment(sketch, "E235.4.26.0", {"start": v(25.35, -24) * mm, "end": v(22.4, -22.83) * mm});
            skLineSegment(sketch, "E235.7.26.0", {"start": v(25.25, -25.1) * mm, "end": v(22.14, -25.74) * mm});
            skLineSegment(sketch, "E235.10.26.0", {"start": v(22.4, -22.83) * mm, "end": v(22.4, -22.34) * mm});
            skLineSegment(sketch, "E235.13.26.0", {"start": v(22.14, -25.74) * mm, "end": v(22.06, -26.23) * mm});
            skArc(sketch, "E235.15.26.0", {"start": v(25.25, -25.1) * mm, "mid": v(25.3, -24.55) * mm, "end": v(25.35, -24) * mm});
            skLineSegment(sketch, "E235.4.27.0", {"start": v(25.25, -19.57) * mm, "end": v(22.14, -18.93) * mm});
            skLineSegment(sketch, "E235.7.27.0", {"start": v(25.35, -20.68) * mm, "end": v(22.4, -21.85) * mm});
            skLineSegment(sketch, "E235.10.27.0", {"start": v(22.14, -18.93) * mm, "end": v(22.06, -18.45) * mm});
            skLineSegment(sketch, "E235.13.27.0", {"start": v(22.4, -21.85) * mm, "end": v(22.4, -22.34) * mm});
            skArc(sketch, "E235.15.27.0", {"start": v(25.35, -20.68) * mm, "mid": v(25.3, -20.12) * mm, "end": v(25.25, -19.57) * mm});
            skLineSegment(sketch, "E235.4.28.0", {"start": v(24.39, -15.23) * mm, "end": v(21.21, -15.14) * mm});
            skLineSegment(sketch, "E235.7.28.0", {"start": v(24.67, -16.3) * mm, "end": v(21.97, -17.97) * mm});
            skLineSegment(sketch, "E235.10.28.0", {"start": v(21.21, -15.14) * mm, "end": v(21.05, -14.67) * mm});
            skLineSegment(sketch, "E235.13.28.0", {"start": v(21.97, -17.97) * mm, "end": v(22.06, -18.45) * mm});
            skArc(sketch, "E235.15.28.0", {"start": v(24.67, -16.3) * mm, "mid": v(24.53, -15.76) * mm, "end": v(24.39, -15.23) * mm});
            skLineSegment(sketch, "E235.4.29.0", {"start": v(22.78, -11.1) * mm, "end": v(19.64, -11.56) * mm});
            skLineSegment(sketch, "E235.7.29.0", {"start": v(23.25, -12.1) * mm, "end": v(20.88, -14.22) * mm});
            skLineSegment(sketch, "E235.10.29.0", {"start": v(19.64, -11.56) * mm, "end": v(19.4, -11.13) * mm});
            skLineSegment(sketch, "E235.13.29.0", {"start": v(20.88, -14.22) * mm, "end": v(21.05, -14.67) * mm});
            skArc(sketch, "E235.15.29.0", {"start": v(23.25, -12.1) * mm, "mid": v(23.02, -11.6) * mm, "end": v(22.78, -11.1) * mm});
            skLineSegment(sketch, "E235.4.30.0", {"start": v(20.48, -7.32) * mm, "end": v(17.47, -8.32) * mm});
            skLineSegment(sketch, "E235.7.30.0", {"start": v(21.12, -8.23) * mm, "end": v(19.15, -10.72) * mm});
            skLineSegment(sketch, "E235.10.30.0", {"start": v(17.47, -8.32) * mm, "end": v(17.16, -7.94) * mm});
            skLineSegment(sketch, "E235.13.30.0", {"start": v(19.15, -10.72) * mm, "end": v(19.4, -11.13) * mm});
            skArc(sketch, "E235.15.30.0", {"start": v(21.12, -8.23) * mm, "mid": v(20.8, -7.77) * mm, "end": v(20.48, -7.32) * mm});
            skLineSegment(sketch, "E235.4.31.0", {"start": v(17.56, -3.99) * mm, "end": v(14.77, -5.5) * mm});
            skLineSegment(sketch, "E235.7.31.0", {"start": v(18.35, -4.77) * mm, "end": v(16.84, -7.57) * mm});
            skLineSegment(sketch, "E235.10.31.0", {"start": v(14.77, -5.5) * mm, "end": v(14.4, -5.17) * mm});
            skLineSegment(sketch, "E235.13.31.0", {"start": v(16.84, -7.57) * mm, "end": v(17.16, -7.94) * mm});
            skArc(sketch, "E235.15.31.0", {"start": v(18.35, -4.77) * mm, "mid": v(17.96, -4.38) * mm, "end": v(17.56, -3.99) * mm});
            skLineSegment(sketch, "E235.4.32.0", {"start": v(14.11, -1.22) * mm, "end": v(11.62, -3.19) * mm});
            skLineSegment(sketch, "E235.7.32.0", {"start": v(15.02, -1.85) * mm, "end": v(14.02, -4.87) * mm});
            skLineSegment(sketch, "E235.10.32.0", {"start": v(11.62, -3.19) * mm, "end": v(11.2, -2.93) * mm});
            skLineSegment(sketch, "E235.13.32.0", {"start": v(14.02, -4.87) * mm, "end": v(14.4, -5.17) * mm});
            skArc(sketch, "E235.15.32.0", {"start": v(15.02, -1.85) * mm, "mid": v(14.57, -1.53) * mm, "end": v(14.11, -1.22) * mm});
            skLineSegment(sketch, "E235.4.33.0", {"start": v(10.23, 0.91) * mm, "end": v(8.12, -1.46) * mm});
            skLineSegment(sketch, "E235.7.33.0", {"start": v(11.23, 0.44) * mm, "end": v(10.77, -2.7) * mm});
            skLineSegment(sketch, "E235.10.33.0", {"start": v(8.12, -1.46) * mm, "end": v(7.66, -1.28) * mm});
            skLineSegment(sketch, "E235.13.33.0", {"start": v(10.77, -2.7) * mm, "end": v(11.2, -2.93) * mm});
            skArc(sketch, "E235.15.33.0", {"start": v(11.23, 0.44) * mm, "mid": v(10.73, 0.68) * mm, "end": v(10.23, 0.91) * mm});
            skLineSegment(sketch, "E235.4.34.0", {"start": v(6.04, 2.34) * mm, "end": v(4.37, -0.37) * mm});
            skLineSegment(sketch, "E235.7.34.0", {"start": v(7.1, 2.05) * mm, "end": v(7.2, -1.13) * mm});
            skLineSegment(sketch, "E235.10.34.0", {"start": v(4.37, -0.37) * mm, "end": v(3.9, -0.27) * mm});
            skLineSegment(sketch, "E235.13.34.0", {"start": v(7.2, -1.13) * mm, "end": v(7.66, -1.28) * mm});
            skArc(sketch, "E235.15.34.0", {"start": v(7.1, 2.05) * mm, "mid": v(6.57, 2.2) * mm, "end": v(6.04, 2.34) * mm});
            skLineSegment(sketch, "E235.4.35.0", {"start": v(1.66, 3) * mm, "end": v(0.49, 0.06) * mm});
            skLineSegment(sketch, "E235.7.35.0", {"start": v(2.77, 2.91) * mm, "end": v(3.4, -0.2) * mm});
            skLineSegment(sketch, "E235.10.35.0", {"start": v(0.49, 0.06) * mm, "end": v(0, 0.07) * mm});
            skLineSegment(sketch, "E235.13.35.0", {"start": v(3.4, -0.2) * mm, "end": v(3.9, -0.27) * mm});
            skArc(sketch, "E235.15.35.0", {"start": v(2.77, 2.91) * mm, "mid": v(2.21, 2.97) * mm, "end": v(1.66, 3) * mm});
            skSolve(sketch);
        }
        {
            var Q0;
            Q0=sQuery(id+"F34.wireOp",VERTEX,"E210.9.2.start");
            var Q1;
            Q1=sQuery(id+"F36.wireOp",VERTEX,"E235.15.9.0.start");
            var Q2;
            Q2=sQuery(id+"F34.wireOp",VERTEX,"E210.9.3.start");
            cPlane(context, id + "F37", {"entities" : qUnion([Q0, Q1, Q2]), "cplaneType" : CPlaneType.THREE_POINT, "offset" : 150 * mm, "width" : 150 * mm, "height" : 150 * mm});
        }
        {
            var Q0;
            Q0=qCreatedBy(id+"F37.planeOp",FACE);
            var sketch = newSketch(context, id + "F38", { "sketchPlane" : qUnion([Q0])});
            skLineSegment(sketch, "E236", {"start": v(20.73, -24.43) * mm, "end": v(12.3, -23.52) * mm});
            skSolve(sketch);
        }
        {
            var Q1;
            Q1=makeQuery(id+"F36.imprint","IMPRINT",FACE,{"disambiguationData":[TD([[makeQuery(id+"F36.imprint","IMPRINT",EDGE,{"derivedFrom":sQuery(id+"F36.wireOp",EDGE,"E229")}),1.0]])]});
            var Q2;
            Q2=makeQuery(id+"F34.imprint","IMPRINT",FACE,{"disambiguationData":[TD([[makeQuery(id+"F34.imprint","IMPRINT",EDGE,{"derivedFrom":sQuery(id+"F34.wireOp",EDGE,"E205")}),1.0]])]});
            var Q3;
            Q3=sQuery(id+"F38.wireOp",EDGE,"E236");
            loft(context, id + "F39", {"sheetProfilesArray" : [{ "sheetProfileEntities" : qUnion([Q1]) }, { "sheetProfileEntities" : qUnion([Q2]) }], "guidesArray" : [{ "guideEntities" : qUnion([Q3]), "guideDerivativeType" : LoftGuideDerivativeType.DEFAULT, "guideDerivativeMagnitude" : 1 }]});
        }
        {
            var Q0;
            Q0=makeQuery(id+"F39.opLoft","CAP_FACE",FACE,{"disambiguationData":[OSD([makeQuery(id+"F34.imprint","IMPRINT",FACE,{"disambiguationData":[TD([[makeQuery(id+"F34.imprint","IMPRINT",EDGE,{"derivedFrom":sQuery(id+"F34.wireOp",EDGE,"E205")}),1.0]])]})])],"isStart":true});
            var sketch = newSketch(context, id + "F40", { "sketchPlane" : qUnion([Q0])});
            skCircle(sketch, "E237", {"center": v(0, -22.34) * mm, "radius": 2.5 * mm});
            skSolve(sketch);
        }
        {
            var Q0;
            Q0=makeQuery(id+"F40.imprint","IMPRINT",FACE,{"disambiguationData":[TD([[makeQuery(id+"F40.imprint","IMPRINT",EDGE,{"derivedFrom":sQuery(id+"F40.wireOp",EDGE,"E237")}),1.0]])]});
            extrude(context, id + "F41", {"entities" : qUnion([Q0]), "operationType" : NewBodyOperationType.REMOVE, "oppositeDirection" : true, "depth" : 25 * mm});
        }
        {
            var Q0;
            Q0=qCreatedBy(makeId("Top.planeOp"),FACE);
            cPlane(context, id + "F42", {"entities" : qUnion([Q0]), "cplaneType" : CPlaneType.OFFSET, "offset" : 500 * mm, "oppositeDirection" : true, "width" : 150 * mm, "height" : 150 * mm});
        }
    });
